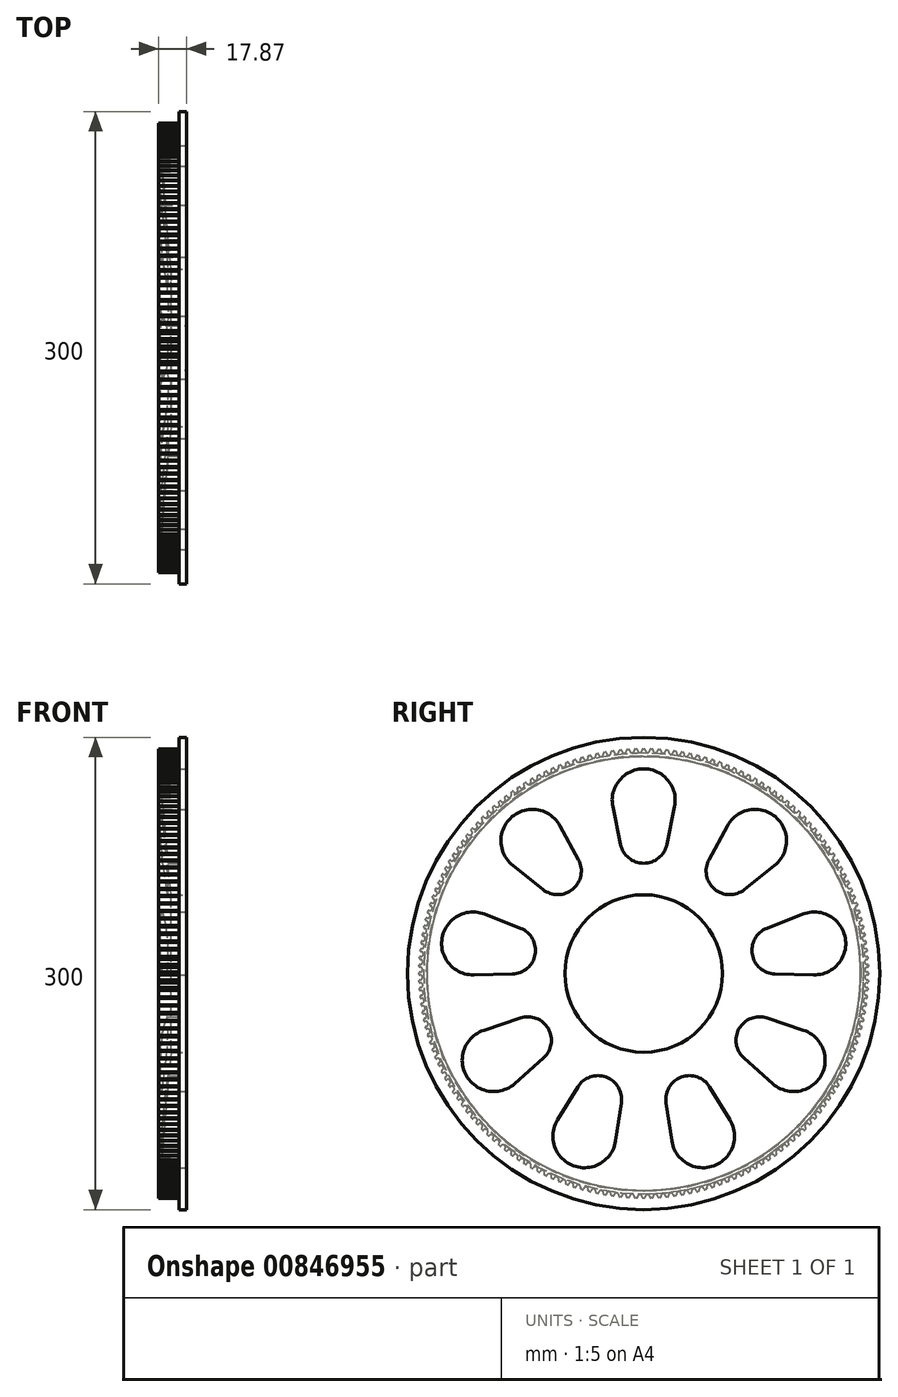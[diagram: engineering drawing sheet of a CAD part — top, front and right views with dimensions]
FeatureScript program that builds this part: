
annotation { "Feature Type Name" : "Feature", "Feature Type Description" : "" }
export const myFeature = defineFeature(function(context is Context, id is Id, definition is map)
    precondition{}
    {
        {
            var Q0;
            Q0=qCreatedBy(makeId("Front.planeOp"),FACE);
            var sketch = newSketch(context, id + "F0", { "sketchPlane" : qUnion([Q0])});
            skLineSegment(sketch, "E0", {"start": v(-17.87, 139.92) * mm, "end": v(-4.72, 139.92) * mm});
            skLineSegment(sketch, "E1", {"start": v(-4.72, 139.92) * mm, "end": v(-4.72, 150) * mm});
            skLineSegment(sketch, "E2", {"start": v(-4.72, 150) * mm, "end": v(0, 150) * mm});
            skLineSegment(sketch, "E3", {"start": v(0, 150) * mm, "end": v(0, 50) * mm});
            skLineSegment(sketch, "E4", {"start": v(0, 50) * mm, "end": v(-10, 50) * mm});
            skLineSegment(sketch, "E5", {"start": v(-10, 50) * mm, "end": v(-17.87, 139.92) * mm});
            skLineSegment(sketch, "E6", {"start": v(0, 0) * mm, "end": v(-63.64, 0) * mm, "construction": true});
            skSolve(sketch);
        }
        {
            var Q0;
            Q0 = qSketchRegion(id + "F0", true);
            var Q1;
            Q1 = qConstructionFilter(qBodyType(qCreatedBy(id + "F0" ,EDGE), BodyType.WIRE), ConstructionObject.NO);
            var Q2;
            Q2=sQuery(id+"F0.wireOp",EDGE,"E6");
            revolve(context, id + "F1", {"surfaceOperationType" : NewSurfaceOperationType.NEW, "entities" : qUnion([Q0]), "surfaceEntities" : qUnion([Q1]), "axis" : qUnion([Q2]), "revolveType" : RevolveType.FULL});
        }
        {
            var Q0;
            Q0=qCreatedBy(makeId("Right.planeOp"),FACE);
            var sketch = newSketch(context, id + "F2", { "sketchPlane" : qUnion([Q0])});
            skArc(sketch, "E7", {"start": v(19.6, 106) * mm, "mid": v(0, 130) * mm, "end": v(-19.6, 106) * mm});
            skArc(sketch, "E8", {"start": v(-14.7, 82) * mm, "mid": v(0, 70) * mm, "end": v(14.7, 82) * mm});
            skLineSegment(sketch, "E9", {"start": v(-19.6, 106) * mm, "end": v(-14.7, 82) * mm});
            skLineSegment(sketch, "E10", {"start": v(19.6, 106) * mm, "end": v(14.7, 82) * mm});
            skCircle(sketch, "E11", {"center": v(0, 0) * mm, "radius": 85 * mm, "construction": true});
            skCircle(sketch, "E12", {"center": v(0, 0) * mm, "radius": 110 * mm, "construction": true});
            skLineSegment(sketch, "E13.1.0", {"start": v(-83.15, 68.6) * mm, "end": v(-63.97, 53.37) * mm});
            skArc(sketch, "E13.1.1", {"start": v(-63.97, 53.37) * mm, "mid": v(-45, 53.62) * mm, "end": v(-41.45, 72.26) * mm});
            skArc(sketch, "E13.1.2", {"start": v(-53.12, 93.8) * mm, "mid": v(-83.56, 99.59) * mm, "end": v(-83.15, 68.6) * mm});
            skLineSegment(sketch, "E13.1.3", {"start": v(-53.12, 93.8) * mm, "end": v(-41.45, 72.26) * mm});
            skLineSegment(sketch, "E13.2.0", {"start": v(-107.8, -0.9) * mm, "end": v(-83.3, -0.23) * mm});
            skArc(sketch, "E13.2.1", {"start": v(-83.3, -0.23) * mm, "mid": v(-68.94, 12.16) * mm, "end": v(-78.2, 28.71) * mm});
            skArc(sketch, "E13.2.2", {"start": v(-100.99, 37.7) * mm, "mid": v(-128.03, 22.57) * mm, "end": v(-107.8, -0.9) * mm});
            skLineSegment(sketch, "E13.2.3", {"start": v(-100.99, 37.7) * mm, "end": v(-78.2, 28.71) * mm});
            skLineSegment(sketch, "E13.3.0", {"start": v(-82, -69.97) * mm, "end": v(-63.67, -53.73) * mm});
            skArc(sketch, "E13.3.1", {"start": v(-63.67, -53.73) * mm, "mid": v(-60.62, -35) * mm, "end": v(-78.36, -28.27) * mm});
            skArc(sketch, "E13.3.2", {"start": v(-101.6, -36.03) * mm, "mid": v(-112.58, -65) * mm, "end": v(-82, -69.97) * mm});
            skLineSegment(sketch, "E13.3.3", {"start": v(-101.6, -36.03) * mm, "end": v(-78.36, -28.27) * mm});
            skLineSegment(sketch, "E13.4.0", {"start": v(-17.84, -106.3) * mm, "end": v(-14.24, -82.08) * mm});
            skArc(sketch, "E13.4.1", {"start": v(-14.24, -82.08) * mm, "mid": v(-23.94, -65.78) * mm, "end": v(-41.86, -72.03) * mm});
            skArc(sketch, "E13.4.2", {"start": v(-54.67, -92.9) * mm, "mid": v(-44.46, -122.16) * mm, "end": v(-17.84, -106.3) * mm});
            skLineSegment(sketch, "E13.4.3", {"start": v(-54.67, -92.9) * mm, "end": v(-41.86, -72.03) * mm});
            skLineSegment(sketch, "E13.5.0", {"start": v(54.67, -92.9) * mm, "end": v(41.86, -72.03) * mm});
            skArc(sketch, "E13.5.1", {"start": v(41.86, -72.03) * mm, "mid": v(23.94, -65.78) * mm, "end": v(14.24, -82.08) * mm});
            skArc(sketch, "E13.5.2", {"start": v(17.84, -106.3) * mm, "mid": v(44.46, -122.16) * mm, "end": v(54.67, -92.9) * mm});
            skLineSegment(sketch, "E13.5.3", {"start": v(17.84, -106.3) * mm, "end": v(14.24, -82.08) * mm});
            skLineSegment(sketch, "E13.6.0", {"start": v(101.6, -36.03) * mm, "end": v(78.36, -28.27) * mm});
            skArc(sketch, "E13.6.1", {"start": v(78.36, -28.27) * mm, "mid": v(60.62, -35) * mm, "end": v(63.67, -53.73) * mm});
            skArc(sketch, "E13.6.2", {"start": v(82, -69.97) * mm, "mid": v(112.58, -65) * mm, "end": v(101.6, -36.03) * mm});
            skLineSegment(sketch, "E13.6.3", {"start": v(82, -69.97) * mm, "end": v(63.67, -53.73) * mm});
            skLineSegment(sketch, "E13.7.0", {"start": v(100.99, 37.7) * mm, "end": v(78.2, 28.71) * mm});
            skArc(sketch, "E13.7.1", {"start": v(78.2, 28.71) * mm, "mid": v(68.94, 12.16) * mm, "end": v(83.3, -0.23) * mm});
            skArc(sketch, "E13.7.2", {"start": v(107.8, -0.9) * mm, "mid": v(128.03, 22.57) * mm, "end": v(100.99, 37.7) * mm});
            skLineSegment(sketch, "E13.7.3", {"start": v(107.8, -0.9) * mm, "end": v(83.3, -0.23) * mm});
            skArc(sketch, "E14.3.8.0", {"start": v(41.45, 72.26) * mm, "mid": v(45, 53.62) * mm, "end": v(63.97, 53.37) * mm});
            skArc(sketch, "E14.7.8.0", {"start": v(83.15, 68.6) * mm, "mid": v(83.56, 99.59) * mm, "end": v(53.12, 93.8) * mm});
            skLineSegment(sketch, "E14.8.8.0", {"start": v(53.12, 93.8) * mm, "end": v(41.45, 72.26) * mm});
            skLineSegment(sketch, "E14.11.8.0", {"start": v(83.15, 68.6) * mm, "end": v(63.97, 53.37) * mm});
            skSolve(sketch);
        }
        {
            var Q0;
            Q0 = qSketchRegion(id + "F2", true);
            extrude(context, id + "F3", {"entities" : qUnion([Q0]), "operationType" : NewBodyOperationType.REMOVE, "endBound" : BoundingType.THROUGH_ALL, "oppositeDirection" : true, "depth" : 25 * mm, "offsetDistance" : 25 * mm});
        }
        {
            var Q0;
            Q0=makeQuery(id+"F1.opRevolve","SWEPT_FACE",FACE,{"disambiguationData":[OSD([sQuery(id+"F0.wireOp",EDGE,"E1")])]});
            var sketch = newSketch(context, id + "F4", { "sketchPlane" : qUnion([Q0])});
            skArc(sketch, "E15", {"start": v(0.94, 142.17) * mm, "mid": v(0.82, 142.52) * mm, "end": v(0.49, 142.67) * mm});
            skLineSegment(sketch, "E16", {"start": v(0, 142.67) * mm, "end": v(0, 137.75) * mm, "construction": true});
            skLineSegment(sketch, "E17", {"start": v(4.8, 137.58) * mm, "end": v(6.82, 195.24) * mm, "construction": true});
            skCircle(sketch, "E18", {"center": v(0, 0) * mm, "radius": 140.48 * mm, "construction": true});
            skCircle(sketch, "E19", {"center": v(0, 0) * mm, "radius": 142.67 * mm, "construction": true});
            skCircle(sketch, "E20", {"center": v(0, 0) * mm, "radius": 143.24 * mm, "construction": true});
            skArc(sketch, "E21", {"start": v(4.5, 142.6) * mm, "mid": v(4.15, 142.46) * mm, "end": v(4.02, 142.11) * mm});
            skArc(sketch, "E22", {"start": v(0.94, 142.17) * mm, "mid": v(2.45, 140.46) * mm, "end": v(4.02, 142.11) * mm});
            skLineSegment(sketch, "E23", {"start": v(0, 0) * mm, "end": v(4.11, 235.63) * mm, "construction": true});
            skLineSegment(sketch, "E24", {"start": v(0.49, 142.67) * mm, "end": v(0, 142.67) * mm});
            skLineSegment(sketch, "E25", {"start": v(4.98, 142.58) * mm, "end": v(4.5, 142.6) * mm});
            skLineSegment(sketch, "E26", {"start": v(4.98, 142.58) * mm, "end": v(4.8, 137.58) * mm});
            skLineSegment(sketch, "E27", {"start": v(0, 137.75) * mm, "end": v(0, 142.67) * mm});
            skLineSegment(sketch, "E28", {"start": v(0, 137.75) * mm, "end": v(4.8, 137.58) * mm});
            skArc(sketch, "E29.1.0", {"start": v(-4.02, 142.11) * mm, "mid": v(-2.45, 140.46) * mm, "end": v(-0.94, 142.17) * mm});
            skLineSegment(sketch, "E29.1.1", {"start": v(-4.98, 142.58) * mm, "end": v(-4.8, 137.67) * mm, "construction": true});
            skLineSegment(sketch, "E29.1.2", {"start": v(0, 142.67) * mm, "end": v(0, 137.67) * mm});
            skLineSegment(sketch, "E29.1.3", {"start": v(-4.8, 137.67) * mm, "end": v(0, 137.67) * mm});
            skLineSegment(sketch, "E29.1.4", {"start": v(-4.8, 137.67) * mm, "end": v(-4.98, 142.58) * mm});
            skLineSegment(sketch, "E29.1.5", {"start": v(0, 142.67) * mm, "end": v(-0.49, 142.67) * mm});
            skArc(sketch, "E29.1.6", {"start": v(-0.49, 142.67) * mm, "mid": v(-0.82, 142.52) * mm, "end": v(-0.94, 142.17) * mm});
            skArc(sketch, "E29.1.7", {"start": v(-4.02, 142.11) * mm, "mid": v(-4.15, 142.46) * mm, "end": v(-4.5, 142.6) * mm});
            skLineSegment(sketch, "E29.1.8", {"start": v(-4.5, 142.6) * mm, "end": v(-4.98, 142.58) * mm});
            skArc(sketch, "E29.2.0", {"start": v(-8.98, 141.89) * mm, "mid": v(-7.35, 140.3) * mm, "end": v(-5.9, 142.05) * mm});
            skLineSegment(sketch, "E29.2.1", {"start": v(-9.95, 142.32) * mm, "end": v(-9.6, 137.41) * mm, "construction": true});
            skLineSegment(sketch, "E29.2.2", {"start": v(-4.98, 142.58) * mm, "end": v(-4.8, 137.58) * mm});
            skLineSegment(sketch, "E29.2.3", {"start": v(-9.6, 137.41) * mm, "end": v(-4.8, 137.58) * mm});
            skLineSegment(sketch, "E29.2.4", {"start": v(-9.6, 137.41) * mm, "end": v(-9.95, 142.32) * mm});
            skLineSegment(sketch, "E29.2.5", {"start": v(-4.98, 142.58) * mm, "end": v(-5.47, 142.56) * mm});
            skArc(sketch, "E29.2.6", {"start": v(-5.47, 142.56) * mm, "mid": v(-5.8, 142.4) * mm, "end": v(-5.9, 142.05) * mm});
            skArc(sketch, "E29.2.7", {"start": v(-8.98, 141.89) * mm, "mid": v(-9.12, 142.23) * mm, "end": v(-9.46, 142.35) * mm});
            skLineSegment(sketch, "E29.2.8", {"start": v(-9.46, 142.35) * mm, "end": v(-9.95, 142.32) * mm});
            skArc(sketch, "E29.3.0", {"start": v(-13.93, 141.49) * mm, "mid": v(-12.24, 139.95) * mm, "end": v(-10.85, 141.76) * mm});
            skLineSegment(sketch, "E29.3.1", {"start": v(-14.91, 141.89) * mm, "end": v(-14.4, 137) * mm, "construction": true});
            skLineSegment(sketch, "E29.3.2", {"start": v(-9.95, 142.32) * mm, "end": v(-9.6, 137.33) * mm});
            skLineSegment(sketch, "E29.3.3", {"start": v(-14.4, 137) * mm, "end": v(-9.6, 137.33) * mm});
            skLineSegment(sketch, "E29.3.4", {"start": v(-14.4, 137) * mm, "end": v(-14.91, 141.89) * mm});
            skLineSegment(sketch, "E29.3.5", {"start": v(-9.95, 142.32) * mm, "end": v(-10.44, 142.29) * mm});
            skArc(sketch, "E29.3.6", {"start": v(-10.44, 142.29) * mm, "mid": v(-10.76, 142.11) * mm, "end": v(-10.85, 141.76) * mm});
            skArc(sketch, "E29.3.7", {"start": v(-13.93, 141.49) * mm, "mid": v(-14.08, 141.82) * mm, "end": v(-14.43, 141.94) * mm});
            skLineSegment(sketch, "E29.3.8", {"start": v(-14.43, 141.94) * mm, "end": v(-14.91, 141.89) * mm});
            skArc(sketch, "E29.4.0", {"start": v(-18.86, 140.91) * mm, "mid": v(-17.12, 139.44) * mm, "end": v(-15.8, 141.3) * mm});
            skLineSegment(sketch, "E29.4.1", {"start": v(-19.86, 141.28) * mm, "end": v(-19.17, 136.4) * mm, "construction": true});
            skLineSegment(sketch, "E29.4.2", {"start": v(-14.91, 141.89) * mm, "end": v(-14.39, 136.91) * mm});
            skLineSegment(sketch, "E29.4.3", {"start": v(-19.17, 136.4) * mm, "end": v(-14.39, 136.91) * mm});
            skLineSegment(sketch, "E29.4.4", {"start": v(-19.17, 136.4) * mm, "end": v(-19.86, 141.28) * mm});
            skLineSegment(sketch, "E29.4.5", {"start": v(-14.91, 141.89) * mm, "end": v(-15.4, 141.83) * mm});
            skArc(sketch, "E29.4.6", {"start": v(-15.4, 141.83) * mm, "mid": v(-15.72, 141.65) * mm, "end": v(-15.8, 141.3) * mm});
            skArc(sketch, "E29.4.7", {"start": v(-18.86, 140.91) * mm, "mid": v(-19.02, 141.24) * mm, "end": v(-19.37, 141.35) * mm});
            skLineSegment(sketch, "E29.4.8", {"start": v(-19.37, 141.35) * mm, "end": v(-19.86, 141.28) * mm});
            skArc(sketch, "E29.5.0", {"start": v(-23.76, 140.17) * mm, "mid": v(-21.98, 138.75) * mm, "end": v(-20.72, 140.65) * mm});
            skLineSegment(sketch, "E29.5.1", {"start": v(-24.77, 140.5) * mm, "end": v(-23.92, 135.66) * mm, "construction": true});
            skLineSegment(sketch, "E29.5.2", {"start": v(-19.86, 141.28) * mm, "end": v(-19.16, 136.33) * mm});
            skLineSegment(sketch, "E29.5.3", {"start": v(-23.92, 135.66) * mm, "end": v(-19.16, 136.33) * mm});
            skLineSegment(sketch, "E29.5.4", {"start": v(-23.92, 135.66) * mm, "end": v(-24.77, 140.5) * mm});
            skLineSegment(sketch, "E29.5.5", {"start": v(-19.86, 141.28) * mm, "end": v(-20.34, 141.21) * mm});
            skArc(sketch, "E29.5.6", {"start": v(-20.34, 141.21) * mm, "mid": v(-20.65, 141.02) * mm, "end": v(-20.72, 140.65) * mm});
            skArc(sketch, "E29.5.7", {"start": v(-23.76, 140.17) * mm, "mid": v(-23.94, 140.5) * mm, "end": v(-24.3, 140.58) * mm});
            skLineSegment(sketch, "E29.5.8", {"start": v(-24.3, 140.58) * mm, "end": v(-24.77, 140.5) * mm});
            skArc(sketch, "E29.6.0", {"start": v(-28.64, 139.26) * mm, "mid": v(-26.8, 137.9) * mm, "end": v(-25.61, 139.84) * mm});
            skLineSegment(sketch, "E29.6.1", {"start": v(-29.66, 139.55) * mm, "end": v(-28.64, 134.74) * mm, "construction": true});
            skLineSegment(sketch, "E29.6.2", {"start": v(-24.77, 140.5) * mm, "end": v(-23.9, 135.57) * mm});
            skLineSegment(sketch, "E29.6.3", {"start": v(-28.64, 134.74) * mm, "end": v(-23.9, 135.57) * mm});
            skLineSegment(sketch, "E29.6.4", {"start": v(-28.64, 134.74) * mm, "end": v(-29.66, 139.55) * mm});
            skLineSegment(sketch, "E29.6.5", {"start": v(-24.77, 140.5) * mm, "end": v(-25.25, 140.41) * mm});
            skArc(sketch, "E29.6.6", {"start": v(-25.25, 140.41) * mm, "mid": v(-25.56, 140.2) * mm, "end": v(-25.61, 139.84) * mm});
            skArc(sketch, "E29.6.7", {"start": v(-28.64, 139.26) * mm, "mid": v(-28.82, 139.57) * mm, "end": v(-29.18, 139.65) * mm});
            skLineSegment(sketch, "E29.6.8", {"start": v(-29.18, 139.65) * mm, "end": v(-29.66, 139.55) * mm});
            skArc(sketch, "E29.7.0", {"start": v(-33.48, 138.17) * mm, "mid": v(-31.6, 136.88) * mm, "end": v(-30.48, 138.87) * mm});
            skLineSegment(sketch, "E29.7.1", {"start": v(-34.51, 138.43) * mm, "end": v(-33.32, 133.66) * mm, "construction": true});
            skLineSegment(sketch, "E29.7.2", {"start": v(-29.66, 139.55) * mm, "end": v(-28.62, 134.66) * mm});
            skLineSegment(sketch, "E29.7.3", {"start": v(-33.32, 133.66) * mm, "end": v(-28.62, 134.66) * mm});
            skLineSegment(sketch, "E29.7.4", {"start": v(-33.32, 133.66) * mm, "end": v(-34.51, 138.43) * mm});
            skLineSegment(sketch, "E29.7.5", {"start": v(-29.66, 139.55) * mm, "end": v(-30.14, 139.45) * mm});
            skArc(sketch, "E29.7.6", {"start": v(-30.14, 139.45) * mm, "mid": v(-30.44, 139.23) * mm, "end": v(-30.48, 138.87) * mm});
            skArc(sketch, "E29.7.7", {"start": v(-33.48, 138.17) * mm, "mid": v(-33.68, 138.48) * mm, "end": v(-34.04, 138.55) * mm});
            skLineSegment(sketch, "E29.7.8", {"start": v(-34.04, 138.55) * mm, "end": v(-34.51, 138.43) * mm});
            skArc(sketch, "E29.8.0", {"start": v(-38.28, 136.92) * mm, "mid": v(-36.36, 135.7) * mm, "end": v(-35.3, 137.72) * mm});
            skLineSegment(sketch, "E29.8.1", {"start": v(-39.32, 137.14) * mm, "end": v(-37.97, 132.41) * mm, "construction": true});
            skLineSegment(sketch, "E29.8.2", {"start": v(-34.51, 138.43) * mm, "end": v(-33.3, 133.58) * mm});
            skLineSegment(sketch, "E29.8.3", {"start": v(-37.97, 132.41) * mm, "end": v(-33.3, 133.58) * mm});
            skLineSegment(sketch, "E29.8.4", {"start": v(-37.97, 132.41) * mm, "end": v(-39.32, 137.14) * mm});
            skLineSegment(sketch, "E29.8.5", {"start": v(-34.51, 138.43) * mm, "end": v(-34.99, 138.31) * mm});
            skArc(sketch, "E29.8.6", {"start": v(-34.99, 138.31) * mm, "mid": v(-35.28, 138.08) * mm, "end": v(-35.3, 137.72) * mm});
            skArc(sketch, "E29.8.7", {"start": v(-38.28, 136.92) * mm, "mid": v(-38.5, 137.22) * mm, "end": v(-38.85, 137.28) * mm});
            skLineSegment(sketch, "E29.8.8", {"start": v(-38.85, 137.28) * mm, "end": v(-39.32, 137.14) * mm});
            skArc(sketch, "E29.9.0", {"start": v(-43.04, 135.5) * mm, "mid": v(-41.07, 134.35) * mm, "end": v(-40.09, 136.4) * mm});
            skLineSegment(sketch, "E29.9.1", {"start": v(-44.09, 135.69) * mm, "end": v(-42.57, 131) * mm, "construction": true});
            skLineSegment(sketch, "E29.9.2", {"start": v(-39.32, 137.14) * mm, "end": v(-37.95, 132.33) * mm});
            skLineSegment(sketch, "E29.9.3", {"start": v(-42.57, 131) * mm, "end": v(-37.95, 132.33) * mm});
            skLineSegment(sketch, "E29.9.4", {"start": v(-42.57, 131) * mm, "end": v(-44.09, 135.69) * mm});
            skLineSegment(sketch, "E29.9.5", {"start": v(-39.32, 137.14) * mm, "end": v(-39.8, 137) * mm});
            skArc(sketch, "E29.9.6", {"start": v(-39.8, 137) * mm, "mid": v(-40.08, 136.77) * mm, "end": v(-40.09, 136.4) * mm});
            skArc(sketch, "E29.9.7", {"start": v(-43.04, 135.5) * mm, "mid": v(-43.26, 135.8) * mm, "end": v(-43.62, 135.84) * mm});
            skLineSegment(sketch, "E29.9.8", {"start": v(-43.62, 135.84) * mm, "end": v(-44.09, 135.69) * mm});
            skArc(sketch, "E29.10.0", {"start": v(-47.74, 133.91) * mm, "mid": v(-45.74, 132.83) * mm, "end": v(-44.82, 134.92) * mm});
            skLineSegment(sketch, "E29.10.1", {"start": v(-48.8, 134.06) * mm, "end": v(-47.11, 129.44) * mm, "construction": true});
            skLineSegment(sketch, "E29.10.2", {"start": v(-44.09, 135.69) * mm, "end": v(-42.54, 130.93) * mm});
            skLineSegment(sketch, "E29.10.3", {"start": v(-47.11, 129.44) * mm, "end": v(-42.54, 130.93) * mm});
            skLineSegment(sketch, "E29.10.4", {"start": v(-47.11, 129.44) * mm, "end": v(-48.8, 134.06) * mm});
            skLineSegment(sketch, "E29.10.5", {"start": v(-44.09, 135.69) * mm, "end": v(-44.55, 135.53) * mm});
            skArc(sketch, "E29.10.6", {"start": v(-44.55, 135.53) * mm, "mid": v(-44.82, 135.29) * mm, "end": v(-44.82, 134.92) * mm});
            skArc(sketch, "E29.10.7", {"start": v(-47.74, 133.91) * mm, "mid": v(-47.97, 134.2) * mm, "end": v(-48.34, 134.23) * mm});
            skLineSegment(sketch, "E29.10.8", {"start": v(-48.34, 134.23) * mm, "end": v(-48.8, 134.06) * mm});
            skArc(sketch, "E29.11.0", {"start": v(-52.39, 132.17) * mm, "mid": v(-50.35, 131.15) * mm, "end": v(-49.5, 133.27) * mm});
            skLineSegment(sketch, "E29.11.1", {"start": v(-53.44, 132.28) * mm, "end": v(-51.6, 127.72) * mm, "construction": true});
            skLineSegment(sketch, "E29.11.2", {"start": v(-48.8, 134.06) * mm, "end": v(-47.08, 129.36) * mm});
            skLineSegment(sketch, "E29.11.3", {"start": v(-51.6, 127.72) * mm, "end": v(-47.08, 129.36) * mm});
            skLineSegment(sketch, "E29.11.4", {"start": v(-51.6, 127.72) * mm, "end": v(-53.44, 132.28) * mm});
            skLineSegment(sketch, "E29.11.5", {"start": v(-48.8, 134.06) * mm, "end": v(-49.25, 133.9) * mm});
            skArc(sketch, "E29.11.6", {"start": v(-49.25, 133.9) * mm, "mid": v(-49.52, 133.64) * mm, "end": v(-49.5, 133.27) * mm});
            skArc(sketch, "E29.11.7", {"start": v(-52.39, 132.17) * mm, "mid": v(-52.62, 132.45) * mm, "end": v(-53, 132.46) * mm});
            skLineSegment(sketch, "E29.11.8", {"start": v(-53, 132.46) * mm, "end": v(-53.44, 132.28) * mm});
            skArc(sketch, "E29.12.0", {"start": v(-56.97, 130.26) * mm, "mid": v(-54.9, 129.32) * mm, "end": v(-54.13, 131.46) * mm});
            skLineSegment(sketch, "E29.12.1", {"start": v(-58.03, 130.33) * mm, "end": v(-56.03, 125.84) * mm, "construction": true});
            skLineSegment(sketch, "E29.12.2", {"start": v(-53.44, 132.28) * mm, "end": v(-51.57, 127.64) * mm});
            skLineSegment(sketch, "E29.12.3", {"start": v(-56.03, 125.84) * mm, "end": v(-51.57, 127.64) * mm});
            skLineSegment(sketch, "E29.12.4", {"start": v(-56.03, 125.84) * mm, "end": v(-58.03, 130.33) * mm});
            skLineSegment(sketch, "E29.12.5", {"start": v(-53.44, 132.28) * mm, "end": v(-53.9, 132.1) * mm});
            skArc(sketch, "E29.12.6", {"start": v(-53.9, 132.1) * mm, "mid": v(-54.15, 131.83) * mm, "end": v(-54.13, 131.46) * mm});
            skArc(sketch, "E29.12.7", {"start": v(-56.97, 130.26) * mm, "mid": v(-57.21, 130.53) * mm, "end": v(-57.58, 130.53) * mm});
            skLineSegment(sketch, "E29.12.8", {"start": v(-57.58, 130.53) * mm, "end": v(-58.03, 130.33) * mm});
            skArc(sketch, "E29.13.0", {"start": v(-61.48, 128.2) * mm, "mid": v(-59.37, 127.32) * mm, "end": v(-58.68, 129.5) * mm});
            skLineSegment(sketch, "E29.13.1", {"start": v(-62.54, 128.23) * mm, "end": v(-60.39, 123.8) * mm, "construction": true});
            skLineSegment(sketch, "E29.13.2", {"start": v(-58.03, 130.33) * mm, "end": v(-56, 125.76) * mm});
            skLineSegment(sketch, "E29.13.3", {"start": v(-60.39, 123.8) * mm, "end": v(-56, 125.76) * mm});
            skLineSegment(sketch, "E29.13.4", {"start": v(-60.39, 123.8) * mm, "end": v(-62.54, 128.23) * mm});
            skLineSegment(sketch, "E29.13.5", {"start": v(-58.03, 130.33) * mm, "end": v(-58.47, 130.13) * mm});
            skArc(sketch, "E29.13.6", {"start": v(-58.47, 130.13) * mm, "mid": v(-58.72, 129.86) * mm, "end": v(-58.68, 129.5) * mm});
            skArc(sketch, "E29.13.7", {"start": v(-61.48, 128.2) * mm, "mid": v(-61.73, 128.45) * mm, "end": v(-62.1, 128.44) * mm});
            skLineSegment(sketch, "E29.13.8", {"start": v(-62.1, 128.44) * mm, "end": v(-62.54, 128.23) * mm});
            skArc(sketch, "E29.14.0", {"start": v(-65.91, 125.97) * mm, "mid": v(-63.78, 125.17) * mm, "end": v(-63.17, 127.37) * mm});
            skLineSegment(sketch, "E29.14.1", {"start": v(-66.98, 125.97) * mm, "end": v(-64.67, 121.63) * mm, "construction": true});
            skLineSegment(sketch, "E29.14.2", {"start": v(-62.54, 128.23) * mm, "end": v(-60.35, 123.73) * mm});
            skLineSegment(sketch, "E29.14.3", {"start": v(-64.67, 121.63) * mm, "end": v(-60.35, 123.73) * mm});
            skLineSegment(sketch, "E29.14.4", {"start": v(-64.67, 121.63) * mm, "end": v(-66.98, 125.97) * mm});
            skLineSegment(sketch, "E29.14.5", {"start": v(-62.54, 128.23) * mm, "end": v(-62.98, 128.01) * mm});
            skArc(sketch, "E29.14.6", {"start": v(-62.98, 128.01) * mm, "mid": v(-63.22, 127.73) * mm, "end": v(-63.17, 127.37) * mm});
            skArc(sketch, "E29.14.7", {"start": v(-65.91, 125.97) * mm, "mid": v(-66.18, 126.22) * mm, "end": v(-66.55, 126.2) * mm});
            skLineSegment(sketch, "E29.14.8", {"start": v(-66.55, 126.2) * mm, "end": v(-66.98, 125.97) * mm});
            skArc(sketch, "E29.15.0", {"start": v(-70.27, 123.59) * mm, "mid": v(-68.1, 122.87) * mm, "end": v(-67.57, 125.09) * mm});
            skLineSegment(sketch, "E29.15.1", {"start": v(-71.33, 123.55) * mm, "end": v(-68.87, 119.3) * mm, "construction": true});
            skLineSegment(sketch, "E29.15.2", {"start": v(-66.98, 125.97) * mm, "end": v(-64.63, 121.55) * mm});
            skLineSegment(sketch, "E29.15.3", {"start": v(-68.87, 119.3) * mm, "end": v(-64.63, 121.55) * mm});
            skLineSegment(sketch, "E29.15.4", {"start": v(-68.87, 119.3) * mm, "end": v(-71.33, 123.55) * mm});
            skLineSegment(sketch, "E29.15.5", {"start": v(-66.98, 125.97) * mm, "end": v(-67.4, 125.74) * mm});
            skArc(sketch, "E29.15.6", {"start": v(-67.4, 125.74) * mm, "mid": v(-67.64, 125.45) * mm, "end": v(-67.57, 125.09) * mm});
            skArc(sketch, "E29.15.7", {"start": v(-70.27, 123.59) * mm, "mid": v(-70.54, 123.84) * mm, "end": v(-70.91, 123.8) * mm});
            skLineSegment(sketch, "E29.15.8", {"start": v(-70.91, 123.8) * mm, "end": v(-71.33, 123.55) * mm});
            skArc(sketch, "E29.16.0", {"start": v(-74.54, 121.06) * mm, "mid": v(-72.35, 120.42) * mm, "end": v(-71.9, 122.65) * mm});
            skLineSegment(sketch, "E29.16.1", {"start": v(-75.6, 120.99) * mm, "end": v(-73, 116.82) * mm, "construction": true});
            skLineSegment(sketch, "E29.16.2", {"start": v(-71.33, 123.55) * mm, "end": v(-68.83, 119.22) * mm});
            skLineSegment(sketch, "E29.16.3", {"start": v(-73, 116.82) * mm, "end": v(-68.83, 119.22) * mm});
            skLineSegment(sketch, "E29.16.4", {"start": v(-73, 116.82) * mm, "end": v(-75.6, 120.99) * mm});
            skLineSegment(sketch, "E29.16.5", {"start": v(-71.33, 123.55) * mm, "end": v(-71.76, 123.3) * mm});
            skArc(sketch, "E29.16.6", {"start": v(-71.76, 123.3) * mm, "mid": v(-71.97, 123.01) * mm, "end": v(-71.9, 122.65) * mm});
            skArc(sketch, "E29.16.7", {"start": v(-74.54, 121.06) * mm, "mid": v(-74.82, 121.3) * mm, "end": v(-75.19, 121.25) * mm});
            skLineSegment(sketch, "E29.16.8", {"start": v(-75.19, 121.25) * mm, "end": v(-75.6, 120.99) * mm});
            skArc(sketch, "E29.17.0", {"start": v(-78.72, 118.39) * mm, "mid": v(-76.51, 117.82) * mm, "end": v(-76.13, 120.07) * mm});
            skLineSegment(sketch, "E29.17.1", {"start": v(-79.78, 118.28) * mm, "end": v(-77.03, 114.2) * mm, "construction": true});
            skLineSegment(sketch, "E29.17.2", {"start": v(-75.6, 120.99) * mm, "end": v(-72.95, 116.75) * mm});
            skLineSegment(sketch, "E29.17.3", {"start": v(-77.03, 114.2) * mm, "end": v(-72.95, 116.75) * mm});
            skLineSegment(sketch, "E29.17.4", {"start": v(-77.03, 114.2) * mm, "end": v(-79.78, 118.28) * mm});
            skLineSegment(sketch, "E29.17.5", {"start": v(-75.6, 120.99) * mm, "end": v(-76.02, 120.73) * mm});
            skArc(sketch, "E29.17.6", {"start": v(-76.02, 120.73) * mm, "mid": v(-76.22, 120.42) * mm, "end": v(-76.13, 120.07) * mm});
            skArc(sketch, "E29.17.7", {"start": v(-78.72, 118.39) * mm, "mid": v(-79.01, 118.61) * mm, "end": v(-79.37, 118.55) * mm});
            skLineSegment(sketch, "E29.17.8", {"start": v(-79.37, 118.55) * mm, "end": v(-79.78, 118.28) * mm});
            skArc(sketch, "E29.18.0", {"start": v(-82.8, 115.57) * mm, "mid": v(-80.58, 115.08) * mm, "end": v(-80.28, 117.34) * mm});
            skLineSegment(sketch, "E29.18.1", {"start": v(-83.86, 115.42) * mm, "end": v(-80.97, 111.44) * mm, "construction": true});
            skLineSegment(sketch, "E29.18.2", {"start": v(-79.78, 118.28) * mm, "end": v(-76.98, 114.13) * mm});
            skLineSegment(sketch, "E29.18.3", {"start": v(-80.97, 111.44) * mm, "end": v(-76.98, 114.13) * mm});
            skLineSegment(sketch, "E29.18.4", {"start": v(-80.97, 111.44) * mm, "end": v(-83.86, 115.42) * mm});
            skLineSegment(sketch, "E29.18.5", {"start": v(-79.78, 118.28) * mm, "end": v(-80.18, 118) * mm});
            skArc(sketch, "E29.18.6", {"start": v(-80.18, 118) * mm, "mid": v(-80.38, 117.7) * mm, "end": v(-80.28, 117.34) * mm});
            skArc(sketch, "E29.18.7", {"start": v(-82.8, 115.57) * mm, "mid": v(-83.1, 115.78) * mm, "end": v(-83.46, 115.7) * mm});
            skLineSegment(sketch, "E29.18.8", {"start": v(-83.46, 115.7) * mm, "end": v(-83.86, 115.42) * mm});
            skArc(sketch, "E29.19.0", {"start": v(-86.79, 112.6) * mm, "mid": v(-84.55, 112.2) * mm, "end": v(-84.32, 114.46) * mm});
            skLineSegment(sketch, "E29.19.1", {"start": v(-87.84, 112.42) * mm, "end": v(-84.8, 108.55) * mm, "construction": true});
            skLineSegment(sketch, "E29.19.2", {"start": v(-83.86, 115.42) * mm, "end": v(-80.92, 111.37) * mm});
            skLineSegment(sketch, "E29.19.3", {"start": v(-84.8, 108.55) * mm, "end": v(-80.92, 111.37) * mm});
            skLineSegment(sketch, "E29.19.4", {"start": v(-84.8, 108.55) * mm, "end": v(-87.84, 112.42) * mm});
            skLineSegment(sketch, "E29.19.5", {"start": v(-83.86, 115.42) * mm, "end": v(-84.25, 115.13) * mm});
            skArc(sketch, "E29.19.6", {"start": v(-84.25, 115.13) * mm, "mid": v(-84.44, 114.81) * mm, "end": v(-84.32, 114.46) * mm});
            skArc(sketch, "E29.19.7", {"start": v(-86.79, 112.6) * mm, "mid": v(-87.1, 112.81) * mm, "end": v(-87.45, 112.72) * mm});
            skLineSegment(sketch, "E29.19.8", {"start": v(-87.45, 112.72) * mm, "end": v(-87.84, 112.42) * mm});
            skArc(sketch, "E29.20.0", {"start": v(-90.66, 109.5) * mm, "mid": v(-88.4, 109.18) * mm, "end": v(-88.27, 111.45) * mm});
            skLineSegment(sketch, "E29.20.1", {"start": v(-91.7, 109.29) * mm, "end": v(-88.54, 105.52) * mm, "construction": true});
            skLineSegment(sketch, "E29.20.2", {"start": v(-87.84, 112.42) * mm, "end": v(-84.76, 108.48) * mm});
            skLineSegment(sketch, "E29.20.3", {"start": v(-88.54, 105.52) * mm, "end": v(-84.76, 108.48) * mm});
            skLineSegment(sketch, "E29.20.4", {"start": v(-88.54, 105.52) * mm, "end": v(-91.7, 109.29) * mm});
            skLineSegment(sketch, "E29.20.5", {"start": v(-87.84, 112.42) * mm, "end": v(-88.22, 112.12) * mm});
            skArc(sketch, "E29.20.6", {"start": v(-88.22, 112.12) * mm, "mid": v(-88.4, 111.8) * mm, "end": v(-88.27, 111.45) * mm});
            skArc(sketch, "E29.20.7", {"start": v(-90.66, 109.5) * mm, "mid": v(-90.98, 109.7) * mm, "end": v(-91.33, 109.6) * mm});
            skLineSegment(sketch, "E29.20.8", {"start": v(-91.33, 109.6) * mm, "end": v(-91.7, 109.29) * mm});
            skArc(sketch, "E29.21.0", {"start": v(-94.43, 106.28) * mm, "mid": v(-92.17, 106.02) * mm, "end": v(-92.1, 108.3) * mm});
            skLineSegment(sketch, "E29.21.1", {"start": v(-95.46, 106.02) * mm, "end": v(-92.17, 102.37) * mm, "construction": true});
            skLineSegment(sketch, "E29.21.2", {"start": v(-91.7, 109.3) * mm, "end": v(-88.49, 105.46) * mm});
            skLineSegment(sketch, "E29.21.3", {"start": v(-92.17, 102.37) * mm, "end": v(-88.49, 105.46) * mm});
            skLineSegment(sketch, "E29.21.4", {"start": v(-92.17, 102.37) * mm, "end": v(-95.46, 106.02) * mm});
            skLineSegment(sketch, "E29.21.5", {"start": v(-91.7, 109.3) * mm, "end": v(-92.08, 108.98) * mm});
            skArc(sketch, "E29.21.6", {"start": v(-92.08, 108.98) * mm, "mid": v(-92.24, 108.64) * mm, "end": v(-92.1, 108.3) * mm});
            skArc(sketch, "E29.21.7", {"start": v(-94.43, 106.28) * mm, "mid": v(-94.75, 106.46) * mm, "end": v(-95.1, 106.35) * mm});
            skLineSegment(sketch, "E29.21.8", {"start": v(-95.1, 106.35) * mm, "end": v(-95.46, 106.02) * mm});
            skArc(sketch, "E29.22.0", {"start": v(-98.08, 102.92) * mm, "mid": v(-95.81, 102.74) * mm, "end": v(-95.83, 105.02) * mm});
            skLineSegment(sketch, "E29.22.1", {"start": v(-99.1, 102.63) * mm, "end": v(-95.69, 99.09) * mm, "construction": true});
            skLineSegment(sketch, "E29.22.2", {"start": v(-95.46, 106.02) * mm, "end": v(-92.12, 102.3) * mm});
            skLineSegment(sketch, "E29.22.3", {"start": v(-95.69, 99.09) * mm, "end": v(-92.12, 102.3) * mm});
            skLineSegment(sketch, "E29.22.4", {"start": v(-95.69, 99.09) * mm, "end": v(-99.1, 102.63) * mm});
            skLineSegment(sketch, "E29.22.5", {"start": v(-95.46, 106.02) * mm, "end": v(-95.83, 105.7) * mm});
            skArc(sketch, "E29.22.6", {"start": v(-95.83, 105.7) * mm, "mid": v(-95.97, 105.36) * mm, "end": v(-95.83, 105.02) * mm});
            skArc(sketch, "E29.22.7", {"start": v(-98.08, 102.92) * mm, "mid": v(-98.4, 103.1) * mm, "end": v(-98.75, 102.97) * mm});
            skLineSegment(sketch, "E29.22.8", {"start": v(-98.75, 102.97) * mm, "end": v(-99.1, 102.63) * mm});
            skArc(sketch, "E29.23.0", {"start": v(-101.61, 99.43) * mm, "mid": v(-99.34, 99.34) * mm, "end": v(-99.43, 101.61) * mm});
            skLineSegment(sketch, "E29.23.1", {"start": v(-102.63, 99.1) * mm, "end": v(-99.09, 95.69) * mm, "construction": true});
            skLineSegment(sketch, "E29.23.2", {"start": v(-99.1, 102.63) * mm, "end": v(-95.63, 99.03) * mm});
            skLineSegment(sketch, "E29.23.3", {"start": v(-99.09, 95.69) * mm, "end": v(-95.63, 99.03) * mm});
            skLineSegment(sketch, "E29.23.4", {"start": v(-99.09, 95.69) * mm, "end": v(-102.63, 99.1) * mm});
            skLineSegment(sketch, "E29.23.5", {"start": v(-99.1, 102.63) * mm, "end": v(-99.46, 102.29) * mm});
            skArc(sketch, "E29.23.6", {"start": v(-99.46, 102.29) * mm, "mid": v(-99.6, 101.95) * mm, "end": v(-99.43, 101.61) * mm});
            skArc(sketch, "E29.23.7", {"start": v(-101.61, 99.43) * mm, "mid": v(-101.95, 99.6) * mm, "end": v(-102.29, 99.46) * mm});
            skLineSegment(sketch, "E29.23.8", {"start": v(-102.29, 99.46) * mm, "end": v(-102.63, 99.1) * mm});
            skArc(sketch, "E29.24.0", {"start": v(-105.02, 95.83) * mm, "mid": v(-102.74, 95.81) * mm, "end": v(-102.92, 98.08) * mm});
            skLineSegment(sketch, "E29.24.1", {"start": v(-106.02, 95.46) * mm, "end": v(-102.37, 92.17) * mm, "construction": true});
            skLineSegment(sketch, "E29.24.2", {"start": v(-102.63, 99.1) * mm, "end": v(-99.03, 95.63) * mm});
            skLineSegment(sketch, "E29.24.3", {"start": v(-102.37, 92.17) * mm, "end": v(-99.03, 95.63) * mm});
            skLineSegment(sketch, "E29.24.4", {"start": v(-102.37, 92.17) * mm, "end": v(-106.02, 95.46) * mm});
            skLineSegment(sketch, "E29.24.5", {"start": v(-102.63, 99.1) * mm, "end": v(-102.97, 98.75) * mm});
            skArc(sketch, "E29.24.6", {"start": v(-102.97, 98.75) * mm, "mid": v(-103.1, 98.4) * mm, "end": v(-102.92, 98.08) * mm});
            skArc(sketch, "E29.24.7", {"start": v(-105.02, 95.83) * mm, "mid": v(-105.36, 95.97) * mm, "end": v(-105.7, 95.83) * mm});
            skLineSegment(sketch, "E29.24.8", {"start": v(-105.7, 95.83) * mm, "end": v(-106.02, 95.46) * mm});
            skArc(sketch, "E29.25.0", {"start": v(-108.3, 92.1) * mm, "mid": v(-106.02, 92.17) * mm, "end": v(-106.28, 94.43) * mm});
            skLineSegment(sketch, "E29.25.1", {"start": v(-109.29, 91.7) * mm, "end": v(-105.52, 88.54) * mm, "construction": true});
            skLineSegment(sketch, "E29.25.2", {"start": v(-106.02, 95.46) * mm, "end": v(-102.3, 92.12) * mm});
            skLineSegment(sketch, "E29.25.3", {"start": v(-105.52, 88.54) * mm, "end": v(-102.3, 92.12) * mm});
            skLineSegment(sketch, "E29.25.4", {"start": v(-105.52, 88.54) * mm, "end": v(-109.29, 91.7) * mm});
            skLineSegment(sketch, "E29.25.5", {"start": v(-106.02, 95.46) * mm, "end": v(-106.35, 95.1) * mm});
            skArc(sketch, "E29.25.6", {"start": v(-106.35, 95.1) * mm, "mid": v(-106.46, 94.75) * mm, "end": v(-106.28, 94.43) * mm});
            skArc(sketch, "E29.25.7", {"start": v(-108.3, 92.1) * mm, "mid": v(-108.64, 92.24) * mm, "end": v(-108.98, 92.08) * mm});
            skLineSegment(sketch, "E29.25.8", {"start": v(-108.98, 92.08) * mm, "end": v(-109.29, 91.7) * mm});
            skArc(sketch, "E29.26.0", {"start": v(-111.45, 88.27) * mm, "mid": v(-109.18, 88.4) * mm, "end": v(-109.5, 90.66) * mm});
            skLineSegment(sketch, "E29.26.1", {"start": v(-112.42, 87.84) * mm, "end": v(-108.55, 84.8) * mm, "construction": true});
            skLineSegment(sketch, "E29.26.2", {"start": v(-109.3, 91.7) * mm, "end": v(-105.46, 88.49) * mm});
            skLineSegment(sketch, "E29.26.3", {"start": v(-108.55, 84.8) * mm, "end": v(-105.46, 88.49) * mm});
            skLineSegment(sketch, "E29.26.4", {"start": v(-108.55, 84.8) * mm, "end": v(-112.42, 87.84) * mm});
            skLineSegment(sketch, "E29.26.5", {"start": v(-109.3, 91.7) * mm, "end": v(-109.6, 91.33) * mm});
            skArc(sketch, "E29.26.6", {"start": v(-109.6, 91.33) * mm, "mid": v(-109.7, 90.98) * mm, "end": v(-109.5, 90.66) * mm});
            skArc(sketch, "E29.26.7", {"start": v(-111.45, 88.27) * mm, "mid": v(-111.8, 88.4) * mm, "end": v(-112.12, 88.22) * mm});
            skLineSegment(sketch, "E29.26.8", {"start": v(-112.12, 88.22) * mm, "end": v(-112.42, 87.84) * mm});
            skArc(sketch, "E29.27.0", {"start": v(-114.46, 84.32) * mm, "mid": v(-112.2, 84.55) * mm, "end": v(-112.6, 86.79) * mm});
            skLineSegment(sketch, "E29.27.1", {"start": v(-115.42, 83.86) * mm, "end": v(-111.44, 80.97) * mm, "construction": true});
            skLineSegment(sketch, "E29.27.2", {"start": v(-112.42, 87.84) * mm, "end": v(-108.48, 84.76) * mm});
            skLineSegment(sketch, "E29.27.3", {"start": v(-111.44, 80.97) * mm, "end": v(-108.48, 84.76) * mm});
            skLineSegment(sketch, "E29.27.4", {"start": v(-111.44, 80.97) * mm, "end": v(-115.42, 83.86) * mm});
            skLineSegment(sketch, "E29.27.5", {"start": v(-112.42, 87.84) * mm, "end": v(-112.72, 87.45) * mm});
            skArc(sketch, "E29.27.6", {"start": v(-112.72, 87.45) * mm, "mid": v(-112.81, 87.1) * mm, "end": v(-112.6, 86.79) * mm});
            skArc(sketch, "E29.27.7", {"start": v(-114.46, 84.32) * mm, "mid": v(-114.81, 84.44) * mm, "end": v(-115.13, 84.25) * mm});
            skLineSegment(sketch, "E29.27.8", {"start": v(-115.13, 84.25) * mm, "end": v(-115.42, 83.86) * mm});
            skArc(sketch, "E29.28.0", {"start": v(-117.34, 80.28) * mm, "mid": v(-115.08, 80.58) * mm, "end": v(-115.57, 82.8) * mm});
            skLineSegment(sketch, "E29.28.1", {"start": v(-118.28, 79.78) * mm, "end": v(-114.2, 77.03) * mm, "construction": true});
            skLineSegment(sketch, "E29.28.2", {"start": v(-115.42, 83.86) * mm, "end": v(-111.37, 80.92) * mm});
            skLineSegment(sketch, "E29.28.3", {"start": v(-114.2, 77.03) * mm, "end": v(-111.37, 80.92) * mm});
            skLineSegment(sketch, "E29.28.4", {"start": v(-114.2, 77.03) * mm, "end": v(-118.28, 79.78) * mm});
            skLineSegment(sketch, "E29.28.5", {"start": v(-115.42, 83.86) * mm, "end": v(-115.7, 83.46) * mm});
            skArc(sketch, "E29.28.6", {"start": v(-115.7, 83.46) * mm, "mid": v(-115.78, 83.1) * mm, "end": v(-115.57, 82.8) * mm});
            skArc(sketch, "E29.28.7", {"start": v(-117.34, 80.28) * mm, "mid": v(-117.7, 80.38) * mm, "end": v(-118, 80.18) * mm});
            skLineSegment(sketch, "E29.28.8", {"start": v(-118, 80.18) * mm, "end": v(-118.28, 79.78) * mm});
            skArc(sketch, "E29.29.0", {"start": v(-120.07, 76.13) * mm, "mid": v(-117.82, 76.51) * mm, "end": v(-118.39, 78.72) * mm});
            skLineSegment(sketch, "E29.29.1", {"start": v(-120.99, 75.6) * mm, "end": v(-116.82, 73) * mm, "construction": true});
            skLineSegment(sketch, "E29.29.2", {"start": v(-118.28, 79.78) * mm, "end": v(-114.13, 76.98) * mm});
            skLineSegment(sketch, "E29.29.3", {"start": v(-116.82, 73) * mm, "end": v(-114.13, 76.98) * mm});
            skLineSegment(sketch, "E29.29.4", {"start": v(-116.82, 73) * mm, "end": v(-120.99, 75.6) * mm});
            skLineSegment(sketch, "E29.29.5", {"start": v(-118.28, 79.78) * mm, "end": v(-118.55, 79.37) * mm});
            skArc(sketch, "E29.29.6", {"start": v(-118.55, 79.37) * mm, "mid": v(-118.61, 79.01) * mm, "end": v(-118.39, 78.72) * mm});
            skArc(sketch, "E29.29.7", {"start": v(-120.07, 76.13) * mm, "mid": v(-120.42, 76.22) * mm, "end": v(-120.73, 76.02) * mm});
            skLineSegment(sketch, "E29.29.8", {"start": v(-120.73, 76.02) * mm, "end": v(-120.99, 75.6) * mm});
            skArc(sketch, "E29.30.0", {"start": v(-122.65, 71.9) * mm, "mid": v(-120.42, 72.35) * mm, "end": v(-121.06, 74.54) * mm});
            skLineSegment(sketch, "E29.30.1", {"start": v(-123.55, 71.33) * mm, "end": v(-119.3, 68.87) * mm, "construction": true});
            skLineSegment(sketch, "E29.30.2", {"start": v(-120.99, 75.6) * mm, "end": v(-116.75, 72.95) * mm});
            skLineSegment(sketch, "E29.30.3", {"start": v(-119.3, 68.87) * mm, "end": v(-116.75, 72.95) * mm});
            skLineSegment(sketch, "E29.30.4", {"start": v(-119.3, 68.87) * mm, "end": v(-123.55, 71.33) * mm});
            skLineSegment(sketch, "E29.30.5", {"start": v(-120.99, 75.6) * mm, "end": v(-121.25, 75.19) * mm});
            skArc(sketch, "E29.30.6", {"start": v(-121.25, 75.19) * mm, "mid": v(-121.3, 74.82) * mm, "end": v(-121.06, 74.54) * mm});
            skArc(sketch, "E29.30.7", {"start": v(-122.65, 71.9) * mm, "mid": v(-123.01, 71.97) * mm, "end": v(-123.3, 71.76) * mm});
            skLineSegment(sketch, "E29.30.8", {"start": v(-123.3, 71.76) * mm, "end": v(-123.55, 71.33) * mm});
            skArc(sketch, "E29.31.0", {"start": v(-125.09, 67.57) * mm, "mid": v(-122.87, 68.1) * mm, "end": v(-123.59, 70.27) * mm});
            skLineSegment(sketch, "E29.31.1", {"start": v(-125.97, 66.98) * mm, "end": v(-121.63, 64.67) * mm, "construction": true});
            skLineSegment(sketch, "E29.31.2", {"start": v(-123.55, 71.33) * mm, "end": v(-119.22, 68.83) * mm});
            skLineSegment(sketch, "E29.31.3", {"start": v(-121.63, 64.67) * mm, "end": v(-119.22, 68.83) * mm});
            skLineSegment(sketch, "E29.31.4", {"start": v(-121.63, 64.67) * mm, "end": v(-125.97, 66.98) * mm});
            skLineSegment(sketch, "E29.31.5", {"start": v(-123.55, 71.33) * mm, "end": v(-123.8, 70.91) * mm});
            skArc(sketch, "E29.31.6", {"start": v(-123.8, 70.91) * mm, "mid": v(-123.84, 70.54) * mm, "end": v(-123.59, 70.27) * mm});
            skArc(sketch, "E29.31.7", {"start": v(-125.09, 67.57) * mm, "mid": v(-125.45, 67.64) * mm, "end": v(-125.74, 67.4) * mm});
            skLineSegment(sketch, "E29.31.8", {"start": v(-125.74, 67.4) * mm, "end": v(-125.97, 66.98) * mm});
            skArc(sketch, "E29.32.0", {"start": v(-127.37, 63.17) * mm, "mid": v(-125.17, 63.78) * mm, "end": v(-125.97, 65.91) * mm});
            skLineSegment(sketch, "E29.32.1", {"start": v(-128.23, 62.54) * mm, "end": v(-123.8, 60.39) * mm, "construction": true});
            skLineSegment(sketch, "E29.32.2", {"start": v(-125.97, 66.98) * mm, "end": v(-121.55, 64.63) * mm});
            skLineSegment(sketch, "E29.32.3", {"start": v(-123.8, 60.39) * mm, "end": v(-121.55, 64.63) * mm});
            skLineSegment(sketch, "E29.32.4", {"start": v(-123.8, 60.39) * mm, "end": v(-128.23, 62.54) * mm});
            skLineSegment(sketch, "E29.32.5", {"start": v(-125.97, 66.98) * mm, "end": v(-126.2, 66.55) * mm});
            skArc(sketch, "E29.32.6", {"start": v(-126.2, 66.55) * mm, "mid": v(-126.22, 66.18) * mm, "end": v(-125.97, 65.91) * mm});
            skArc(sketch, "E29.32.7", {"start": v(-127.37, 63.17) * mm, "mid": v(-127.73, 63.22) * mm, "end": v(-128.01, 62.98) * mm});
            skLineSegment(sketch, "E29.32.8", {"start": v(-128.01, 62.98) * mm, "end": v(-128.23, 62.54) * mm});
            skArc(sketch, "E29.33.0", {"start": v(-129.5, 58.68) * mm, "mid": v(-127.32, 59.37) * mm, "end": v(-128.2, 61.48) * mm});
            skLineSegment(sketch, "E29.33.1", {"start": v(-130.33, 58.03) * mm, "end": v(-125.84, 56.03) * mm, "construction": true});
            skLineSegment(sketch, "E29.33.2", {"start": v(-128.23, 62.54) * mm, "end": v(-123.73, 60.35) * mm});
            skLineSegment(sketch, "E29.33.3", {"start": v(-125.84, 56.03) * mm, "end": v(-123.73, 60.35) * mm});
            skLineSegment(sketch, "E29.33.4", {"start": v(-125.84, 56.03) * mm, "end": v(-130.33, 58.03) * mm});
            skLineSegment(sketch, "E29.33.5", {"start": v(-128.23, 62.54) * mm, "end": v(-128.44, 62.1) * mm});
            skArc(sketch, "E29.33.6", {"start": v(-128.44, 62.1) * mm, "mid": v(-128.45, 61.73) * mm, "end": v(-128.2, 61.48) * mm});
            skArc(sketch, "E29.33.7", {"start": v(-129.5, 58.68) * mm, "mid": v(-129.86, 58.72) * mm, "end": v(-130.13, 58.47) * mm});
            skLineSegment(sketch, "E29.33.8", {"start": v(-130.13, 58.47) * mm, "end": v(-130.33, 58.03) * mm});
            skArc(sketch, "E29.34.0", {"start": v(-131.46, 54.13) * mm, "mid": v(-129.32, 54.9) * mm, "end": v(-130.26, 56.97) * mm});
            skLineSegment(sketch, "E29.34.1", {"start": v(-132.28, 53.44) * mm, "end": v(-127.72, 51.6) * mm, "construction": true});
            skLineSegment(sketch, "E29.34.2", {"start": v(-130.33, 58.03) * mm, "end": v(-125.76, 56) * mm});
            skLineSegment(sketch, "E29.34.3", {"start": v(-127.72, 51.6) * mm, "end": v(-125.76, 56) * mm});
            skLineSegment(sketch, "E29.34.4", {"start": v(-127.72, 51.6) * mm, "end": v(-132.28, 53.44) * mm});
            skLineSegment(sketch, "E29.34.5", {"start": v(-130.33, 58.03) * mm, "end": v(-130.53, 57.58) * mm});
            skArc(sketch, "E29.34.6", {"start": v(-130.53, 57.58) * mm, "mid": v(-130.53, 57.21) * mm, "end": v(-130.26, 56.97) * mm});
            skArc(sketch, "E29.34.7", {"start": v(-131.46, 54.13) * mm, "mid": v(-131.83, 54.15) * mm, "end": v(-132.1, 53.9) * mm});
            skLineSegment(sketch, "E29.34.8", {"start": v(-132.1, 53.9) * mm, "end": v(-132.28, 53.44) * mm});
            skArc(sketch, "E29.35.0", {"start": v(-133.27, 49.5) * mm, "mid": v(-131.15, 50.35) * mm, "end": v(-132.17, 52.39) * mm});
            skLineSegment(sketch, "E29.35.1", {"start": v(-134.06, 48.8) * mm, "end": v(-129.44, 47.11) * mm, "construction": true});
            skLineSegment(sketch, "E29.35.2", {"start": v(-132.28, 53.44) * mm, "end": v(-127.64, 51.57) * mm});
            skLineSegment(sketch, "E29.35.3", {"start": v(-129.44, 47.11) * mm, "end": v(-127.64, 51.57) * mm});
            skLineSegment(sketch, "E29.35.4", {"start": v(-129.44, 47.11) * mm, "end": v(-134.06, 48.8) * mm});
            skLineSegment(sketch, "E29.35.5", {"start": v(-132.28, 53.44) * mm, "end": v(-132.46, 53) * mm});
            skArc(sketch, "E29.35.6", {"start": v(-132.46, 53) * mm, "mid": v(-132.45, 52.62) * mm, "end": v(-132.17, 52.39) * mm});
            skArc(sketch, "E29.35.7", {"start": v(-133.27, 49.5) * mm, "mid": v(-133.64, 49.52) * mm, "end": v(-133.9, 49.25) * mm});
            skLineSegment(sketch, "E29.35.8", {"start": v(-133.9, 49.25) * mm, "end": v(-134.06, 48.8) * mm});
            skArc(sketch, "E29.36.0", {"start": v(-134.92, 44.82) * mm, "mid": v(-132.83, 45.74) * mm, "end": v(-133.91, 47.74) * mm});
            skLineSegment(sketch, "E29.36.1", {"start": v(-135.69, 44.09) * mm, "end": v(-131, 42.57) * mm, "construction": true});
            skLineSegment(sketch, "E29.36.2", {"start": v(-134.06, 48.8) * mm, "end": v(-129.36, 47.08) * mm});
            skLineSegment(sketch, "E29.36.3", {"start": v(-131, 42.57) * mm, "end": v(-129.36, 47.08) * mm});
            skLineSegment(sketch, "E29.36.4", {"start": v(-131, 42.57) * mm, "end": v(-135.69, 44.09) * mm});
            skLineSegment(sketch, "E29.36.5", {"start": v(-134.06, 48.8) * mm, "end": v(-134.23, 48.34) * mm});
            skArc(sketch, "E29.36.6", {"start": v(-134.23, 48.34) * mm, "mid": v(-134.2, 47.97) * mm, "end": v(-133.91, 47.74) * mm});
            skArc(sketch, "E29.36.7", {"start": v(-134.92, 44.82) * mm, "mid": v(-135.29, 44.82) * mm, "end": v(-135.53, 44.55) * mm});
            skLineSegment(sketch, "E29.36.8", {"start": v(-135.53, 44.55) * mm, "end": v(-135.69, 44.09) * mm});
            skArc(sketch, "E29.37.0", {"start": v(-136.4, 40.09) * mm, "mid": v(-134.35, 41.07) * mm, "end": v(-135.5, 43.04) * mm});
            skLineSegment(sketch, "E29.37.1", {"start": v(-137.14, 39.32) * mm, "end": v(-132.41, 37.97) * mm, "construction": true});
            skLineSegment(sketch, "E29.37.2", {"start": v(-135.69, 44.09) * mm, "end": v(-130.93, 42.54) * mm});
            skLineSegment(sketch, "E29.37.3", {"start": v(-132.41, 37.97) * mm, "end": v(-130.93, 42.54) * mm});
            skLineSegment(sketch, "E29.37.4", {"start": v(-132.41, 37.97) * mm, "end": v(-137.14, 39.32) * mm});
            skLineSegment(sketch, "E29.37.5", {"start": v(-135.69, 44.09) * mm, "end": v(-135.84, 43.62) * mm});
            skArc(sketch, "E29.37.6", {"start": v(-135.84, 43.62) * mm, "mid": v(-135.8, 43.26) * mm, "end": v(-135.5, 43.04) * mm});
            skArc(sketch, "E29.37.7", {"start": v(-136.4, 40.09) * mm, "mid": v(-136.77, 40.08) * mm, "end": v(-137, 39.8) * mm});
            skLineSegment(sketch, "E29.37.8", {"start": v(-137, 39.8) * mm, "end": v(-137.14, 39.32) * mm});
            skArc(sketch, "E29.38.0", {"start": v(-137.72, 35.3) * mm, "mid": v(-135.7, 36.36) * mm, "end": v(-136.92, 38.28) * mm});
            skLineSegment(sketch, "E29.38.1", {"start": v(-138.43, 34.51) * mm, "end": v(-133.66, 33.32) * mm, "construction": true});
            skLineSegment(sketch, "E29.38.2", {"start": v(-137.14, 39.32) * mm, "end": v(-132.33, 37.95) * mm});
            skLineSegment(sketch, "E29.38.3", {"start": v(-133.66, 33.32) * mm, "end": v(-132.33, 37.95) * mm});
            skLineSegment(sketch, "E29.38.4", {"start": v(-133.66, 33.32) * mm, "end": v(-138.43, 34.51) * mm});
            skLineSegment(sketch, "E29.38.5", {"start": v(-137.14, 39.32) * mm, "end": v(-137.28, 38.85) * mm});
            skArc(sketch, "E29.38.6", {"start": v(-137.28, 38.85) * mm, "mid": v(-137.22, 38.5) * mm, "end": v(-136.92, 38.28) * mm});
            skArc(sketch, "E29.38.7", {"start": v(-137.72, 35.3) * mm, "mid": v(-138.08, 35.28) * mm, "end": v(-138.31, 34.99) * mm});
            skLineSegment(sketch, "E29.38.8", {"start": v(-138.31, 34.99) * mm, "end": v(-138.43, 34.51) * mm});
            skArc(sketch, "E29.39.0", {"start": v(-138.87, 30.48) * mm, "mid": v(-136.88, 31.6) * mm, "end": v(-138.17, 33.48) * mm});
            skLineSegment(sketch, "E29.39.1", {"start": v(-139.55, 29.66) * mm, "end": v(-134.74, 28.64) * mm, "construction": true});
            skLineSegment(sketch, "E29.39.2", {"start": v(-138.43, 34.51) * mm, "end": v(-133.58, 33.3) * mm});
            skLineSegment(sketch, "E29.39.3", {"start": v(-134.74, 28.64) * mm, "end": v(-133.58, 33.3) * mm});
            skLineSegment(sketch, "E29.39.4", {"start": v(-134.74, 28.64) * mm, "end": v(-139.55, 29.66) * mm});
            skLineSegment(sketch, "E29.39.5", {"start": v(-138.43, 34.51) * mm, "end": v(-138.55, 34.04) * mm});
            skArc(sketch, "E29.39.6", {"start": v(-138.55, 34.04) * mm, "mid": v(-138.48, 33.68) * mm, "end": v(-138.17, 33.48) * mm});
            skArc(sketch, "E29.39.7", {"start": v(-138.87, 30.48) * mm, "mid": v(-139.23, 30.44) * mm, "end": v(-139.45, 30.14) * mm});
            skLineSegment(sketch, "E29.39.8", {"start": v(-139.45, 30.14) * mm, "end": v(-139.55, 29.66) * mm});
            skArc(sketch, "E29.40.0", {"start": v(-139.84, 25.61) * mm, "mid": v(-137.9, 26.8) * mm, "end": v(-139.26, 28.64) * mm});
            skLineSegment(sketch, "E29.40.1", {"start": v(-140.5, 24.77) * mm, "end": v(-135.66, 23.92) * mm, "construction": true});
            skLineSegment(sketch, "E29.40.2", {"start": v(-139.55, 29.66) * mm, "end": v(-134.66, 28.62) * mm});
            skLineSegment(sketch, "E29.40.3", {"start": v(-135.66, 23.92) * mm, "end": v(-134.66, 28.62) * mm});
            skLineSegment(sketch, "E29.40.4", {"start": v(-135.66, 23.92) * mm, "end": v(-140.5, 24.77) * mm});
            skLineSegment(sketch, "E29.40.5", {"start": v(-139.55, 29.66) * mm, "end": v(-139.65, 29.18) * mm});
            skArc(sketch, "E29.40.6", {"start": v(-139.65, 29.18) * mm, "mid": v(-139.57, 28.82) * mm, "end": v(-139.26, 28.64) * mm});
            skArc(sketch, "E29.40.7", {"start": v(-139.84, 25.61) * mm, "mid": v(-140.2, 25.56) * mm, "end": v(-140.41, 25.25) * mm});
            skLineSegment(sketch, "E29.40.8", {"start": v(-140.41, 25.25) * mm, "end": v(-140.5, 24.77) * mm});
            skArc(sketch, "E29.41.0", {"start": v(-140.65, 20.72) * mm, "mid": v(-138.75, 21.98) * mm, "end": v(-140.17, 23.76) * mm});
            skLineSegment(sketch, "E29.41.1", {"start": v(-141.28, 19.86) * mm, "end": v(-136.4, 19.17) * mm, "construction": true});
            skLineSegment(sketch, "E29.41.2", {"start": v(-140.5, 24.77) * mm, "end": v(-135.57, 23.9) * mm});
            skLineSegment(sketch, "E29.41.3", {"start": v(-136.4, 19.17) * mm, "end": v(-135.57, 23.9) * mm});
            skLineSegment(sketch, "E29.41.4", {"start": v(-136.4, 19.17) * mm, "end": v(-141.28, 19.86) * mm});
            skLineSegment(sketch, "E29.41.5", {"start": v(-140.5, 24.77) * mm, "end": v(-140.58, 24.3) * mm});
            skArc(sketch, "E29.41.6", {"start": v(-140.58, 24.3) * mm, "mid": v(-140.5, 23.94) * mm, "end": v(-140.17, 23.76) * mm});
            skArc(sketch, "E29.41.7", {"start": v(-140.65, 20.72) * mm, "mid": v(-141.02, 20.65) * mm, "end": v(-141.21, 20.34) * mm});
            skLineSegment(sketch, "E29.41.8", {"start": v(-141.21, 20.34) * mm, "end": v(-141.28, 19.86) * mm});
            skArc(sketch, "E29.42.0", {"start": v(-141.3, 15.8) * mm, "mid": v(-139.44, 17.12) * mm, "end": v(-140.91, 18.86) * mm});
            skLineSegment(sketch, "E29.42.1", {"start": v(-141.89, 14.91) * mm, "end": v(-137, 14.4) * mm, "construction": true});
            skLineSegment(sketch, "E29.42.2", {"start": v(-141.28, 19.86) * mm, "end": v(-136.33, 19.16) * mm});
            skLineSegment(sketch, "E29.42.3", {"start": v(-137, 14.4) * mm, "end": v(-136.33, 19.16) * mm});
            skLineSegment(sketch, "E29.42.4", {"start": v(-137, 14.4) * mm, "end": v(-141.89, 14.91) * mm});
            skLineSegment(sketch, "E29.42.5", {"start": v(-141.28, 19.86) * mm, "end": v(-141.35, 19.37) * mm});
            skArc(sketch, "E29.42.6", {"start": v(-141.35, 19.37) * mm, "mid": v(-141.24, 19.02) * mm, "end": v(-140.91, 18.86) * mm});
            skArc(sketch, "E29.42.7", {"start": v(-141.3, 15.8) * mm, "mid": v(-141.65, 15.72) * mm, "end": v(-141.83, 15.4) * mm});
            skLineSegment(sketch, "E29.42.8", {"start": v(-141.83, 15.4) * mm, "end": v(-141.89, 14.91) * mm});
            skArc(sketch, "E29.43.0", {"start": v(-141.76, 10.85) * mm, "mid": v(-139.95, 12.24) * mm, "end": v(-141.49, 13.93) * mm});
            skLineSegment(sketch, "E29.43.1", {"start": v(-142.32, 9.95) * mm, "end": v(-137.41, 9.6) * mm, "construction": true});
            skLineSegment(sketch, "E29.43.2", {"start": v(-141.89, 14.91) * mm, "end": v(-136.91, 14.39) * mm});
            skLineSegment(sketch, "E29.43.3", {"start": v(-137.41, 9.6) * mm, "end": v(-136.91, 14.39) * mm});
            skLineSegment(sketch, "E29.43.4", {"start": v(-137.41, 9.6) * mm, "end": v(-142.32, 9.95) * mm});
            skLineSegment(sketch, "E29.43.5", {"start": v(-141.89, 14.91) * mm, "end": v(-141.94, 14.43) * mm});
            skArc(sketch, "E29.43.6", {"start": v(-141.94, 14.43) * mm, "mid": v(-141.82, 14.08) * mm, "end": v(-141.49, 13.93) * mm});
            skArc(sketch, "E29.43.7", {"start": v(-141.76, 10.85) * mm, "mid": v(-142.11, 10.76) * mm, "end": v(-142.29, 10.44) * mm});
            skLineSegment(sketch, "E29.43.8", {"start": v(-142.29, 10.44) * mm, "end": v(-142.32, 9.95) * mm});
            skArc(sketch, "E29.44.0", {"start": v(-142.05, 5.9) * mm, "mid": v(-140.3, 7.35) * mm, "end": v(-141.89, 8.98) * mm});
            skLineSegment(sketch, "E29.44.1", {"start": v(-142.58, 4.98) * mm, "end": v(-137.67, 4.8) * mm, "construction": true});
            skLineSegment(sketch, "E29.44.2", {"start": v(-142.32, 9.95) * mm, "end": v(-137.33, 9.6) * mm});
            skLineSegment(sketch, "E29.44.3", {"start": v(-137.67, 4.8) * mm, "end": v(-137.33, 9.6) * mm});
            skLineSegment(sketch, "E29.44.4", {"start": v(-137.67, 4.8) * mm, "end": v(-142.58, 4.98) * mm});
            skLineSegment(sketch, "E29.44.5", {"start": v(-142.32, 9.95) * mm, "end": v(-142.35, 9.46) * mm});
            skArc(sketch, "E29.44.6", {"start": v(-142.35, 9.46) * mm, "mid": v(-142.23, 9.12) * mm, "end": v(-141.89, 8.98) * mm});
            skArc(sketch, "E29.44.7", {"start": v(-142.05, 5.9) * mm, "mid": v(-142.4, 5.8) * mm, "end": v(-142.56, 5.47) * mm});
            skLineSegment(sketch, "E29.44.8", {"start": v(-142.56, 5.47) * mm, "end": v(-142.58, 4.98) * mm});
            skArc(sketch, "E29.45.0", {"start": v(-142.17, 0.94) * mm, "mid": v(-140.46, 2.45) * mm, "end": v(-142.11, 4.02) * mm});
            skLineSegment(sketch, "E29.45.1", {"start": v(-142.67, 0) * mm, "end": v(-137.75, 0) * mm, "construction": true});
            skLineSegment(sketch, "E29.45.2", {"start": v(-142.58, 4.98) * mm, "end": v(-137.58, 4.8) * mm});
            skLineSegment(sketch, "E29.45.3", {"start": v(-137.75, 0) * mm, "end": v(-137.58, 4.8) * mm});
            skLineSegment(sketch, "E29.45.4", {"start": v(-137.75, 0) * mm, "end": v(-142.67, 0) * mm});
            skLineSegment(sketch, "E29.45.5", {"start": v(-142.58, 4.98) * mm, "end": v(-142.6, 4.5) * mm});
            skArc(sketch, "E29.45.6", {"start": v(-142.6, 4.5) * mm, "mid": v(-142.46, 4.15) * mm, "end": v(-142.11, 4.02) * mm});
            skArc(sketch, "E29.45.7", {"start": v(-142.17, 0.94) * mm, "mid": v(-142.52, 0.82) * mm, "end": v(-142.67, 0.49) * mm});
            skLineSegment(sketch, "E29.45.8", {"start": v(-142.67, 0.49) * mm, "end": v(-142.67, 0) * mm});
            skArc(sketch, "E29.46.0", {"start": v(-142.11, -4.02) * mm, "mid": v(-140.46, -2.45) * mm, "end": v(-142.17, -0.94) * mm});
            skLineSegment(sketch, "E29.46.1", {"start": v(-142.58, -4.98) * mm, "end": v(-137.67, -4.8) * mm, "construction": true});
            skLineSegment(sketch, "E29.46.2", {"start": v(-142.67, 0) * mm, "end": v(-137.67, 0) * mm});
            skLineSegment(sketch, "E29.46.3", {"start": v(-137.67, -4.8) * mm, "end": v(-137.67, 0) * mm});
            skLineSegment(sketch, "E29.46.4", {"start": v(-137.67, -4.8) * mm, "end": v(-142.58, -4.98) * mm});
            skLineSegment(sketch, "E29.46.5", {"start": v(-142.67, 0) * mm, "end": v(-142.67, -0.49) * mm});
            skArc(sketch, "E29.46.6", {"start": v(-142.67, -0.49) * mm, "mid": v(-142.52, -0.82) * mm, "end": v(-142.17, -0.94) * mm});
            skArc(sketch, "E29.46.7", {"start": v(-142.11, -4.02) * mm, "mid": v(-142.46, -4.15) * mm, "end": v(-142.6, -4.5) * mm});
            skLineSegment(sketch, "E29.46.8", {"start": v(-142.6, -4.5) * mm, "end": v(-142.58, -4.98) * mm});
            skArc(sketch, "E29.47.0", {"start": v(-141.89, -8.98) * mm, "mid": v(-140.3, -7.35) * mm, "end": v(-142.05, -5.9) * mm});
            skLineSegment(sketch, "E29.47.1", {"start": v(-142.32, -9.95) * mm, "end": v(-137.41, -9.6) * mm, "construction": true});
            skLineSegment(sketch, "E29.47.2", {"start": v(-142.58, -4.98) * mm, "end": v(-137.58, -4.8) * mm});
            skLineSegment(sketch, "E29.47.3", {"start": v(-137.41, -9.6) * mm, "end": v(-137.58, -4.8) * mm});
            skLineSegment(sketch, "E29.47.4", {"start": v(-137.41, -9.6) * mm, "end": v(-142.32, -9.95) * mm});
            skLineSegment(sketch, "E29.47.5", {"start": v(-142.58, -4.98) * mm, "end": v(-142.56, -5.47) * mm});
            skArc(sketch, "E29.47.6", {"start": v(-142.56, -5.47) * mm, "mid": v(-142.4, -5.8) * mm, "end": v(-142.05, -5.9) * mm});
            skArc(sketch, "E29.47.7", {"start": v(-141.89, -8.98) * mm, "mid": v(-142.23, -9.12) * mm, "end": v(-142.35, -9.46) * mm});
            skLineSegment(sketch, "E29.47.8", {"start": v(-142.35, -9.46) * mm, "end": v(-142.32, -9.95) * mm});
            skArc(sketch, "E29.48.0", {"start": v(-141.49, -13.93) * mm, "mid": v(-139.95, -12.24) * mm, "end": v(-141.76, -10.85) * mm});
            skLineSegment(sketch, "E29.48.1", {"start": v(-141.89, -14.91) * mm, "end": v(-137, -14.4) * mm, "construction": true});
            skLineSegment(sketch, "E29.48.2", {"start": v(-142.32, -9.95) * mm, "end": v(-137.33, -9.6) * mm});
            skLineSegment(sketch, "E29.48.3", {"start": v(-137, -14.4) * mm, "end": v(-137.33, -9.6) * mm});
            skLineSegment(sketch, "E29.48.4", {"start": v(-137, -14.4) * mm, "end": v(-141.89, -14.91) * mm});
            skLineSegment(sketch, "E29.48.5", {"start": v(-142.32, -9.95) * mm, "end": v(-142.29, -10.44) * mm});
            skArc(sketch, "E29.48.6", {"start": v(-142.29, -10.44) * mm, "mid": v(-142.11, -10.76) * mm, "end": v(-141.76, -10.85) * mm});
            skArc(sketch, "E29.48.7", {"start": v(-141.49, -13.93) * mm, "mid": v(-141.82, -14.08) * mm, "end": v(-141.94, -14.43) * mm});
            skLineSegment(sketch, "E29.48.8", {"start": v(-141.94, -14.43) * mm, "end": v(-141.89, -14.91) * mm});
            skArc(sketch, "E29.49.0", {"start": v(-140.91, -18.86) * mm, "mid": v(-139.44, -17.12) * mm, "end": v(-141.3, -15.8) * mm});
            skLineSegment(sketch, "E29.49.1", {"start": v(-141.28, -19.86) * mm, "end": v(-136.4, -19.17) * mm, "construction": true});
            skLineSegment(sketch, "E29.49.2", {"start": v(-141.89, -14.91) * mm, "end": v(-136.91, -14.39) * mm});
            skLineSegment(sketch, "E29.49.3", {"start": v(-136.4, -19.17) * mm, "end": v(-136.91, -14.39) * mm});
            skLineSegment(sketch, "E29.49.4", {"start": v(-136.4, -19.17) * mm, "end": v(-141.28, -19.86) * mm});
            skLineSegment(sketch, "E29.49.5", {"start": v(-141.89, -14.91) * mm, "end": v(-141.83, -15.4) * mm});
            skArc(sketch, "E29.49.6", {"start": v(-141.83, -15.4) * mm, "mid": v(-141.65, -15.72) * mm, "end": v(-141.3, -15.8) * mm});
            skArc(sketch, "E29.49.7", {"start": v(-140.91, -18.86) * mm, "mid": v(-141.24, -19.02) * mm, "end": v(-141.35, -19.37) * mm});
            skLineSegment(sketch, "E29.49.8", {"start": v(-141.35, -19.37) * mm, "end": v(-141.28, -19.86) * mm});
            skArc(sketch, "E29.50.0", {"start": v(-140.17, -23.76) * mm, "mid": v(-138.75, -21.98) * mm, "end": v(-140.65, -20.72) * mm});
            skLineSegment(sketch, "E29.50.1", {"start": v(-140.5, -24.77) * mm, "end": v(-135.66, -23.92) * mm, "construction": true});
            skLineSegment(sketch, "E29.50.2", {"start": v(-141.28, -19.86) * mm, "end": v(-136.33, -19.16) * mm});
            skLineSegment(sketch, "E29.50.3", {"start": v(-135.66, -23.92) * mm, "end": v(-136.33, -19.16) * mm});
            skLineSegment(sketch, "E29.50.4", {"start": v(-135.66, -23.92) * mm, "end": v(-140.5, -24.77) * mm});
            skLineSegment(sketch, "E29.50.5", {"start": v(-141.28, -19.86) * mm, "end": v(-141.21, -20.34) * mm});
            skArc(sketch, "E29.50.6", {"start": v(-141.21, -20.34) * mm, "mid": v(-141.02, -20.65) * mm, "end": v(-140.65, -20.72) * mm});
            skArc(sketch, "E29.50.7", {"start": v(-140.17, -23.76) * mm, "mid": v(-140.5, -23.94) * mm, "end": v(-140.58, -24.3) * mm});
            skLineSegment(sketch, "E29.50.8", {"start": v(-140.58, -24.3) * mm, "end": v(-140.5, -24.77) * mm});
            skArc(sketch, "E29.51.0", {"start": v(-139.26, -28.64) * mm, "mid": v(-137.9, -26.8) * mm, "end": v(-139.84, -25.61) * mm});
            skLineSegment(sketch, "E29.51.1", {"start": v(-139.55, -29.66) * mm, "end": v(-134.74, -28.64) * mm, "construction": true});
            skLineSegment(sketch, "E29.51.2", {"start": v(-140.5, -24.77) * mm, "end": v(-135.57, -23.9) * mm});
            skLineSegment(sketch, "E29.51.3", {"start": v(-134.74, -28.64) * mm, "end": v(-135.57, -23.9) * mm});
            skLineSegment(sketch, "E29.51.4", {"start": v(-134.74, -28.64) * mm, "end": v(-139.55, -29.66) * mm});
            skLineSegment(sketch, "E29.51.5", {"start": v(-140.5, -24.77) * mm, "end": v(-140.41, -25.25) * mm});
            skArc(sketch, "E29.51.6", {"start": v(-140.41, -25.25) * mm, "mid": v(-140.2, -25.56) * mm, "end": v(-139.84, -25.61) * mm});
            skArc(sketch, "E29.51.7", {"start": v(-139.26, -28.64) * mm, "mid": v(-139.57, -28.82) * mm, "end": v(-139.65, -29.18) * mm});
            skLineSegment(sketch, "E29.51.8", {"start": v(-139.65, -29.18) * mm, "end": v(-139.55, -29.66) * mm});
            skArc(sketch, "E29.52.0", {"start": v(-138.17, -33.48) * mm, "mid": v(-136.88, -31.6) * mm, "end": v(-138.87, -30.48) * mm});
            skLineSegment(sketch, "E29.52.1", {"start": v(-138.43, -34.51) * mm, "end": v(-133.66, -33.32) * mm, "construction": true});
            skLineSegment(sketch, "E29.52.2", {"start": v(-139.55, -29.66) * mm, "end": v(-134.66, -28.62) * mm});
            skLineSegment(sketch, "E29.52.3", {"start": v(-133.66, -33.32) * mm, "end": v(-134.66, -28.62) * mm});
            skLineSegment(sketch, "E29.52.4", {"start": v(-133.66, -33.32) * mm, "end": v(-138.43, -34.51) * mm});
            skLineSegment(sketch, "E29.52.5", {"start": v(-139.55, -29.66) * mm, "end": v(-139.45, -30.14) * mm});
            skArc(sketch, "E29.52.6", {"start": v(-139.45, -30.14) * mm, "mid": v(-139.23, -30.44) * mm, "end": v(-138.87, -30.48) * mm});
            skArc(sketch, "E29.52.7", {"start": v(-138.17, -33.48) * mm, "mid": v(-138.48, -33.68) * mm, "end": v(-138.55, -34.04) * mm});
            skLineSegment(sketch, "E29.52.8", {"start": v(-138.55, -34.04) * mm, "end": v(-138.43, -34.51) * mm});
            skArc(sketch, "E29.53.0", {"start": v(-136.92, -38.28) * mm, "mid": v(-135.7, -36.36) * mm, "end": v(-137.72, -35.3) * mm});
            skLineSegment(sketch, "E29.53.1", {"start": v(-137.14, -39.32) * mm, "end": v(-132.41, -37.97) * mm, "construction": true});
            skLineSegment(sketch, "E29.53.2", {"start": v(-138.43, -34.51) * mm, "end": v(-133.58, -33.3) * mm});
            skLineSegment(sketch, "E29.53.3", {"start": v(-132.41, -37.97) * mm, "end": v(-133.58, -33.3) * mm});
            skLineSegment(sketch, "E29.53.4", {"start": v(-132.41, -37.97) * mm, "end": v(-137.14, -39.32) * mm});
            skLineSegment(sketch, "E29.53.5", {"start": v(-138.43, -34.51) * mm, "end": v(-138.31, -34.99) * mm});
            skArc(sketch, "E29.53.6", {"start": v(-138.31, -34.99) * mm, "mid": v(-138.08, -35.28) * mm, "end": v(-137.72, -35.3) * mm});
            skArc(sketch, "E29.53.7", {"start": v(-136.92, -38.28) * mm, "mid": v(-137.22, -38.5) * mm, "end": v(-137.28, -38.85) * mm});
            skLineSegment(sketch, "E29.53.8", {"start": v(-137.28, -38.85) * mm, "end": v(-137.14, -39.32) * mm});
            skArc(sketch, "E29.54.0", {"start": v(-135.5, -43.04) * mm, "mid": v(-134.35, -41.07) * mm, "end": v(-136.4, -40.09) * mm});
            skLineSegment(sketch, "E29.54.1", {"start": v(-135.69, -44.09) * mm, "end": v(-131, -42.57) * mm, "construction": true});
            skLineSegment(sketch, "E29.54.2", {"start": v(-137.14, -39.32) * mm, "end": v(-132.33, -37.95) * mm});
            skLineSegment(sketch, "E29.54.3", {"start": v(-131, -42.57) * mm, "end": v(-132.33, -37.95) * mm});
            skLineSegment(sketch, "E29.54.4", {"start": v(-131, -42.57) * mm, "end": v(-135.69, -44.09) * mm});
            skLineSegment(sketch, "E29.54.5", {"start": v(-137.14, -39.32) * mm, "end": v(-137, -39.8) * mm});
            skArc(sketch, "E29.54.6", {"start": v(-137, -39.8) * mm, "mid": v(-136.77, -40.08) * mm, "end": v(-136.4, -40.09) * mm});
            skArc(sketch, "E29.54.7", {"start": v(-135.5, -43.04) * mm, "mid": v(-135.8, -43.26) * mm, "end": v(-135.84, -43.62) * mm});
            skLineSegment(sketch, "E29.54.8", {"start": v(-135.84, -43.62) * mm, "end": v(-135.69, -44.09) * mm});
            skArc(sketch, "E29.55.0", {"start": v(-133.91, -47.74) * mm, "mid": v(-132.83, -45.74) * mm, "end": v(-134.92, -44.82) * mm});
            skLineSegment(sketch, "E29.55.1", {"start": v(-134.06, -48.8) * mm, "end": v(-129.44, -47.11) * mm, "construction": true});
            skLineSegment(sketch, "E29.55.2", {"start": v(-135.69, -44.09) * mm, "end": v(-130.93, -42.54) * mm});
            skLineSegment(sketch, "E29.55.3", {"start": v(-129.44, -47.11) * mm, "end": v(-130.93, -42.54) * mm});
            skLineSegment(sketch, "E29.55.4", {"start": v(-129.44, -47.11) * mm, "end": v(-134.06, -48.8) * mm});
            skLineSegment(sketch, "E29.55.5", {"start": v(-135.69, -44.09) * mm, "end": v(-135.53, -44.55) * mm});
            skArc(sketch, "E29.55.6", {"start": v(-135.53, -44.55) * mm, "mid": v(-135.29, -44.82) * mm, "end": v(-134.92, -44.82) * mm});
            skArc(sketch, "E29.55.7", {"start": v(-133.91, -47.74) * mm, "mid": v(-134.2, -47.97) * mm, "end": v(-134.23, -48.34) * mm});
            skLineSegment(sketch, "E29.55.8", {"start": v(-134.23, -48.34) * mm, "end": v(-134.06, -48.8) * mm});
            skArc(sketch, "E29.56.0", {"start": v(-132.17, -52.39) * mm, "mid": v(-131.15, -50.35) * mm, "end": v(-133.27, -49.5) * mm});
            skLineSegment(sketch, "E29.56.1", {"start": v(-132.28, -53.44) * mm, "end": v(-127.72, -51.6) * mm, "construction": true});
            skLineSegment(sketch, "E29.56.2", {"start": v(-134.06, -48.8) * mm, "end": v(-129.36, -47.08) * mm});
            skLineSegment(sketch, "E29.56.3", {"start": v(-127.72, -51.6) * mm, "end": v(-129.36, -47.08) * mm});
            skLineSegment(sketch, "E29.56.4", {"start": v(-127.72, -51.6) * mm, "end": v(-132.28, -53.44) * mm});
            skLineSegment(sketch, "E29.56.5", {"start": v(-134.06, -48.8) * mm, "end": v(-133.9, -49.25) * mm});
            skArc(sketch, "E29.56.6", {"start": v(-133.9, -49.25) * mm, "mid": v(-133.64, -49.52) * mm, "end": v(-133.27, -49.5) * mm});
            skArc(sketch, "E29.56.7", {"start": v(-132.17, -52.39) * mm, "mid": v(-132.45, -52.62) * mm, "end": v(-132.46, -53) * mm});
            skLineSegment(sketch, "E29.56.8", {"start": v(-132.46, -53) * mm, "end": v(-132.28, -53.44) * mm});
            skArc(sketch, "E29.57.0", {"start": v(-130.26, -56.97) * mm, "mid": v(-129.32, -54.9) * mm, "end": v(-131.46, -54.13) * mm});
            skLineSegment(sketch, "E29.57.1", {"start": v(-130.33, -58.03) * mm, "end": v(-125.84, -56.03) * mm, "construction": true});
            skLineSegment(sketch, "E29.57.2", {"start": v(-132.28, -53.44) * mm, "end": v(-127.64, -51.57) * mm});
            skLineSegment(sketch, "E29.57.3", {"start": v(-125.84, -56.03) * mm, "end": v(-127.64, -51.57) * mm});
            skLineSegment(sketch, "E29.57.4", {"start": v(-125.84, -56.03) * mm, "end": v(-130.33, -58.03) * mm});
            skLineSegment(sketch, "E29.57.5", {"start": v(-132.28, -53.44) * mm, "end": v(-132.1, -53.9) * mm});
            skArc(sketch, "E29.57.6", {"start": v(-132.1, -53.9) * mm, "mid": v(-131.83, -54.15) * mm, "end": v(-131.46, -54.13) * mm});
            skArc(sketch, "E29.57.7", {"start": v(-130.26, -56.97) * mm, "mid": v(-130.53, -57.21) * mm, "end": v(-130.53, -57.58) * mm});
            skLineSegment(sketch, "E29.57.8", {"start": v(-130.53, -57.58) * mm, "end": v(-130.33, -58.03) * mm});
            skArc(sketch, "E29.58.0", {"start": v(-128.2, -61.48) * mm, "mid": v(-127.32, -59.37) * mm, "end": v(-129.5, -58.68) * mm});
            skLineSegment(sketch, "E29.58.1", {"start": v(-128.23, -62.54) * mm, "end": v(-123.8, -60.39) * mm, "construction": true});
            skLineSegment(sketch, "E29.58.2", {"start": v(-130.33, -58.03) * mm, "end": v(-125.76, -56) * mm});
            skLineSegment(sketch, "E29.58.3", {"start": v(-123.8, -60.39) * mm, "end": v(-125.76, -56) * mm});
            skLineSegment(sketch, "E29.58.4", {"start": v(-123.8, -60.39) * mm, "end": v(-128.23, -62.54) * mm});
            skLineSegment(sketch, "E29.58.5", {"start": v(-130.33, -58.03) * mm, "end": v(-130.13, -58.47) * mm});
            skArc(sketch, "E29.58.6", {"start": v(-130.13, -58.47) * mm, "mid": v(-129.86, -58.72) * mm, "end": v(-129.5, -58.68) * mm});
            skArc(sketch, "E29.58.7", {"start": v(-128.2, -61.48) * mm, "mid": v(-128.45, -61.73) * mm, "end": v(-128.44, -62.1) * mm});
            skLineSegment(sketch, "E29.58.8", {"start": v(-128.44, -62.1) * mm, "end": v(-128.23, -62.54) * mm});
            skArc(sketch, "E29.59.0", {"start": v(-125.97, -65.91) * mm, "mid": v(-125.17, -63.78) * mm, "end": v(-127.37, -63.17) * mm});
            skLineSegment(sketch, "E29.59.1", {"start": v(-125.97, -66.98) * mm, "end": v(-121.63, -64.67) * mm, "construction": true});
            skLineSegment(sketch, "E29.59.2", {"start": v(-128.23, -62.54) * mm, "end": v(-123.73, -60.35) * mm});
            skLineSegment(sketch, "E29.59.3", {"start": v(-121.63, -64.67) * mm, "end": v(-123.73, -60.35) * mm});
            skLineSegment(sketch, "E29.59.4", {"start": v(-121.63, -64.67) * mm, "end": v(-125.97, -66.98) * mm});
            skLineSegment(sketch, "E29.59.5", {"start": v(-128.23, -62.54) * mm, "end": v(-128.01, -62.98) * mm});
            skArc(sketch, "E29.59.6", {"start": v(-128.01, -62.98) * mm, "mid": v(-127.73, -63.22) * mm, "end": v(-127.37, -63.17) * mm});
            skArc(sketch, "E29.59.7", {"start": v(-125.97, -65.91) * mm, "mid": v(-126.22, -66.18) * mm, "end": v(-126.2, -66.55) * mm});
            skLineSegment(sketch, "E29.59.8", {"start": v(-126.2, -66.55) * mm, "end": v(-125.97, -66.98) * mm});
            skArc(sketch, "E29.60.0", {"start": v(-123.59, -70.27) * mm, "mid": v(-122.87, -68.1) * mm, "end": v(-125.09, -67.57) * mm});
            skLineSegment(sketch, "E29.60.1", {"start": v(-123.55, -71.33) * mm, "end": v(-119.3, -68.87) * mm, "construction": true});
            skLineSegment(sketch, "E29.60.2", {"start": v(-125.97, -66.98) * mm, "end": v(-121.55, -64.63) * mm});
            skLineSegment(sketch, "E29.60.3", {"start": v(-119.3, -68.87) * mm, "end": v(-121.55, -64.63) * mm});
            skLineSegment(sketch, "E29.60.4", {"start": v(-119.3, -68.87) * mm, "end": v(-123.55, -71.33) * mm});
            skLineSegment(sketch, "E29.60.5", {"start": v(-125.97, -66.98) * mm, "end": v(-125.74, -67.4) * mm});
            skArc(sketch, "E29.60.6", {"start": v(-125.74, -67.4) * mm, "mid": v(-125.45, -67.64) * mm, "end": v(-125.09, -67.57) * mm});
            skArc(sketch, "E29.60.7", {"start": v(-123.59, -70.27) * mm, "mid": v(-123.84, -70.54) * mm, "end": v(-123.8, -70.91) * mm});
            skLineSegment(sketch, "E29.60.8", {"start": v(-123.8, -70.91) * mm, "end": v(-123.55, -71.33) * mm});
            skArc(sketch, "E29.61.0", {"start": v(-121.06, -74.54) * mm, "mid": v(-120.42, -72.35) * mm, "end": v(-122.65, -71.9) * mm});
            skLineSegment(sketch, "E29.61.1", {"start": v(-120.99, -75.6) * mm, "end": v(-116.82, -73) * mm, "construction": true});
            skLineSegment(sketch, "E29.61.2", {"start": v(-123.55, -71.33) * mm, "end": v(-119.22, -68.83) * mm});
            skLineSegment(sketch, "E29.61.3", {"start": v(-116.82, -73) * mm, "end": v(-119.22, -68.83) * mm});
            skLineSegment(sketch, "E29.61.4", {"start": v(-116.82, -73) * mm, "end": v(-120.99, -75.6) * mm});
            skLineSegment(sketch, "E29.61.5", {"start": v(-123.55, -71.33) * mm, "end": v(-123.3, -71.76) * mm});
            skArc(sketch, "E29.61.6", {"start": v(-123.3, -71.76) * mm, "mid": v(-123.01, -71.97) * mm, "end": v(-122.65, -71.9) * mm});
            skArc(sketch, "E29.61.7", {"start": v(-121.06, -74.54) * mm, "mid": v(-121.3, -74.82) * mm, "end": v(-121.25, -75.19) * mm});
            skLineSegment(sketch, "E29.61.8", {"start": v(-121.25, -75.19) * mm, "end": v(-120.99, -75.6) * mm});
            skArc(sketch, "E29.62.0", {"start": v(-118.39, -78.72) * mm, "mid": v(-117.82, -76.51) * mm, "end": v(-120.07, -76.13) * mm});
            skLineSegment(sketch, "E29.62.1", {"start": v(-118.28, -79.78) * mm, "end": v(-114.2, -77.03) * mm, "construction": true});
            skLineSegment(sketch, "E29.62.2", {"start": v(-120.99, -75.6) * mm, "end": v(-116.75, -72.95) * mm});
            skLineSegment(sketch, "E29.62.3", {"start": v(-114.2, -77.03) * mm, "end": v(-116.75, -72.95) * mm});
            skLineSegment(sketch, "E29.62.4", {"start": v(-114.2, -77.03) * mm, "end": v(-118.28, -79.78) * mm});
            skLineSegment(sketch, "E29.62.5", {"start": v(-120.99, -75.6) * mm, "end": v(-120.73, -76.02) * mm});
            skArc(sketch, "E29.62.6", {"start": v(-120.73, -76.02) * mm, "mid": v(-120.42, -76.22) * mm, "end": v(-120.07, -76.13) * mm});
            skArc(sketch, "E29.62.7", {"start": v(-118.39, -78.72) * mm, "mid": v(-118.61, -79.01) * mm, "end": v(-118.55, -79.37) * mm});
            skLineSegment(sketch, "E29.62.8", {"start": v(-118.55, -79.37) * mm, "end": v(-118.28, -79.78) * mm});
            skArc(sketch, "E29.63.0", {"start": v(-115.57, -82.8) * mm, "mid": v(-115.08, -80.58) * mm, "end": v(-117.34, -80.28) * mm});
            skLineSegment(sketch, "E29.63.1", {"start": v(-115.42, -83.86) * mm, "end": v(-111.44, -80.97) * mm, "construction": true});
            skLineSegment(sketch, "E29.63.2", {"start": v(-118.28, -79.78) * mm, "end": v(-114.13, -76.98) * mm});
            skLineSegment(sketch, "E29.63.3", {"start": v(-111.44, -80.97) * mm, "end": v(-114.13, -76.98) * mm});
            skLineSegment(sketch, "E29.63.4", {"start": v(-111.44, -80.97) * mm, "end": v(-115.42, -83.86) * mm});
            skLineSegment(sketch, "E29.63.5", {"start": v(-118.28, -79.78) * mm, "end": v(-118, -80.18) * mm});
            skArc(sketch, "E29.63.6", {"start": v(-118, -80.18) * mm, "mid": v(-117.7, -80.38) * mm, "end": v(-117.34, -80.28) * mm});
            skArc(sketch, "E29.63.7", {"start": v(-115.57, -82.8) * mm, "mid": v(-115.78, -83.1) * mm, "end": v(-115.7, -83.46) * mm});
            skLineSegment(sketch, "E29.63.8", {"start": v(-115.7, -83.46) * mm, "end": v(-115.42, -83.86) * mm});
            skArc(sketch, "E29.64.0", {"start": v(-112.6, -86.79) * mm, "mid": v(-112.2, -84.55) * mm, "end": v(-114.46, -84.32) * mm});
            skLineSegment(sketch, "E29.64.1", {"start": v(-112.42, -87.84) * mm, "end": v(-108.55, -84.8) * mm, "construction": true});
            skLineSegment(sketch, "E29.64.2", {"start": v(-115.42, -83.86) * mm, "end": v(-111.37, -80.92) * mm});
            skLineSegment(sketch, "E29.64.3", {"start": v(-108.55, -84.8) * mm, "end": v(-111.37, -80.92) * mm});
            skLineSegment(sketch, "E29.64.4", {"start": v(-108.55, -84.8) * mm, "end": v(-112.42, -87.84) * mm});
            skLineSegment(sketch, "E29.64.5", {"start": v(-115.42, -83.86) * mm, "end": v(-115.13, -84.25) * mm});
            skArc(sketch, "E29.64.6", {"start": v(-115.13, -84.25) * mm, "mid": v(-114.81, -84.44) * mm, "end": v(-114.46, -84.32) * mm});
            skArc(sketch, "E29.64.7", {"start": v(-112.6, -86.79) * mm, "mid": v(-112.81, -87.1) * mm, "end": v(-112.72, -87.45) * mm});
            skLineSegment(sketch, "E29.64.8", {"start": v(-112.72, -87.45) * mm, "end": v(-112.42, -87.84) * mm});
            skArc(sketch, "E29.65.0", {"start": v(-109.5, -90.66) * mm, "mid": v(-109.18, -88.4) * mm, "end": v(-111.45, -88.27) * mm});
            skLineSegment(sketch, "E29.65.1", {"start": v(-109.29, -91.7) * mm, "end": v(-105.52, -88.54) * mm, "construction": true});
            skLineSegment(sketch, "E29.65.2", {"start": v(-112.42, -87.84) * mm, "end": v(-108.48, -84.76) * mm});
            skLineSegment(sketch, "E29.65.3", {"start": v(-105.52, -88.54) * mm, "end": v(-108.48, -84.76) * mm});
            skLineSegment(sketch, "E29.65.4", {"start": v(-105.52, -88.54) * mm, "end": v(-109.29, -91.7) * mm});
            skLineSegment(sketch, "E29.65.5", {"start": v(-112.42, -87.84) * mm, "end": v(-112.12, -88.22) * mm});
            skArc(sketch, "E29.65.6", {"start": v(-112.12, -88.22) * mm, "mid": v(-111.8, -88.4) * mm, "end": v(-111.45, -88.27) * mm});
            skArc(sketch, "E29.65.7", {"start": v(-109.5, -90.66) * mm, "mid": v(-109.7, -90.98) * mm, "end": v(-109.6, -91.33) * mm});
            skLineSegment(sketch, "E29.65.8", {"start": v(-109.6, -91.33) * mm, "end": v(-109.29, -91.7) * mm});
            skArc(sketch, "E29.66.0", {"start": v(-106.28, -94.43) * mm, "mid": v(-106.02, -92.17) * mm, "end": v(-108.3, -92.1) * mm});
            skLineSegment(sketch, "E29.66.1", {"start": v(-106.02, -95.46) * mm, "end": v(-102.37, -92.17) * mm, "construction": true});
            skLineSegment(sketch, "E29.66.2", {"start": v(-109.3, -91.7) * mm, "end": v(-105.46, -88.49) * mm});
            skLineSegment(sketch, "E29.66.3", {"start": v(-102.37, -92.17) * mm, "end": v(-105.46, -88.49) * mm});
            skLineSegment(sketch, "E29.66.4", {"start": v(-102.37, -92.17) * mm, "end": v(-106.02, -95.46) * mm});
            skLineSegment(sketch, "E29.66.5", {"start": v(-109.3, -91.7) * mm, "end": v(-108.98, -92.08) * mm});
            skArc(sketch, "E29.66.6", {"start": v(-108.98, -92.08) * mm, "mid": v(-108.64, -92.24) * mm, "end": v(-108.3, -92.1) * mm});
            skArc(sketch, "E29.66.7", {"start": v(-106.28, -94.43) * mm, "mid": v(-106.46, -94.75) * mm, "end": v(-106.35, -95.1) * mm});
            skLineSegment(sketch, "E29.66.8", {"start": v(-106.35, -95.1) * mm, "end": v(-106.02, -95.46) * mm});
            skArc(sketch, "E29.67.0", {"start": v(-102.92, -98.08) * mm, "mid": v(-102.74, -95.81) * mm, "end": v(-105.02, -95.83) * mm});
            skLineSegment(sketch, "E29.67.1", {"start": v(-102.63, -99.1) * mm, "end": v(-99.09, -95.69) * mm, "construction": true});
            skLineSegment(sketch, "E29.67.2", {"start": v(-106.02, -95.46) * mm, "end": v(-102.3, -92.12) * mm});
            skLineSegment(sketch, "E29.67.3", {"start": v(-99.09, -95.69) * mm, "end": v(-102.3, -92.12) * mm});
            skLineSegment(sketch, "E29.67.4", {"start": v(-99.09, -95.69) * mm, "end": v(-102.63, -99.1) * mm});
            skLineSegment(sketch, "E29.67.5", {"start": v(-106.02, -95.46) * mm, "end": v(-105.7, -95.83) * mm});
            skArc(sketch, "E29.67.6", {"start": v(-105.7, -95.83) * mm, "mid": v(-105.36, -95.97) * mm, "end": v(-105.02, -95.83) * mm});
            skArc(sketch, "E29.67.7", {"start": v(-102.92, -98.08) * mm, "mid": v(-103.1, -98.4) * mm, "end": v(-102.97, -98.75) * mm});
            skLineSegment(sketch, "E29.67.8", {"start": v(-102.97, -98.75) * mm, "end": v(-102.63, -99.1) * mm});
            skArc(sketch, "E29.68.0", {"start": v(-99.43, -101.61) * mm, "mid": v(-99.34, -99.34) * mm, "end": v(-101.61, -99.43) * mm});
            skLineSegment(sketch, "E29.68.1", {"start": v(-99.1, -102.63) * mm, "end": v(-95.69, -99.09) * mm, "construction": true});
            skLineSegment(sketch, "E29.68.2", {"start": v(-102.63, -99.1) * mm, "end": v(-99.03, -95.63) * mm});
            skLineSegment(sketch, "E29.68.3", {"start": v(-95.69, -99.09) * mm, "end": v(-99.03, -95.63) * mm});
            skLineSegment(sketch, "E29.68.4", {"start": v(-95.69, -99.09) * mm, "end": v(-99.1, -102.63) * mm});
            skLineSegment(sketch, "E29.68.5", {"start": v(-102.63, -99.1) * mm, "end": v(-102.29, -99.46) * mm});
            skArc(sketch, "E29.68.6", {"start": v(-102.29, -99.46) * mm, "mid": v(-101.95, -99.6) * mm, "end": v(-101.61, -99.43) * mm});
            skArc(sketch, "E29.68.7", {"start": v(-99.43, -101.61) * mm, "mid": v(-99.6, -101.95) * mm, "end": v(-99.46, -102.29) * mm});
            skLineSegment(sketch, "E29.68.8", {"start": v(-99.46, -102.29) * mm, "end": v(-99.1, -102.63) * mm});
            skArc(sketch, "E29.69.0", {"start": v(-95.83, -105.02) * mm, "mid": v(-95.81, -102.74) * mm, "end": v(-98.08, -102.92) * mm});
            skLineSegment(sketch, "E29.69.1", {"start": v(-95.46, -106.02) * mm, "end": v(-92.17, -102.37) * mm, "construction": true});
            skLineSegment(sketch, "E29.69.2", {"start": v(-99.1, -102.63) * mm, "end": v(-95.63, -99.03) * mm});
            skLineSegment(sketch, "E29.69.3", {"start": v(-92.17, -102.37) * mm, "end": v(-95.63, -99.03) * mm});
            skLineSegment(sketch, "E29.69.4", {"start": v(-92.17, -102.37) * mm, "end": v(-95.46, -106.02) * mm});
            skLineSegment(sketch, "E29.69.5", {"start": v(-99.1, -102.63) * mm, "end": v(-98.75, -102.97) * mm});
            skArc(sketch, "E29.69.6", {"start": v(-98.75, -102.97) * mm, "mid": v(-98.4, -103.1) * mm, "end": v(-98.08, -102.92) * mm});
            skArc(sketch, "E29.69.7", {"start": v(-95.83, -105.02) * mm, "mid": v(-95.97, -105.36) * mm, "end": v(-95.83, -105.7) * mm});
            skLineSegment(sketch, "E29.69.8", {"start": v(-95.83, -105.7) * mm, "end": v(-95.46, -106.02) * mm});
            skArc(sketch, "E29.70.0", {"start": v(-92.1, -108.3) * mm, "mid": v(-92.17, -106.02) * mm, "end": v(-94.43, -106.28) * mm});
            skLineSegment(sketch, "E29.70.1", {"start": v(-91.7, -109.29) * mm, "end": v(-88.54, -105.52) * mm, "construction": true});
            skLineSegment(sketch, "E29.70.2", {"start": v(-95.46, -106.02) * mm, "end": v(-92.12, -102.3) * mm});
            skLineSegment(sketch, "E29.70.3", {"start": v(-88.54, -105.52) * mm, "end": v(-92.12, -102.3) * mm});
            skLineSegment(sketch, "E29.70.4", {"start": v(-88.54, -105.52) * mm, "end": v(-91.7, -109.29) * mm});
            skLineSegment(sketch, "E29.70.5", {"start": v(-95.46, -106.02) * mm, "end": v(-95.1, -106.35) * mm});
            skArc(sketch, "E29.70.6", {"start": v(-95.1, -106.35) * mm, "mid": v(-94.75, -106.46) * mm, "end": v(-94.43, -106.28) * mm});
            skArc(sketch, "E29.70.7", {"start": v(-92.1, -108.3) * mm, "mid": v(-92.24, -108.64) * mm, "end": v(-92.08, -108.98) * mm});
            skLineSegment(sketch, "E29.70.8", {"start": v(-92.08, -108.98) * mm, "end": v(-91.7, -109.29) * mm});
            skArc(sketch, "E29.71.0", {"start": v(-88.27, -111.45) * mm, "mid": v(-88.4, -109.18) * mm, "end": v(-90.66, -109.5) * mm});
            skLineSegment(sketch, "E29.71.1", {"start": v(-87.84, -112.42) * mm, "end": v(-84.8, -108.55) * mm, "construction": true});
            skLineSegment(sketch, "E29.71.2", {"start": v(-91.7, -109.3) * mm, "end": v(-88.49, -105.46) * mm});
            skLineSegment(sketch, "E29.71.3", {"start": v(-84.8, -108.55) * mm, "end": v(-88.49, -105.46) * mm});
            skLineSegment(sketch, "E29.71.4", {"start": v(-84.8, -108.55) * mm, "end": v(-87.84, -112.42) * mm});
            skLineSegment(sketch, "E29.71.5", {"start": v(-91.7, -109.3) * mm, "end": v(-91.33, -109.6) * mm});
            skArc(sketch, "E29.71.6", {"start": v(-91.33, -109.6) * mm, "mid": v(-90.98, -109.7) * mm, "end": v(-90.66, -109.5) * mm});
            skArc(sketch, "E29.71.7", {"start": v(-88.27, -111.45) * mm, "mid": v(-88.4, -111.8) * mm, "end": v(-88.22, -112.12) * mm});
            skLineSegment(sketch, "E29.71.8", {"start": v(-88.22, -112.12) * mm, "end": v(-87.84, -112.42) * mm});
            skArc(sketch, "E29.72.0", {"start": v(-84.32, -114.46) * mm, "mid": v(-84.55, -112.2) * mm, "end": v(-86.79, -112.6) * mm});
            skLineSegment(sketch, "E29.72.1", {"start": v(-83.86, -115.42) * mm, "end": v(-80.97, -111.44) * mm, "construction": true});
            skLineSegment(sketch, "E29.72.2", {"start": v(-87.84, -112.42) * mm, "end": v(-84.76, -108.48) * mm});
            skLineSegment(sketch, "E29.72.3", {"start": v(-80.97, -111.44) * mm, "end": v(-84.76, -108.48) * mm});
            skLineSegment(sketch, "E29.72.4", {"start": v(-80.97, -111.44) * mm, "end": v(-83.86, -115.42) * mm});
            skLineSegment(sketch, "E29.72.5", {"start": v(-87.84, -112.42) * mm, "end": v(-87.45, -112.72) * mm});
            skArc(sketch, "E29.72.6", {"start": v(-87.45, -112.72) * mm, "mid": v(-87.1, -112.81) * mm, "end": v(-86.79, -112.6) * mm});
            skArc(sketch, "E29.72.7", {"start": v(-84.32, -114.46) * mm, "mid": v(-84.44, -114.81) * mm, "end": v(-84.25, -115.13) * mm});
            skLineSegment(sketch, "E29.72.8", {"start": v(-84.25, -115.13) * mm, "end": v(-83.86, -115.42) * mm});
            skArc(sketch, "E29.73.0", {"start": v(-80.28, -117.34) * mm, "mid": v(-80.58, -115.08) * mm, "end": v(-82.8, -115.57) * mm});
            skLineSegment(sketch, "E29.73.1", {"start": v(-79.78, -118.28) * mm, "end": v(-77.03, -114.2) * mm, "construction": true});
            skLineSegment(sketch, "E29.73.2", {"start": v(-83.86, -115.42) * mm, "end": v(-80.92, -111.37) * mm});
            skLineSegment(sketch, "E29.73.3", {"start": v(-77.03, -114.2) * mm, "end": v(-80.92, -111.37) * mm});
            skLineSegment(sketch, "E29.73.4", {"start": v(-77.03, -114.2) * mm, "end": v(-79.78, -118.28) * mm});
            skLineSegment(sketch, "E29.73.5", {"start": v(-83.86, -115.42) * mm, "end": v(-83.46, -115.7) * mm});
            skArc(sketch, "E29.73.6", {"start": v(-83.46, -115.7) * mm, "mid": v(-83.1, -115.78) * mm, "end": v(-82.8, -115.57) * mm});
            skArc(sketch, "E29.73.7", {"start": v(-80.28, -117.34) * mm, "mid": v(-80.38, -117.7) * mm, "end": v(-80.18, -118) * mm});
            skLineSegment(sketch, "E29.73.8", {"start": v(-80.18, -118) * mm, "end": v(-79.78, -118.28) * mm});
            skArc(sketch, "E29.74.0", {"start": v(-76.13, -120.07) * mm, "mid": v(-76.51, -117.82) * mm, "end": v(-78.72, -118.39) * mm});
            skLineSegment(sketch, "E29.74.1", {"start": v(-75.6, -120.99) * mm, "end": v(-73, -116.82) * mm, "construction": true});
            skLineSegment(sketch, "E29.74.2", {"start": v(-79.78, -118.28) * mm, "end": v(-76.98, -114.13) * mm});
            skLineSegment(sketch, "E29.74.3", {"start": v(-73, -116.82) * mm, "end": v(-76.98, -114.13) * mm});
            skLineSegment(sketch, "E29.74.4", {"start": v(-73, -116.82) * mm, "end": v(-75.6, -120.99) * mm});
            skLineSegment(sketch, "E29.74.5", {"start": v(-79.78, -118.28) * mm, "end": v(-79.37, -118.55) * mm});
            skArc(sketch, "E29.74.6", {"start": v(-79.37, -118.55) * mm, "mid": v(-79.01, -118.61) * mm, "end": v(-78.72, -118.39) * mm});
            skArc(sketch, "E29.74.7", {"start": v(-76.13, -120.07) * mm, "mid": v(-76.22, -120.42) * mm, "end": v(-76.02, -120.73) * mm});
            skLineSegment(sketch, "E29.74.8", {"start": v(-76.02, -120.73) * mm, "end": v(-75.6, -120.99) * mm});
            skArc(sketch, "E29.75.0", {"start": v(-71.9, -122.65) * mm, "mid": v(-72.35, -120.42) * mm, "end": v(-74.54, -121.06) * mm});
            skLineSegment(sketch, "E29.75.1", {"start": v(-71.33, -123.55) * mm, "end": v(-68.87, -119.3) * mm, "construction": true});
            skLineSegment(sketch, "E29.75.2", {"start": v(-75.6, -120.99) * mm, "end": v(-72.95, -116.75) * mm});
            skLineSegment(sketch, "E29.75.3", {"start": v(-68.87, -119.3) * mm, "end": v(-72.95, -116.75) * mm});
            skLineSegment(sketch, "E29.75.4", {"start": v(-68.87, -119.3) * mm, "end": v(-71.33, -123.55) * mm});
            skLineSegment(sketch, "E29.75.5", {"start": v(-75.6, -120.99) * mm, "end": v(-75.19, -121.25) * mm});
            skArc(sketch, "E29.75.6", {"start": v(-75.19, -121.25) * mm, "mid": v(-74.82, -121.3) * mm, "end": v(-74.54, -121.06) * mm});
            skArc(sketch, "E29.75.7", {"start": v(-71.9, -122.65) * mm, "mid": v(-71.97, -123.01) * mm, "end": v(-71.76, -123.3) * mm});
            skLineSegment(sketch, "E29.75.8", {"start": v(-71.76, -123.3) * mm, "end": v(-71.33, -123.55) * mm});
            skArc(sketch, "E29.76.0", {"start": v(-67.57, -125.09) * mm, "mid": v(-68.1, -122.87) * mm, "end": v(-70.27, -123.59) * mm});
            skLineSegment(sketch, "E29.76.1", {"start": v(-66.98, -125.97) * mm, "end": v(-64.67, -121.63) * mm, "construction": true});
            skLineSegment(sketch, "E29.76.2", {"start": v(-71.33, -123.55) * mm, "end": v(-68.83, -119.22) * mm});
            skLineSegment(sketch, "E29.76.3", {"start": v(-64.67, -121.63) * mm, "end": v(-68.83, -119.22) * mm});
            skLineSegment(sketch, "E29.76.4", {"start": v(-64.67, -121.63) * mm, "end": v(-66.98, -125.97) * mm});
            skLineSegment(sketch, "E29.76.5", {"start": v(-71.33, -123.55) * mm, "end": v(-70.91, -123.8) * mm});
            skArc(sketch, "E29.76.6", {"start": v(-70.91, -123.8) * mm, "mid": v(-70.54, -123.84) * mm, "end": v(-70.27, -123.59) * mm});
            skArc(sketch, "E29.76.7", {"start": v(-67.57, -125.09) * mm, "mid": v(-67.64, -125.45) * mm, "end": v(-67.4, -125.74) * mm});
            skLineSegment(sketch, "E29.76.8", {"start": v(-67.4, -125.74) * mm, "end": v(-66.98, -125.97) * mm});
            skArc(sketch, "E29.77.0", {"start": v(-63.17, -127.37) * mm, "mid": v(-63.78, -125.17) * mm, "end": v(-65.91, -125.97) * mm});
            skLineSegment(sketch, "E29.77.1", {"start": v(-62.54, -128.23) * mm, "end": v(-60.39, -123.8) * mm, "construction": true});
            skLineSegment(sketch, "E29.77.2", {"start": v(-66.98, -125.97) * mm, "end": v(-64.63, -121.55) * mm});
            skLineSegment(sketch, "E29.77.3", {"start": v(-60.39, -123.8) * mm, "end": v(-64.63, -121.55) * mm});
            skLineSegment(sketch, "E29.77.4", {"start": v(-60.39, -123.8) * mm, "end": v(-62.54, -128.23) * mm});
            skLineSegment(sketch, "E29.77.5", {"start": v(-66.98, -125.97) * mm, "end": v(-66.55, -126.2) * mm});
            skArc(sketch, "E29.77.6", {"start": v(-66.55, -126.2) * mm, "mid": v(-66.18, -126.22) * mm, "end": v(-65.91, -125.97) * mm});
            skArc(sketch, "E29.77.7", {"start": v(-63.17, -127.37) * mm, "mid": v(-63.22, -127.73) * mm, "end": v(-62.98, -128.01) * mm});
            skLineSegment(sketch, "E29.77.8", {"start": v(-62.98, -128.01) * mm, "end": v(-62.54, -128.23) * mm});
            skArc(sketch, "E29.78.0", {"start": v(-58.68, -129.5) * mm, "mid": v(-59.37, -127.32) * mm, "end": v(-61.48, -128.2) * mm});
            skLineSegment(sketch, "E29.78.1", {"start": v(-58.03, -130.33) * mm, "end": v(-56.03, -125.84) * mm, "construction": true});
            skLineSegment(sketch, "E29.78.2", {"start": v(-62.54, -128.23) * mm, "end": v(-60.35, -123.73) * mm});
            skLineSegment(sketch, "E29.78.3", {"start": v(-56.03, -125.84) * mm, "end": v(-60.35, -123.73) * mm});
            skLineSegment(sketch, "E29.78.4", {"start": v(-56.03, -125.84) * mm, "end": v(-58.03, -130.33) * mm});
            skLineSegment(sketch, "E29.78.5", {"start": v(-62.54, -128.23) * mm, "end": v(-62.1, -128.44) * mm});
            skArc(sketch, "E29.78.6", {"start": v(-62.1, -128.44) * mm, "mid": v(-61.73, -128.45) * mm, "end": v(-61.48, -128.2) * mm});
            skArc(sketch, "E29.78.7", {"start": v(-58.68, -129.5) * mm, "mid": v(-58.72, -129.86) * mm, "end": v(-58.47, -130.13) * mm});
            skLineSegment(sketch, "E29.78.8", {"start": v(-58.47, -130.13) * mm, "end": v(-58.03, -130.33) * mm});
            skArc(sketch, "E29.79.0", {"start": v(-54.13, -131.46) * mm, "mid": v(-54.9, -129.32) * mm, "end": v(-56.97, -130.26) * mm});
            skLineSegment(sketch, "E29.79.1", {"start": v(-53.44, -132.28) * mm, "end": v(-51.6, -127.72) * mm, "construction": true});
            skLineSegment(sketch, "E29.79.2", {"start": v(-58.03, -130.33) * mm, "end": v(-56, -125.76) * mm});
            skLineSegment(sketch, "E29.79.3", {"start": v(-51.6, -127.72) * mm, "end": v(-56, -125.76) * mm});
            skLineSegment(sketch, "E29.79.4", {"start": v(-51.6, -127.72) * mm, "end": v(-53.44, -132.28) * mm});
            skLineSegment(sketch, "E29.79.5", {"start": v(-58.03, -130.33) * mm, "end": v(-57.58, -130.53) * mm});
            skArc(sketch, "E29.79.6", {"start": v(-57.58, -130.53) * mm, "mid": v(-57.21, -130.53) * mm, "end": v(-56.97, -130.26) * mm});
            skArc(sketch, "E29.79.7", {"start": v(-54.13, -131.46) * mm, "mid": v(-54.15, -131.83) * mm, "end": v(-53.9, -132.1) * mm});
            skLineSegment(sketch, "E29.79.8", {"start": v(-53.9, -132.1) * mm, "end": v(-53.44, -132.28) * mm});
            skArc(sketch, "E29.80.0", {"start": v(-49.5, -133.27) * mm, "mid": v(-50.35, -131.15) * mm, "end": v(-52.39, -132.17) * mm});
            skLineSegment(sketch, "E29.80.1", {"start": v(-48.8, -134.06) * mm, "end": v(-47.11, -129.44) * mm, "construction": true});
            skLineSegment(sketch, "E29.80.2", {"start": v(-53.44, -132.28) * mm, "end": v(-51.57, -127.64) * mm});
            skLineSegment(sketch, "E29.80.3", {"start": v(-47.11, -129.44) * mm, "end": v(-51.57, -127.64) * mm});
            skLineSegment(sketch, "E29.80.4", {"start": v(-47.11, -129.44) * mm, "end": v(-48.8, -134.06) * mm});
            skLineSegment(sketch, "E29.80.5", {"start": v(-53.44, -132.28) * mm, "end": v(-53, -132.46) * mm});
            skArc(sketch, "E29.80.6", {"start": v(-53, -132.46) * mm, "mid": v(-52.62, -132.45) * mm, "end": v(-52.39, -132.17) * mm});
            skArc(sketch, "E29.80.7", {"start": v(-49.5, -133.27) * mm, "mid": v(-49.52, -133.64) * mm, "end": v(-49.25, -133.9) * mm});
            skLineSegment(sketch, "E29.80.8", {"start": v(-49.25, -133.9) * mm, "end": v(-48.8, -134.06) * mm});
            skArc(sketch, "E29.81.0", {"start": v(-44.82, -134.92) * mm, "mid": v(-45.74, -132.83) * mm, "end": v(-47.74, -133.91) * mm});
            skLineSegment(sketch, "E29.81.1", {"start": v(-44.09, -135.69) * mm, "end": v(-42.57, -131) * mm, "construction": true});
            skLineSegment(sketch, "E29.81.2", {"start": v(-48.8, -134.06) * mm, "end": v(-47.08, -129.36) * mm});
            skLineSegment(sketch, "E29.81.3", {"start": v(-42.57, -131) * mm, "end": v(-47.08, -129.36) * mm});
            skLineSegment(sketch, "E29.81.4", {"start": v(-42.57, -131) * mm, "end": v(-44.09, -135.69) * mm});
            skLineSegment(sketch, "E29.81.5", {"start": v(-48.8, -134.06) * mm, "end": v(-48.34, -134.23) * mm});
            skArc(sketch, "E29.81.6", {"start": v(-48.34, -134.23) * mm, "mid": v(-47.97, -134.2) * mm, "end": v(-47.74, -133.91) * mm});
            skArc(sketch, "E29.81.7", {"start": v(-44.82, -134.92) * mm, "mid": v(-44.82, -135.29) * mm, "end": v(-44.55, -135.53) * mm});
            skLineSegment(sketch, "E29.81.8", {"start": v(-44.55, -135.53) * mm, "end": v(-44.09, -135.69) * mm});
            skArc(sketch, "E29.82.0", {"start": v(-40.09, -136.4) * mm, "mid": v(-41.07, -134.35) * mm, "end": v(-43.04, -135.5) * mm});
            skLineSegment(sketch, "E29.82.1", {"start": v(-39.32, -137.14) * mm, "end": v(-37.97, -132.41) * mm, "construction": true});
            skLineSegment(sketch, "E29.82.2", {"start": v(-44.09, -135.69) * mm, "end": v(-42.54, -130.93) * mm});
            skLineSegment(sketch, "E29.82.3", {"start": v(-37.97, -132.41) * mm, "end": v(-42.54, -130.93) * mm});
            skLineSegment(sketch, "E29.82.4", {"start": v(-37.97, -132.41) * mm, "end": v(-39.32, -137.14) * mm});
            skLineSegment(sketch, "E29.82.5", {"start": v(-44.09, -135.69) * mm, "end": v(-43.62, -135.84) * mm});
            skArc(sketch, "E29.82.6", {"start": v(-43.62, -135.84) * mm, "mid": v(-43.26, -135.8) * mm, "end": v(-43.04, -135.5) * mm});
            skArc(sketch, "E29.82.7", {"start": v(-40.09, -136.4) * mm, "mid": v(-40.08, -136.77) * mm, "end": v(-39.8, -137) * mm});
            skLineSegment(sketch, "E29.82.8", {"start": v(-39.8, -137) * mm, "end": v(-39.32, -137.14) * mm});
            skArc(sketch, "E29.83.0", {"start": v(-35.3, -137.72) * mm, "mid": v(-36.36, -135.7) * mm, "end": v(-38.28, -136.92) * mm});
            skLineSegment(sketch, "E29.83.1", {"start": v(-34.51, -138.43) * mm, "end": v(-33.32, -133.66) * mm, "construction": true});
            skLineSegment(sketch, "E29.83.2", {"start": v(-39.32, -137.14) * mm, "end": v(-37.95, -132.33) * mm});
            skLineSegment(sketch, "E29.83.3", {"start": v(-33.32, -133.66) * mm, "end": v(-37.95, -132.33) * mm});
            skLineSegment(sketch, "E29.83.4", {"start": v(-33.32, -133.66) * mm, "end": v(-34.51, -138.43) * mm});
            skLineSegment(sketch, "E29.83.5", {"start": v(-39.32, -137.14) * mm, "end": v(-38.85, -137.28) * mm});
            skArc(sketch, "E29.83.6", {"start": v(-38.85, -137.28) * mm, "mid": v(-38.5, -137.22) * mm, "end": v(-38.28, -136.92) * mm});
            skArc(sketch, "E29.83.7", {"start": v(-35.3, -137.72) * mm, "mid": v(-35.28, -138.08) * mm, "end": v(-34.99, -138.31) * mm});
            skLineSegment(sketch, "E29.83.8", {"start": v(-34.99, -138.31) * mm, "end": v(-34.51, -138.43) * mm});
            skArc(sketch, "E29.84.0", {"start": v(-30.48, -138.87) * mm, "mid": v(-31.6, -136.88) * mm, "end": v(-33.48, -138.17) * mm});
            skLineSegment(sketch, "E29.84.1", {"start": v(-29.66, -139.55) * mm, "end": v(-28.64, -134.74) * mm, "construction": true});
            skLineSegment(sketch, "E29.84.2", {"start": v(-34.51, -138.43) * mm, "end": v(-33.3, -133.58) * mm});
            skLineSegment(sketch, "E29.84.3", {"start": v(-28.64, -134.74) * mm, "end": v(-33.3, -133.58) * mm});
            skLineSegment(sketch, "E29.84.4", {"start": v(-28.64, -134.74) * mm, "end": v(-29.66, -139.55) * mm});
            skLineSegment(sketch, "E29.84.5", {"start": v(-34.51, -138.43) * mm, "end": v(-34.04, -138.55) * mm});
            skArc(sketch, "E29.84.6", {"start": v(-34.04, -138.55) * mm, "mid": v(-33.68, -138.48) * mm, "end": v(-33.48, -138.17) * mm});
            skArc(sketch, "E29.84.7", {"start": v(-30.48, -138.87) * mm, "mid": v(-30.44, -139.23) * mm, "end": v(-30.14, -139.45) * mm});
            skLineSegment(sketch, "E29.84.8", {"start": v(-30.14, -139.45) * mm, "end": v(-29.66, -139.55) * mm});
            skArc(sketch, "E29.85.0", {"start": v(-25.61, -139.84) * mm, "mid": v(-26.8, -137.9) * mm, "end": v(-28.64, -139.26) * mm});
            skLineSegment(sketch, "E29.85.1", {"start": v(-24.77, -140.5) * mm, "end": v(-23.92, -135.66) * mm, "construction": true});
            skLineSegment(sketch, "E29.85.2", {"start": v(-29.66, -139.55) * mm, "end": v(-28.62, -134.66) * mm});
            skLineSegment(sketch, "E29.85.3", {"start": v(-23.92, -135.66) * mm, "end": v(-28.62, -134.66) * mm});
            skLineSegment(sketch, "E29.85.4", {"start": v(-23.92, -135.66) * mm, "end": v(-24.77, -140.5) * mm});
            skLineSegment(sketch, "E29.85.5", {"start": v(-29.66, -139.55) * mm, "end": v(-29.18, -139.65) * mm});
            skArc(sketch, "E29.85.6", {"start": v(-29.18, -139.65) * mm, "mid": v(-28.82, -139.57) * mm, "end": v(-28.64, -139.26) * mm});
            skArc(sketch, "E29.85.7", {"start": v(-25.61, -139.84) * mm, "mid": v(-25.56, -140.2) * mm, "end": v(-25.25, -140.41) * mm});
            skLineSegment(sketch, "E29.85.8", {"start": v(-25.25, -140.41) * mm, "end": v(-24.77, -140.5) * mm});
            skArc(sketch, "E29.86.0", {"start": v(-20.72, -140.65) * mm, "mid": v(-21.98, -138.75) * mm, "end": v(-23.76, -140.17) * mm});
            skLineSegment(sketch, "E29.86.1", {"start": v(-19.86, -141.28) * mm, "end": v(-19.17, -136.4) * mm, "construction": true});
            skLineSegment(sketch, "E29.86.2", {"start": v(-24.77, -140.5) * mm, "end": v(-23.9, -135.57) * mm});
            skLineSegment(sketch, "E29.86.3", {"start": v(-19.17, -136.4) * mm, "end": v(-23.9, -135.57) * mm});
            skLineSegment(sketch, "E29.86.4", {"start": v(-19.17, -136.4) * mm, "end": v(-19.86, -141.28) * mm});
            skLineSegment(sketch, "E29.86.5", {"start": v(-24.77, -140.5) * mm, "end": v(-24.3, -140.58) * mm});
            skArc(sketch, "E29.86.6", {"start": v(-24.3, -140.58) * mm, "mid": v(-23.94, -140.5) * mm, "end": v(-23.76, -140.17) * mm});
            skArc(sketch, "E29.86.7", {"start": v(-20.72, -140.65) * mm, "mid": v(-20.65, -141.02) * mm, "end": v(-20.34, -141.21) * mm});
            skLineSegment(sketch, "E29.86.8", {"start": v(-20.34, -141.21) * mm, "end": v(-19.86, -141.28) * mm});
            skArc(sketch, "E29.87.0", {"start": v(-15.8, -141.3) * mm, "mid": v(-17.12, -139.44) * mm, "end": v(-18.86, -140.91) * mm});
            skLineSegment(sketch, "E29.87.1", {"start": v(-14.91, -141.89) * mm, "end": v(-14.4, -137) * mm, "construction": true});
            skLineSegment(sketch, "E29.87.2", {"start": v(-19.86, -141.28) * mm, "end": v(-19.16, -136.33) * mm});
            skLineSegment(sketch, "E29.87.3", {"start": v(-14.4, -137) * mm, "end": v(-19.16, -136.33) * mm});
            skLineSegment(sketch, "E29.87.4", {"start": v(-14.4, -137) * mm, "end": v(-14.91, -141.89) * mm});
            skLineSegment(sketch, "E29.87.5", {"start": v(-19.86, -141.28) * mm, "end": v(-19.37, -141.35) * mm});
            skArc(sketch, "E29.87.6", {"start": v(-19.37, -141.35) * mm, "mid": v(-19.02, -141.24) * mm, "end": v(-18.86, -140.91) * mm});
            skArc(sketch, "E29.87.7", {"start": v(-15.8, -141.3) * mm, "mid": v(-15.72, -141.65) * mm, "end": v(-15.4, -141.83) * mm});
            skLineSegment(sketch, "E29.87.8", {"start": v(-15.4, -141.83) * mm, "end": v(-14.91, -141.89) * mm});
            skArc(sketch, "E29.88.0", {"start": v(-10.85, -141.76) * mm, "mid": v(-12.24, -139.95) * mm, "end": v(-13.93, -141.49) * mm});
            skLineSegment(sketch, "E29.88.1", {"start": v(-9.95, -142.32) * mm, "end": v(-9.6, -137.41) * mm, "construction": true});
            skLineSegment(sketch, "E29.88.2", {"start": v(-14.91, -141.89) * mm, "end": v(-14.39, -136.91) * mm});
            skLineSegment(sketch, "E29.88.3", {"start": v(-9.6, -137.41) * mm, "end": v(-14.39, -136.91) * mm});
            skLineSegment(sketch, "E29.88.4", {"start": v(-9.6, -137.41) * mm, "end": v(-9.95, -142.32) * mm});
            skLineSegment(sketch, "E29.88.5", {"start": v(-14.91, -141.89) * mm, "end": v(-14.43, -141.94) * mm});
            skArc(sketch, "E29.88.6", {"start": v(-14.43, -141.94) * mm, "mid": v(-14.08, -141.82) * mm, "end": v(-13.93, -141.49) * mm});
            skArc(sketch, "E29.88.7", {"start": v(-10.85, -141.76) * mm, "mid": v(-10.76, -142.11) * mm, "end": v(-10.44, -142.29) * mm});
            skLineSegment(sketch, "E29.88.8", {"start": v(-10.44, -142.29) * mm, "end": v(-9.95, -142.32) * mm});
            skArc(sketch, "E29.89.0", {"start": v(-5.9, -142.05) * mm, "mid": v(-7.35, -140.3) * mm, "end": v(-8.98, -141.89) * mm});
            skLineSegment(sketch, "E29.89.1", {"start": v(-4.98, -142.58) * mm, "end": v(-4.8, -137.67) * mm, "construction": true});
            skLineSegment(sketch, "E29.89.2", {"start": v(-9.95, -142.32) * mm, "end": v(-9.6, -137.33) * mm});
            skLineSegment(sketch, "E29.89.3", {"start": v(-4.8, -137.67) * mm, "end": v(-9.6, -137.33) * mm});
            skLineSegment(sketch, "E29.89.4", {"start": v(-4.8, -137.67) * mm, "end": v(-4.98, -142.58) * mm});
            skLineSegment(sketch, "E29.89.5", {"start": v(-9.95, -142.32) * mm, "end": v(-9.46, -142.35) * mm});
            skArc(sketch, "E29.89.6", {"start": v(-9.46, -142.35) * mm, "mid": v(-9.12, -142.23) * mm, "end": v(-8.98, -141.89) * mm});
            skArc(sketch, "E29.89.7", {"start": v(-5.9, -142.05) * mm, "mid": v(-5.8, -142.4) * mm, "end": v(-5.47, -142.56) * mm});
            skLineSegment(sketch, "E29.89.8", {"start": v(-5.47, -142.56) * mm, "end": v(-4.98, -142.58) * mm});
            skArc(sketch, "E29.90.0", {"start": v(-0.94, -142.17) * mm, "mid": v(-2.45, -140.46) * mm, "end": v(-4.02, -142.11) * mm});
            skLineSegment(sketch, "E29.90.1", {"start": v(0, -142.67) * mm, "end": v(0, -137.75) * mm, "construction": true});
            skLineSegment(sketch, "E29.90.2", {"start": v(-4.98, -142.58) * mm, "end": v(-4.8, -137.58) * mm});
            skLineSegment(sketch, "E29.90.3", {"start": v(0, -137.75) * mm, "end": v(-4.8, -137.58) * mm});
            skLineSegment(sketch, "E29.90.4", {"start": v(0, -137.75) * mm, "end": v(0, -142.67) * mm});
            skLineSegment(sketch, "E29.90.5", {"start": v(-4.98, -142.58) * mm, "end": v(-4.5, -142.6) * mm});
            skArc(sketch, "E29.90.6", {"start": v(-4.5, -142.6) * mm, "mid": v(-4.15, -142.46) * mm, "end": v(-4.02, -142.11) * mm});
            skArc(sketch, "E29.90.7", {"start": v(-0.94, -142.17) * mm, "mid": v(-0.82, -142.52) * mm, "end": v(-0.49, -142.67) * mm});
            skLineSegment(sketch, "E29.90.8", {"start": v(-0.49, -142.67) * mm, "end": v(0, -142.67) * mm});
            skArc(sketch, "E29.91.0", {"start": v(4.02, -142.11) * mm, "mid": v(2.45, -140.46) * mm, "end": v(0.94, -142.17) * mm});
            skLineSegment(sketch, "E29.91.1", {"start": v(4.98, -142.58) * mm, "end": v(4.8, -137.67) * mm, "construction": true});
            skLineSegment(sketch, "E29.91.2", {"start": v(0, -142.67) * mm, "end": v(0, -137.67) * mm});
            skLineSegment(sketch, "E29.91.3", {"start": v(4.8, -137.67) * mm, "end": v(0, -137.67) * mm});
            skLineSegment(sketch, "E29.91.4", {"start": v(4.8, -137.67) * mm, "end": v(4.98, -142.58) * mm});
            skLineSegment(sketch, "E29.91.5", {"start": v(0, -142.67) * mm, "end": v(0.49, -142.67) * mm});
            skArc(sketch, "E29.91.6", {"start": v(0.49, -142.67) * mm, "mid": v(0.82, -142.52) * mm, "end": v(0.94, -142.17) * mm});
            skArc(sketch, "E29.91.7", {"start": v(4.02, -142.11) * mm, "mid": v(4.15, -142.46) * mm, "end": v(4.5, -142.6) * mm});
            skLineSegment(sketch, "E29.91.8", {"start": v(4.5, -142.6) * mm, "end": v(4.98, -142.58) * mm});
            skArc(sketch, "E29.92.0", {"start": v(8.98, -141.89) * mm, "mid": v(7.35, -140.3) * mm, "end": v(5.9, -142.05) * mm});
            skLineSegment(sketch, "E29.92.1", {"start": v(9.95, -142.32) * mm, "end": v(9.6, -137.41) * mm, "construction": true});
            skLineSegment(sketch, "E29.92.2", {"start": v(4.98, -142.58) * mm, "end": v(4.8, -137.58) * mm});
            skLineSegment(sketch, "E29.92.3", {"start": v(9.6, -137.41) * mm, "end": v(4.8, -137.58) * mm});
            skLineSegment(sketch, "E29.92.4", {"start": v(9.6, -137.41) * mm, "end": v(9.95, -142.32) * mm});
            skLineSegment(sketch, "E29.92.5", {"start": v(4.98, -142.58) * mm, "end": v(5.47, -142.56) * mm});
            skArc(sketch, "E29.92.6", {"start": v(5.47, -142.56) * mm, "mid": v(5.8, -142.4) * mm, "end": v(5.9, -142.05) * mm});
            skArc(sketch, "E29.92.7", {"start": v(8.98, -141.89) * mm, "mid": v(9.12, -142.23) * mm, "end": v(9.46, -142.35) * mm});
            skLineSegment(sketch, "E29.92.8", {"start": v(9.46, -142.35) * mm, "end": v(9.95, -142.32) * mm});
            skArc(sketch, "E29.93.0", {"start": v(13.93, -141.49) * mm, "mid": v(12.24, -139.95) * mm, "end": v(10.85, -141.76) * mm});
            skLineSegment(sketch, "E29.93.1", {"start": v(14.91, -141.89) * mm, "end": v(14.4, -137) * mm, "construction": true});
            skLineSegment(sketch, "E29.93.2", {"start": v(9.95, -142.32) * mm, "end": v(9.6, -137.33) * mm});
            skLineSegment(sketch, "E29.93.3", {"start": v(14.4, -137) * mm, "end": v(9.6, -137.33) * mm});
            skLineSegment(sketch, "E29.93.4", {"start": v(14.4, -137) * mm, "end": v(14.91, -141.89) * mm});
            skLineSegment(sketch, "E29.93.5", {"start": v(9.95, -142.32) * mm, "end": v(10.44, -142.29) * mm});
            skArc(sketch, "E29.93.6", {"start": v(10.44, -142.29) * mm, "mid": v(10.76, -142.11) * mm, "end": v(10.85, -141.76) * mm});
            skArc(sketch, "E29.93.7", {"start": v(13.93, -141.49) * mm, "mid": v(14.08, -141.82) * mm, "end": v(14.43, -141.94) * mm});
            skLineSegment(sketch, "E29.93.8", {"start": v(14.43, -141.94) * mm, "end": v(14.91, -141.89) * mm});
            skArc(sketch, "E29.94.0", {"start": v(18.86, -140.91) * mm, "mid": v(17.12, -139.44) * mm, "end": v(15.8, -141.3) * mm});
            skLineSegment(sketch, "E29.94.1", {"start": v(19.86, -141.28) * mm, "end": v(19.17, -136.4) * mm, "construction": true});
            skLineSegment(sketch, "E29.94.2", {"start": v(14.91, -141.89) * mm, "end": v(14.39, -136.91) * mm});
            skLineSegment(sketch, "E29.94.3", {"start": v(19.17, -136.4) * mm, "end": v(14.39, -136.91) * mm});
            skLineSegment(sketch, "E29.94.4", {"start": v(19.17, -136.4) * mm, "end": v(19.86, -141.28) * mm});
            skLineSegment(sketch, "E29.94.5", {"start": v(14.91, -141.89) * mm, "end": v(15.4, -141.83) * mm});
            skArc(sketch, "E29.94.6", {"start": v(15.4, -141.83) * mm, "mid": v(15.72, -141.65) * mm, "end": v(15.8, -141.3) * mm});
            skArc(sketch, "E29.94.7", {"start": v(18.86, -140.91) * mm, "mid": v(19.02, -141.24) * mm, "end": v(19.37, -141.35) * mm});
            skLineSegment(sketch, "E29.94.8", {"start": v(19.37, -141.35) * mm, "end": v(19.86, -141.28) * mm});
            skArc(sketch, "E29.95.0", {"start": v(23.76, -140.17) * mm, "mid": v(21.98, -138.75) * mm, "end": v(20.72, -140.65) * mm});
            skLineSegment(sketch, "E29.95.1", {"start": v(24.77, -140.5) * mm, "end": v(23.92, -135.66) * mm, "construction": true});
            skLineSegment(sketch, "E29.95.2", {"start": v(19.86, -141.28) * mm, "end": v(19.16, -136.33) * mm});
            skLineSegment(sketch, "E29.95.3", {"start": v(23.92, -135.66) * mm, "end": v(19.16, -136.33) * mm});
            skLineSegment(sketch, "E29.95.4", {"start": v(23.92, -135.66) * mm, "end": v(24.77, -140.5) * mm});
            skLineSegment(sketch, "E29.95.5", {"start": v(19.86, -141.28) * mm, "end": v(20.34, -141.21) * mm});
            skArc(sketch, "E29.95.6", {"start": v(20.34, -141.21) * mm, "mid": v(20.65, -141.02) * mm, "end": v(20.72, -140.65) * mm});
            skArc(sketch, "E29.95.7", {"start": v(23.76, -140.17) * mm, "mid": v(23.94, -140.5) * mm, "end": v(24.3, -140.58) * mm});
            skLineSegment(sketch, "E29.95.8", {"start": v(24.3, -140.58) * mm, "end": v(24.77, -140.5) * mm});
            skArc(sketch, "E29.96.0", {"start": v(28.64, -139.26) * mm, "mid": v(26.8, -137.9) * mm, "end": v(25.61, -139.84) * mm});
            skLineSegment(sketch, "E29.96.1", {"start": v(29.66, -139.55) * mm, "end": v(28.64, -134.74) * mm, "construction": true});
            skLineSegment(sketch, "E29.96.2", {"start": v(24.77, -140.5) * mm, "end": v(23.9, -135.57) * mm});
            skLineSegment(sketch, "E29.96.3", {"start": v(28.64, -134.74) * mm, "end": v(23.9, -135.57) * mm});
            skLineSegment(sketch, "E29.96.4", {"start": v(28.64, -134.74) * mm, "end": v(29.66, -139.55) * mm});
            skLineSegment(sketch, "E29.96.5", {"start": v(24.77, -140.5) * mm, "end": v(25.25, -140.41) * mm});
            skArc(sketch, "E29.96.6", {"start": v(25.25, -140.41) * mm, "mid": v(25.56, -140.2) * mm, "end": v(25.61, -139.84) * mm});
            skArc(sketch, "E29.96.7", {"start": v(28.64, -139.26) * mm, "mid": v(28.82, -139.57) * mm, "end": v(29.18, -139.65) * mm});
            skLineSegment(sketch, "E29.96.8", {"start": v(29.18, -139.65) * mm, "end": v(29.66, -139.55) * mm});
            skArc(sketch, "E29.97.0", {"start": v(33.48, -138.17) * mm, "mid": v(31.6, -136.88) * mm, "end": v(30.48, -138.87) * mm});
            skLineSegment(sketch, "E29.97.1", {"start": v(34.51, -138.43) * mm, "end": v(33.32, -133.66) * mm, "construction": true});
            skLineSegment(sketch, "E29.97.2", {"start": v(29.66, -139.55) * mm, "end": v(28.62, -134.66) * mm});
            skLineSegment(sketch, "E29.97.3", {"start": v(33.32, -133.66) * mm, "end": v(28.62, -134.66) * mm});
            skLineSegment(sketch, "E29.97.4", {"start": v(33.32, -133.66) * mm, "end": v(34.51, -138.43) * mm});
            skLineSegment(sketch, "E29.97.5", {"start": v(29.66, -139.55) * mm, "end": v(30.14, -139.45) * mm});
            skArc(sketch, "E29.97.6", {"start": v(30.14, -139.45) * mm, "mid": v(30.44, -139.23) * mm, "end": v(30.48, -138.87) * mm});
            skArc(sketch, "E29.97.7", {"start": v(33.48, -138.17) * mm, "mid": v(33.68, -138.48) * mm, "end": v(34.04, -138.55) * mm});
            skLineSegment(sketch, "E29.97.8", {"start": v(34.04, -138.55) * mm, "end": v(34.51, -138.43) * mm});
            skArc(sketch, "E29.98.0", {"start": v(38.28, -136.92) * mm, "mid": v(36.36, -135.7) * mm, "end": v(35.3, -137.72) * mm});
            skLineSegment(sketch, "E29.98.1", {"start": v(39.32, -137.14) * mm, "end": v(37.97, -132.41) * mm, "construction": true});
            skLineSegment(sketch, "E29.98.2", {"start": v(34.51, -138.43) * mm, "end": v(33.3, -133.58) * mm});
            skLineSegment(sketch, "E29.98.3", {"start": v(37.97, -132.41) * mm, "end": v(33.3, -133.58) * mm});
            skLineSegment(sketch, "E29.98.4", {"start": v(37.97, -132.41) * mm, "end": v(39.32, -137.14) * mm});
            skLineSegment(sketch, "E29.98.5", {"start": v(34.51, -138.43) * mm, "end": v(34.99, -138.31) * mm});
            skArc(sketch, "E29.98.6", {"start": v(34.99, -138.31) * mm, "mid": v(35.28, -138.08) * mm, "end": v(35.3, -137.72) * mm});
            skArc(sketch, "E29.98.7", {"start": v(38.28, -136.92) * mm, "mid": v(38.5, -137.22) * mm, "end": v(38.85, -137.28) * mm});
            skLineSegment(sketch, "E29.98.8", {"start": v(38.85, -137.28) * mm, "end": v(39.32, -137.14) * mm});
            skArc(sketch, "E29.99.0", {"start": v(43.04, -135.5) * mm, "mid": v(41.07, -134.35) * mm, "end": v(40.09, -136.4) * mm});
            skLineSegment(sketch, "E29.99.1", {"start": v(44.09, -135.69) * mm, "end": v(42.57, -131) * mm, "construction": true});
            skLineSegment(sketch, "E29.99.2", {"start": v(39.32, -137.14) * mm, "end": v(37.95, -132.33) * mm});
            skLineSegment(sketch, "E29.99.3", {"start": v(42.57, -131) * mm, "end": v(37.95, -132.33) * mm});
            skLineSegment(sketch, "E29.99.4", {"start": v(42.57, -131) * mm, "end": v(44.09, -135.69) * mm});
            skLineSegment(sketch, "E29.99.5", {"start": v(39.32, -137.14) * mm, "end": v(39.8, -137) * mm});
            skArc(sketch, "E29.99.6", {"start": v(39.8, -137) * mm, "mid": v(40.08, -136.77) * mm, "end": v(40.09, -136.4) * mm});
            skArc(sketch, "E29.99.7", {"start": v(43.04, -135.5) * mm, "mid": v(43.26, -135.8) * mm, "end": v(43.62, -135.84) * mm});
            skLineSegment(sketch, "E29.99.8", {"start": v(43.62, -135.84) * mm, "end": v(44.09, -135.69) * mm});
            skArc(sketch, "E29.100.0", {"start": v(47.74, -133.91) * mm, "mid": v(45.74, -132.83) * mm, "end": v(44.82, -134.92) * mm});
            skLineSegment(sketch, "E29.100.1", {"start": v(48.8, -134.06) * mm, "end": v(47.11, -129.44) * mm, "construction": true});
            skLineSegment(sketch, "E29.100.2", {"start": v(44.09, -135.69) * mm, "end": v(42.54, -130.93) * mm});
            skLineSegment(sketch, "E29.100.3", {"start": v(47.11, -129.44) * mm, "end": v(42.54, -130.93) * mm});
            skLineSegment(sketch, "E29.100.4", {"start": v(47.11, -129.44) * mm, "end": v(48.8, -134.06) * mm});
            skLineSegment(sketch, "E29.100.5", {"start": v(44.09, -135.69) * mm, "end": v(44.55, -135.53) * mm});
            skArc(sketch, "E29.100.6", {"start": v(44.55, -135.53) * mm, "mid": v(44.82, -135.29) * mm, "end": v(44.82, -134.92) * mm});
            skArc(sketch, "E29.100.7", {"start": v(47.74, -133.91) * mm, "mid": v(47.97, -134.2) * mm, "end": v(48.34, -134.23) * mm});
            skLineSegment(sketch, "E29.100.8", {"start": v(48.34, -134.23) * mm, "end": v(48.8, -134.06) * mm});
            skArc(sketch, "E29.101.0", {"start": v(52.39, -132.17) * mm, "mid": v(50.35, -131.15) * mm, "end": v(49.5, -133.27) * mm});
            skLineSegment(sketch, "E29.101.1", {"start": v(53.44, -132.28) * mm, "end": v(51.6, -127.72) * mm, "construction": true});
            skLineSegment(sketch, "E29.101.2", {"start": v(48.8, -134.06) * mm, "end": v(47.08, -129.36) * mm});
            skLineSegment(sketch, "E29.101.3", {"start": v(51.6, -127.72) * mm, "end": v(47.08, -129.36) * mm});
            skLineSegment(sketch, "E29.101.4", {"start": v(51.6, -127.72) * mm, "end": v(53.44, -132.28) * mm});
            skLineSegment(sketch, "E29.101.5", {"start": v(48.8, -134.06) * mm, "end": v(49.25, -133.9) * mm});
            skArc(sketch, "E29.101.6", {"start": v(49.25, -133.9) * mm, "mid": v(49.52, -133.64) * mm, "end": v(49.5, -133.27) * mm});
            skArc(sketch, "E29.101.7", {"start": v(52.39, -132.17) * mm, "mid": v(52.62, -132.45) * mm, "end": v(53, -132.46) * mm});
            skLineSegment(sketch, "E29.101.8", {"start": v(53, -132.46) * mm, "end": v(53.44, -132.28) * mm});
            skArc(sketch, "E29.102.0", {"start": v(56.97, -130.26) * mm, "mid": v(54.9, -129.32) * mm, "end": v(54.13, -131.46) * mm});
            skLineSegment(sketch, "E29.102.1", {"start": v(58.03, -130.33) * mm, "end": v(56.03, -125.84) * mm, "construction": true});
            skLineSegment(sketch, "E29.102.2", {"start": v(53.44, -132.28) * mm, "end": v(51.57, -127.64) * mm});
            skLineSegment(sketch, "E29.102.3", {"start": v(56.03, -125.84) * mm, "end": v(51.57, -127.64) * mm});
            skLineSegment(sketch, "E29.102.4", {"start": v(56.03, -125.84) * mm, "end": v(58.03, -130.33) * mm});
            skLineSegment(sketch, "E29.102.5", {"start": v(53.44, -132.28) * mm, "end": v(53.9, -132.1) * mm});
            skArc(sketch, "E29.102.6", {"start": v(53.9, -132.1) * mm, "mid": v(54.15, -131.83) * mm, "end": v(54.13, -131.46) * mm});
            skArc(sketch, "E29.102.7", {"start": v(56.97, -130.26) * mm, "mid": v(57.21, -130.53) * mm, "end": v(57.58, -130.53) * mm});
            skLineSegment(sketch, "E29.102.8", {"start": v(57.58, -130.53) * mm, "end": v(58.03, -130.33) * mm});
            skArc(sketch, "E29.103.0", {"start": v(61.48, -128.2) * mm, "mid": v(59.37, -127.32) * mm, "end": v(58.68, -129.5) * mm});
            skLineSegment(sketch, "E29.103.1", {"start": v(62.54, -128.23) * mm, "end": v(60.39, -123.8) * mm, "construction": true});
            skLineSegment(sketch, "E29.103.2", {"start": v(58.03, -130.33) * mm, "end": v(56, -125.76) * mm});
            skLineSegment(sketch, "E29.103.3", {"start": v(60.39, -123.8) * mm, "end": v(56, -125.76) * mm});
            skLineSegment(sketch, "E29.103.4", {"start": v(60.39, -123.8) * mm, "end": v(62.54, -128.23) * mm});
            skLineSegment(sketch, "E29.103.5", {"start": v(58.03, -130.33) * mm, "end": v(58.47, -130.13) * mm});
            skArc(sketch, "E29.103.6", {"start": v(58.47, -130.13) * mm, "mid": v(58.72, -129.86) * mm, "end": v(58.68, -129.5) * mm});
            skArc(sketch, "E29.103.7", {"start": v(61.48, -128.2) * mm, "mid": v(61.73, -128.45) * mm, "end": v(62.1, -128.44) * mm});
            skLineSegment(sketch, "E29.103.8", {"start": v(62.1, -128.44) * mm, "end": v(62.54, -128.23) * mm});
            skArc(sketch, "E29.104.0", {"start": v(65.91, -125.97) * mm, "mid": v(63.78, -125.17) * mm, "end": v(63.17, -127.37) * mm});
            skLineSegment(sketch, "E29.104.1", {"start": v(66.98, -125.97) * mm, "end": v(64.67, -121.63) * mm, "construction": true});
            skLineSegment(sketch, "E29.104.2", {"start": v(62.54, -128.23) * mm, "end": v(60.35, -123.73) * mm});
            skLineSegment(sketch, "E29.104.3", {"start": v(64.67, -121.63) * mm, "end": v(60.35, -123.73) * mm});
            skLineSegment(sketch, "E29.104.4", {"start": v(64.67, -121.63) * mm, "end": v(66.98, -125.97) * mm});
            skLineSegment(sketch, "E29.104.5", {"start": v(62.54, -128.23) * mm, "end": v(62.98, -128.01) * mm});
            skArc(sketch, "E29.104.6", {"start": v(62.98, -128.01) * mm, "mid": v(63.22, -127.73) * mm, "end": v(63.17, -127.37) * mm});
            skArc(sketch, "E29.104.7", {"start": v(65.91, -125.97) * mm, "mid": v(66.18, -126.22) * mm, "end": v(66.55, -126.2) * mm});
            skLineSegment(sketch, "E29.104.8", {"start": v(66.55, -126.2) * mm, "end": v(66.98, -125.97) * mm});
            skArc(sketch, "E29.105.0", {"start": v(70.27, -123.59) * mm, "mid": v(68.1, -122.87) * mm, "end": v(67.57, -125.09) * mm});
            skLineSegment(sketch, "E29.105.1", {"start": v(71.33, -123.55) * mm, "end": v(68.87, -119.3) * mm, "construction": true});
            skLineSegment(sketch, "E29.105.2", {"start": v(66.98, -125.97) * mm, "end": v(64.63, -121.55) * mm});
            skLineSegment(sketch, "E29.105.3", {"start": v(68.87, -119.3) * mm, "end": v(64.63, -121.55) * mm});
            skLineSegment(sketch, "E29.105.4", {"start": v(68.87, -119.3) * mm, "end": v(71.33, -123.55) * mm});
            skLineSegment(sketch, "E29.105.5", {"start": v(66.98, -125.97) * mm, "end": v(67.4, -125.74) * mm});
            skArc(sketch, "E29.105.6", {"start": v(67.4, -125.74) * mm, "mid": v(67.64, -125.45) * mm, "end": v(67.57, -125.09) * mm});
            skArc(sketch, "E29.105.7", {"start": v(70.27, -123.59) * mm, "mid": v(70.54, -123.84) * mm, "end": v(70.91, -123.8) * mm});
            skLineSegment(sketch, "E29.105.8", {"start": v(70.91, -123.8) * mm, "end": v(71.33, -123.55) * mm});
            skArc(sketch, "E29.106.0", {"start": v(74.54, -121.06) * mm, "mid": v(72.35, -120.42) * mm, "end": v(71.9, -122.65) * mm});
            skLineSegment(sketch, "E29.106.1", {"start": v(75.6, -120.99) * mm, "end": v(73, -116.82) * mm, "construction": true});
            skLineSegment(sketch, "E29.106.2", {"start": v(71.33, -123.55) * mm, "end": v(68.83, -119.22) * mm});
            skLineSegment(sketch, "E29.106.3", {"start": v(73, -116.82) * mm, "end": v(68.83, -119.22) * mm});
            skLineSegment(sketch, "E29.106.4", {"start": v(73, -116.82) * mm, "end": v(75.6, -120.99) * mm});
            skLineSegment(sketch, "E29.106.5", {"start": v(71.33, -123.55) * mm, "end": v(71.76, -123.3) * mm});
            skArc(sketch, "E29.106.6", {"start": v(71.76, -123.3) * mm, "mid": v(71.97, -123.01) * mm, "end": v(71.9, -122.65) * mm});
            skArc(sketch, "E29.106.7", {"start": v(74.54, -121.06) * mm, "mid": v(74.82, -121.3) * mm, "end": v(75.19, -121.25) * mm});
            skLineSegment(sketch, "E29.106.8", {"start": v(75.19, -121.25) * mm, "end": v(75.6, -120.99) * mm});
            skArc(sketch, "E29.107.0", {"start": v(78.72, -118.39) * mm, "mid": v(76.51, -117.82) * mm, "end": v(76.13, -120.07) * mm});
            skLineSegment(sketch, "E29.107.1", {"start": v(79.78, -118.28) * mm, "end": v(77.03, -114.2) * mm, "construction": true});
            skLineSegment(sketch, "E29.107.2", {"start": v(75.6, -120.99) * mm, "end": v(72.95, -116.75) * mm});
            skLineSegment(sketch, "E29.107.3", {"start": v(77.03, -114.2) * mm, "end": v(72.95, -116.75) * mm});
            skLineSegment(sketch, "E29.107.4", {"start": v(77.03, -114.2) * mm, "end": v(79.78, -118.28) * mm});
            skLineSegment(sketch, "E29.107.5", {"start": v(75.6, -120.99) * mm, "end": v(76.02, -120.73) * mm});
            skArc(sketch, "E29.107.6", {"start": v(76.02, -120.73) * mm, "mid": v(76.22, -120.42) * mm, "end": v(76.13, -120.07) * mm});
            skArc(sketch, "E29.107.7", {"start": v(78.72, -118.39) * mm, "mid": v(79.01, -118.61) * mm, "end": v(79.37, -118.55) * mm});
            skLineSegment(sketch, "E29.107.8", {"start": v(79.37, -118.55) * mm, "end": v(79.78, -118.28) * mm});
            skArc(sketch, "E29.108.0", {"start": v(82.8, -115.57) * mm, "mid": v(80.58, -115.08) * mm, "end": v(80.28, -117.34) * mm});
            skLineSegment(sketch, "E29.108.1", {"start": v(83.86, -115.42) * mm, "end": v(80.97, -111.44) * mm, "construction": true});
            skLineSegment(sketch, "E29.108.2", {"start": v(79.78, -118.28) * mm, "end": v(76.98, -114.13) * mm});
            skLineSegment(sketch, "E29.108.3", {"start": v(80.97, -111.44) * mm, "end": v(76.98, -114.13) * mm});
            skLineSegment(sketch, "E29.108.4", {"start": v(80.97, -111.44) * mm, "end": v(83.86, -115.42) * mm});
            skLineSegment(sketch, "E29.108.5", {"start": v(79.78, -118.28) * mm, "end": v(80.18, -118) * mm});
            skArc(sketch, "E29.108.6", {"start": v(80.18, -118) * mm, "mid": v(80.38, -117.7) * mm, "end": v(80.28, -117.34) * mm});
            skArc(sketch, "E29.108.7", {"start": v(82.8, -115.57) * mm, "mid": v(83.1, -115.78) * mm, "end": v(83.46, -115.7) * mm});
            skLineSegment(sketch, "E29.108.8", {"start": v(83.46, -115.7) * mm, "end": v(83.86, -115.42) * mm});
            skArc(sketch, "E29.109.0", {"start": v(86.79, -112.6) * mm, "mid": v(84.55, -112.2) * mm, "end": v(84.32, -114.46) * mm});
            skLineSegment(sketch, "E29.109.1", {"start": v(87.84, -112.42) * mm, "end": v(84.8, -108.55) * mm, "construction": true});
            skLineSegment(sketch, "E29.109.2", {"start": v(83.86, -115.42) * mm, "end": v(80.92, -111.37) * mm});
            skLineSegment(sketch, "E29.109.3", {"start": v(84.8, -108.55) * mm, "end": v(80.92, -111.37) * mm});
            skLineSegment(sketch, "E29.109.4", {"start": v(84.8, -108.55) * mm, "end": v(87.84, -112.42) * mm});
            skLineSegment(sketch, "E29.109.5", {"start": v(83.86, -115.42) * mm, "end": v(84.25, -115.13) * mm});
            skArc(sketch, "E29.109.6", {"start": v(84.25, -115.13) * mm, "mid": v(84.44, -114.81) * mm, "end": v(84.32, -114.46) * mm});
            skArc(sketch, "E29.109.7", {"start": v(86.79, -112.6) * mm, "mid": v(87.1, -112.81) * mm, "end": v(87.45, -112.72) * mm});
            skLineSegment(sketch, "E29.109.8", {"start": v(87.45, -112.72) * mm, "end": v(87.84, -112.42) * mm});
            skArc(sketch, "E29.110.0", {"start": v(90.66, -109.5) * mm, "mid": v(88.4, -109.18) * mm, "end": v(88.27, -111.45) * mm});
            skLineSegment(sketch, "E29.110.1", {"start": v(91.7, -109.29) * mm, "end": v(88.54, -105.52) * mm, "construction": true});
            skLineSegment(sketch, "E29.110.2", {"start": v(87.84, -112.42) * mm, "end": v(84.76, -108.48) * mm});
            skLineSegment(sketch, "E29.110.3", {"start": v(88.54, -105.52) * mm, "end": v(84.76, -108.48) * mm});
            skLineSegment(sketch, "E29.110.4", {"start": v(88.54, -105.52) * mm, "end": v(91.7, -109.29) * mm});
            skLineSegment(sketch, "E29.110.5", {"start": v(87.84, -112.42) * mm, "end": v(88.22, -112.12) * mm});
            skArc(sketch, "E29.110.6", {"start": v(88.22, -112.12) * mm, "mid": v(88.4, -111.8) * mm, "end": v(88.27, -111.45) * mm});
            skArc(sketch, "E29.110.7", {"start": v(90.66, -109.5) * mm, "mid": v(90.98, -109.7) * mm, "end": v(91.33, -109.6) * mm});
            skLineSegment(sketch, "E29.110.8", {"start": v(91.33, -109.6) * mm, "end": v(91.7, -109.29) * mm});
            skArc(sketch, "E29.111.0", {"start": v(94.43, -106.28) * mm, "mid": v(92.17, -106.02) * mm, "end": v(92.1, -108.3) * mm});
            skLineSegment(sketch, "E29.111.1", {"start": v(95.46, -106.02) * mm, "end": v(92.17, -102.37) * mm, "construction": true});
            skLineSegment(sketch, "E29.111.2", {"start": v(91.7, -109.3) * mm, "end": v(88.49, -105.46) * mm});
            skLineSegment(sketch, "E29.111.3", {"start": v(92.17, -102.37) * mm, "end": v(88.49, -105.46) * mm});
            skLineSegment(sketch, "E29.111.4", {"start": v(92.17, -102.37) * mm, "end": v(95.46, -106.02) * mm});
            skLineSegment(sketch, "E29.111.5", {"start": v(91.7, -109.3) * mm, "end": v(92.08, -108.98) * mm});
            skArc(sketch, "E29.111.6", {"start": v(92.08, -108.98) * mm, "mid": v(92.24, -108.64) * mm, "end": v(92.1, -108.3) * mm});
            skArc(sketch, "E29.111.7", {"start": v(94.43, -106.28) * mm, "mid": v(94.75, -106.46) * mm, "end": v(95.1, -106.35) * mm});
            skLineSegment(sketch, "E29.111.8", {"start": v(95.1, -106.35) * mm, "end": v(95.46, -106.02) * mm});
            skArc(sketch, "E29.112.0", {"start": v(98.08, -102.92) * mm, "mid": v(95.81, -102.74) * mm, "end": v(95.83, -105.02) * mm});
            skLineSegment(sketch, "E29.112.1", {"start": v(99.1, -102.63) * mm, "end": v(95.69, -99.09) * mm, "construction": true});
            skLineSegment(sketch, "E29.112.2", {"start": v(95.46, -106.02) * mm, "end": v(92.12, -102.3) * mm});
            skLineSegment(sketch, "E29.112.3", {"start": v(95.69, -99.09) * mm, "end": v(92.12, -102.3) * mm});
            skLineSegment(sketch, "E29.112.4", {"start": v(95.69, -99.09) * mm, "end": v(99.1, -102.63) * mm});
            skLineSegment(sketch, "E29.112.5", {"start": v(95.46, -106.02) * mm, "end": v(95.83, -105.7) * mm});
            skArc(sketch, "E29.112.6", {"start": v(95.83, -105.7) * mm, "mid": v(95.97, -105.36) * mm, "end": v(95.83, -105.02) * mm});
            skArc(sketch, "E29.112.7", {"start": v(98.08, -102.92) * mm, "mid": v(98.4, -103.1) * mm, "end": v(98.75, -102.97) * mm});
            skLineSegment(sketch, "E29.112.8", {"start": v(98.75, -102.97) * mm, "end": v(99.1, -102.63) * mm});
            skArc(sketch, "E29.113.0", {"start": v(101.61, -99.43) * mm, "mid": v(99.34, -99.34) * mm, "end": v(99.43, -101.61) * mm});
            skLineSegment(sketch, "E29.113.1", {"start": v(102.63, -99.1) * mm, "end": v(99.09, -95.69) * mm, "construction": true});
            skLineSegment(sketch, "E29.113.2", {"start": v(99.1, -102.63) * mm, "end": v(95.63, -99.03) * mm});
            skLineSegment(sketch, "E29.113.3", {"start": v(99.09, -95.69) * mm, "end": v(95.63, -99.03) * mm});
            skLineSegment(sketch, "E29.113.4", {"start": v(99.09, -95.69) * mm, "end": v(102.63, -99.1) * mm});
            skLineSegment(sketch, "E29.113.5", {"start": v(99.1, -102.63) * mm, "end": v(99.46, -102.29) * mm});
            skArc(sketch, "E29.113.6", {"start": v(99.46, -102.29) * mm, "mid": v(99.6, -101.95) * mm, "end": v(99.43, -101.61) * mm});
            skArc(sketch, "E29.113.7", {"start": v(101.61, -99.43) * mm, "mid": v(101.95, -99.6) * mm, "end": v(102.29, -99.46) * mm});
            skLineSegment(sketch, "E29.113.8", {"start": v(102.29, -99.46) * mm, "end": v(102.63, -99.1) * mm});
            skArc(sketch, "E29.114.0", {"start": v(105.02, -95.83) * mm, "mid": v(102.74, -95.81) * mm, "end": v(102.92, -98.08) * mm});
            skLineSegment(sketch, "E29.114.1", {"start": v(106.02, -95.46) * mm, "end": v(102.37, -92.17) * mm, "construction": true});
            skLineSegment(sketch, "E29.114.2", {"start": v(102.63, -99.1) * mm, "end": v(99.03, -95.63) * mm});
            skLineSegment(sketch, "E29.114.3", {"start": v(102.37, -92.17) * mm, "end": v(99.03, -95.63) * mm});
            skLineSegment(sketch, "E29.114.4", {"start": v(102.37, -92.17) * mm, "end": v(106.02, -95.46) * mm});
            skLineSegment(sketch, "E29.114.5", {"start": v(102.63, -99.1) * mm, "end": v(102.97, -98.75) * mm});
            skArc(sketch, "E29.114.6", {"start": v(102.97, -98.75) * mm, "mid": v(103.1, -98.4) * mm, "end": v(102.92, -98.08) * mm});
            skArc(sketch, "E29.114.7", {"start": v(105.02, -95.83) * mm, "mid": v(105.36, -95.97) * mm, "end": v(105.7, -95.83) * mm});
            skLineSegment(sketch, "E29.114.8", {"start": v(105.7, -95.83) * mm, "end": v(106.02, -95.46) * mm});
            skArc(sketch, "E29.115.0", {"start": v(108.3, -92.1) * mm, "mid": v(106.02, -92.17) * mm, "end": v(106.28, -94.43) * mm});
            skLineSegment(sketch, "E29.115.1", {"start": v(109.29, -91.7) * mm, "end": v(105.52, -88.54) * mm, "construction": true});
            skLineSegment(sketch, "E29.115.2", {"start": v(106.02, -95.46) * mm, "end": v(102.3, -92.12) * mm});
            skLineSegment(sketch, "E29.115.3", {"start": v(105.52, -88.54) * mm, "end": v(102.3, -92.12) * mm});
            skLineSegment(sketch, "E29.115.4", {"start": v(105.52, -88.54) * mm, "end": v(109.29, -91.7) * mm});
            skLineSegment(sketch, "E29.115.5", {"start": v(106.02, -95.46) * mm, "end": v(106.35, -95.1) * mm});
            skArc(sketch, "E29.115.6", {"start": v(106.35, -95.1) * mm, "mid": v(106.46, -94.75) * mm, "end": v(106.28, -94.43) * mm});
            skArc(sketch, "E29.115.7", {"start": v(108.3, -92.1) * mm, "mid": v(108.64, -92.24) * mm, "end": v(108.98, -92.08) * mm});
            skLineSegment(sketch, "E29.115.8", {"start": v(108.98, -92.08) * mm, "end": v(109.29, -91.7) * mm});
            skArc(sketch, "E29.116.0", {"start": v(111.45, -88.27) * mm, "mid": v(109.18, -88.4) * mm, "end": v(109.5, -90.66) * mm});
            skLineSegment(sketch, "E29.116.1", {"start": v(112.42, -87.84) * mm, "end": v(108.55, -84.8) * mm, "construction": true});
            skLineSegment(sketch, "E29.116.2", {"start": v(109.3, -91.7) * mm, "end": v(105.46, -88.49) * mm});
            skLineSegment(sketch, "E29.116.3", {"start": v(108.55, -84.8) * mm, "end": v(105.46, -88.49) * mm});
            skLineSegment(sketch, "E29.116.4", {"start": v(108.55, -84.8) * mm, "end": v(112.42, -87.84) * mm});
            skLineSegment(sketch, "E29.116.5", {"start": v(109.3, -91.7) * mm, "end": v(109.6, -91.33) * mm});
            skArc(sketch, "E29.116.6", {"start": v(109.6, -91.33) * mm, "mid": v(109.7, -90.98) * mm, "end": v(109.5, -90.66) * mm});
            skArc(sketch, "E29.116.7", {"start": v(111.45, -88.27) * mm, "mid": v(111.8, -88.4) * mm, "end": v(112.12, -88.22) * mm});
            skLineSegment(sketch, "E29.116.8", {"start": v(112.12, -88.22) * mm, "end": v(112.42, -87.84) * mm});
            skArc(sketch, "E29.117.0", {"start": v(114.46, -84.32) * mm, "mid": v(112.2, -84.55) * mm, "end": v(112.6, -86.79) * mm});
            skLineSegment(sketch, "E29.117.1", {"start": v(115.42, -83.86) * mm, "end": v(111.44, -80.97) * mm, "construction": true});
            skLineSegment(sketch, "E29.117.2", {"start": v(112.42, -87.84) * mm, "end": v(108.48, -84.76) * mm});
            skLineSegment(sketch, "E29.117.3", {"start": v(111.44, -80.97) * mm, "end": v(108.48, -84.76) * mm});
            skLineSegment(sketch, "E29.117.4", {"start": v(111.44, -80.97) * mm, "end": v(115.42, -83.86) * mm});
            skLineSegment(sketch, "E29.117.5", {"start": v(112.42, -87.84) * mm, "end": v(112.72, -87.45) * mm});
            skArc(sketch, "E29.117.6", {"start": v(112.72, -87.45) * mm, "mid": v(112.81, -87.1) * mm, "end": v(112.6, -86.79) * mm});
            skArc(sketch, "E29.117.7", {"start": v(114.46, -84.32) * mm, "mid": v(114.81, -84.44) * mm, "end": v(115.13, -84.25) * mm});
            skLineSegment(sketch, "E29.117.8", {"start": v(115.13, -84.25) * mm, "end": v(115.42, -83.86) * mm});
            skArc(sketch, "E29.118.0", {"start": v(117.34, -80.28) * mm, "mid": v(115.08, -80.58) * mm, "end": v(115.57, -82.8) * mm});
            skLineSegment(sketch, "E29.118.1", {"start": v(118.28, -79.78) * mm, "end": v(114.2, -77.03) * mm, "construction": true});
            skLineSegment(sketch, "E29.118.2", {"start": v(115.42, -83.86) * mm, "end": v(111.37, -80.92) * mm});
            skLineSegment(sketch, "E29.118.3", {"start": v(114.2, -77.03) * mm, "end": v(111.37, -80.92) * mm});
            skLineSegment(sketch, "E29.118.4", {"start": v(114.2, -77.03) * mm, "end": v(118.28, -79.78) * mm});
            skLineSegment(sketch, "E29.118.5", {"start": v(115.42, -83.86) * mm, "end": v(115.7, -83.46) * mm});
            skArc(sketch, "E29.118.6", {"start": v(115.7, -83.46) * mm, "mid": v(115.78, -83.1) * mm, "end": v(115.57, -82.8) * mm});
            skArc(sketch, "E29.118.7", {"start": v(117.34, -80.28) * mm, "mid": v(117.7, -80.38) * mm, "end": v(118, -80.18) * mm});
            skLineSegment(sketch, "E29.118.8", {"start": v(118, -80.18) * mm, "end": v(118.28, -79.78) * mm});
            skArc(sketch, "E29.119.0", {"start": v(120.07, -76.13) * mm, "mid": v(117.82, -76.51) * mm, "end": v(118.39, -78.72) * mm});
            skLineSegment(sketch, "E29.119.1", {"start": v(120.99, -75.6) * mm, "end": v(116.82, -73) * mm, "construction": true});
            skLineSegment(sketch, "E29.119.2", {"start": v(118.28, -79.78) * mm, "end": v(114.13, -76.98) * mm});
            skLineSegment(sketch, "E29.119.3", {"start": v(116.82, -73) * mm, "end": v(114.13, -76.98) * mm});
            skLineSegment(sketch, "E29.119.4", {"start": v(116.82, -73) * mm, "end": v(120.99, -75.6) * mm});
            skLineSegment(sketch, "E29.119.5", {"start": v(118.28, -79.78) * mm, "end": v(118.55, -79.37) * mm});
            skArc(sketch, "E29.119.6", {"start": v(118.55, -79.37) * mm, "mid": v(118.61, -79.01) * mm, "end": v(118.39, -78.72) * mm});
            skArc(sketch, "E29.119.7", {"start": v(120.07, -76.13) * mm, "mid": v(120.42, -76.22) * mm, "end": v(120.73, -76.02) * mm});
            skLineSegment(sketch, "E29.119.8", {"start": v(120.73, -76.02) * mm, "end": v(120.99, -75.6) * mm});
            skArc(sketch, "E29.120.0", {"start": v(122.65, -71.9) * mm, "mid": v(120.42, -72.35) * mm, "end": v(121.06, -74.54) * mm});
            skLineSegment(sketch, "E29.120.1", {"start": v(123.55, -71.33) * mm, "end": v(119.3, -68.87) * mm, "construction": true});
            skLineSegment(sketch, "E29.120.2", {"start": v(120.99, -75.6) * mm, "end": v(116.75, -72.95) * mm});
            skLineSegment(sketch, "E29.120.3", {"start": v(119.3, -68.87) * mm, "end": v(116.75, -72.95) * mm});
            skLineSegment(sketch, "E29.120.4", {"start": v(119.3, -68.87) * mm, "end": v(123.55, -71.33) * mm});
            skLineSegment(sketch, "E29.120.5", {"start": v(120.99, -75.6) * mm, "end": v(121.25, -75.19) * mm});
            skArc(sketch, "E29.120.6", {"start": v(121.25, -75.19) * mm, "mid": v(121.3, -74.82) * mm, "end": v(121.06, -74.54) * mm});
            skArc(sketch, "E29.120.7", {"start": v(122.65, -71.9) * mm, "mid": v(123.01, -71.97) * mm, "end": v(123.3, -71.76) * mm});
            skLineSegment(sketch, "E29.120.8", {"start": v(123.3, -71.76) * mm, "end": v(123.55, -71.33) * mm});
            skArc(sketch, "E29.121.0", {"start": v(125.09, -67.57) * mm, "mid": v(122.87, -68.1) * mm, "end": v(123.59, -70.27) * mm});
            skLineSegment(sketch, "E29.121.1", {"start": v(125.97, -66.98) * mm, "end": v(121.63, -64.67) * mm, "construction": true});
            skLineSegment(sketch, "E29.121.2", {"start": v(123.55, -71.33) * mm, "end": v(119.22, -68.83) * mm});
            skLineSegment(sketch, "E29.121.3", {"start": v(121.63, -64.67) * mm, "end": v(119.22, -68.83) * mm});
            skLineSegment(sketch, "E29.121.4", {"start": v(121.63, -64.67) * mm, "end": v(125.97, -66.98) * mm});
            skLineSegment(sketch, "E29.121.5", {"start": v(123.55, -71.33) * mm, "end": v(123.8, -70.91) * mm});
            skArc(sketch, "E29.121.6", {"start": v(123.8, -70.91) * mm, "mid": v(123.84, -70.54) * mm, "end": v(123.59, -70.27) * mm});
            skArc(sketch, "E29.121.7", {"start": v(125.09, -67.57) * mm, "mid": v(125.45, -67.64) * mm, "end": v(125.74, -67.4) * mm});
            skLineSegment(sketch, "E29.121.8", {"start": v(125.74, -67.4) * mm, "end": v(125.97, -66.98) * mm});
            skArc(sketch, "E29.122.0", {"start": v(127.37, -63.17) * mm, "mid": v(125.17, -63.78) * mm, "end": v(125.97, -65.91) * mm});
            skLineSegment(sketch, "E29.122.1", {"start": v(128.23, -62.54) * mm, "end": v(123.8, -60.39) * mm, "construction": true});
            skLineSegment(sketch, "E29.122.2", {"start": v(125.97, -66.98) * mm, "end": v(121.55, -64.63) * mm});
            skLineSegment(sketch, "E29.122.3", {"start": v(123.8, -60.39) * mm, "end": v(121.55, -64.63) * mm});
            skLineSegment(sketch, "E29.122.4", {"start": v(123.8, -60.39) * mm, "end": v(128.23, -62.54) * mm});
            skLineSegment(sketch, "E29.122.5", {"start": v(125.97, -66.98) * mm, "end": v(126.2, -66.55) * mm});
            skArc(sketch, "E29.122.6", {"start": v(126.2, -66.55) * mm, "mid": v(126.22, -66.18) * mm, "end": v(125.97, -65.91) * mm});
            skArc(sketch, "E29.122.7", {"start": v(127.37, -63.17) * mm, "mid": v(127.73, -63.22) * mm, "end": v(128.01, -62.98) * mm});
            skLineSegment(sketch, "E29.122.8", {"start": v(128.01, -62.98) * mm, "end": v(128.23, -62.54) * mm});
            skArc(sketch, "E29.123.0", {"start": v(129.5, -58.68) * mm, "mid": v(127.32, -59.37) * mm, "end": v(128.2, -61.48) * mm});
            skLineSegment(sketch, "E29.123.1", {"start": v(130.33, -58.03) * mm, "end": v(125.84, -56.03) * mm, "construction": true});
            skLineSegment(sketch, "E29.123.2", {"start": v(128.23, -62.54) * mm, "end": v(123.73, -60.35) * mm});
            skLineSegment(sketch, "E29.123.3", {"start": v(125.84, -56.03) * mm, "end": v(123.73, -60.35) * mm});
            skLineSegment(sketch, "E29.123.4", {"start": v(125.84, -56.03) * mm, "end": v(130.33, -58.03) * mm});
            skLineSegment(sketch, "E29.123.5", {"start": v(128.23, -62.54) * mm, "end": v(128.44, -62.1) * mm});
            skArc(sketch, "E29.123.6", {"start": v(128.44, -62.1) * mm, "mid": v(128.45, -61.73) * mm, "end": v(128.2, -61.48) * mm});
            skArc(sketch, "E29.123.7", {"start": v(129.5, -58.68) * mm, "mid": v(129.86, -58.72) * mm, "end": v(130.13, -58.47) * mm});
            skLineSegment(sketch, "E29.123.8", {"start": v(130.13, -58.47) * mm, "end": v(130.33, -58.03) * mm});
            skArc(sketch, "E29.124.0", {"start": v(131.46, -54.13) * mm, "mid": v(129.32, -54.9) * mm, "end": v(130.26, -56.97) * mm});
            skLineSegment(sketch, "E29.124.1", {"start": v(132.28, -53.44) * mm, "end": v(127.72, -51.6) * mm, "construction": true});
            skLineSegment(sketch, "E29.124.2", {"start": v(130.33, -58.03) * mm, "end": v(125.76, -56) * mm});
            skLineSegment(sketch, "E29.124.3", {"start": v(127.72, -51.6) * mm, "end": v(125.76, -56) * mm});
            skLineSegment(sketch, "E29.124.4", {"start": v(127.72, -51.6) * mm, "end": v(132.28, -53.44) * mm});
            skLineSegment(sketch, "E29.124.5", {"start": v(130.33, -58.03) * mm, "end": v(130.53, -57.58) * mm});
            skArc(sketch, "E29.124.6", {"start": v(130.53, -57.58) * mm, "mid": v(130.53, -57.21) * mm, "end": v(130.26, -56.97) * mm});
            skArc(sketch, "E29.124.7", {"start": v(131.46, -54.13) * mm, "mid": v(131.83, -54.15) * mm, "end": v(132.1, -53.9) * mm});
            skLineSegment(sketch, "E29.124.8", {"start": v(132.1, -53.9) * mm, "end": v(132.28, -53.44) * mm});
            skArc(sketch, "E29.125.0", {"start": v(133.27, -49.5) * mm, "mid": v(131.15, -50.35) * mm, "end": v(132.17, -52.39) * mm});
            skLineSegment(sketch, "E29.125.1", {"start": v(134.06, -48.8) * mm, "end": v(129.44, -47.11) * mm, "construction": true});
            skLineSegment(sketch, "E29.125.2", {"start": v(132.28, -53.44) * mm, "end": v(127.64, -51.57) * mm});
            skLineSegment(sketch, "E29.125.3", {"start": v(129.44, -47.11) * mm, "end": v(127.64, -51.57) * mm});
            skLineSegment(sketch, "E29.125.4", {"start": v(129.44, -47.11) * mm, "end": v(134.06, -48.8) * mm});
            skLineSegment(sketch, "E29.125.5", {"start": v(132.28, -53.44) * mm, "end": v(132.46, -53) * mm});
            skArc(sketch, "E29.125.6", {"start": v(132.46, -53) * mm, "mid": v(132.45, -52.62) * mm, "end": v(132.17, -52.39) * mm});
            skArc(sketch, "E29.125.7", {"start": v(133.27, -49.5) * mm, "mid": v(133.64, -49.52) * mm, "end": v(133.9, -49.25) * mm});
            skLineSegment(sketch, "E29.125.8", {"start": v(133.9, -49.25) * mm, "end": v(134.06, -48.8) * mm});
            skArc(sketch, "E29.126.0", {"start": v(134.92, -44.82) * mm, "mid": v(132.83, -45.74) * mm, "end": v(133.91, -47.74) * mm});
            skLineSegment(sketch, "E29.126.1", {"start": v(135.69, -44.09) * mm, "end": v(131, -42.57) * mm, "construction": true});
            skLineSegment(sketch, "E29.126.2", {"start": v(134.06, -48.8) * mm, "end": v(129.36, -47.08) * mm});
            skLineSegment(sketch, "E29.126.3", {"start": v(131, -42.57) * mm, "end": v(129.36, -47.08) * mm});
            skLineSegment(sketch, "E29.126.4", {"start": v(131, -42.57) * mm, "end": v(135.69, -44.09) * mm});
            skLineSegment(sketch, "E29.126.5", {"start": v(134.06, -48.8) * mm, "end": v(134.23, -48.34) * mm});
            skArc(sketch, "E29.126.6", {"start": v(134.23, -48.34) * mm, "mid": v(134.2, -47.97) * mm, "end": v(133.91, -47.74) * mm});
            skArc(sketch, "E29.126.7", {"start": v(134.92, -44.82) * mm, "mid": v(135.29, -44.82) * mm, "end": v(135.53, -44.55) * mm});
            skLineSegment(sketch, "E29.126.8", {"start": v(135.53, -44.55) * mm, "end": v(135.69, -44.09) * mm});
            skArc(sketch, "E29.127.0", {"start": v(136.4, -40.09) * mm, "mid": v(134.35, -41.07) * mm, "end": v(135.5, -43.04) * mm});
            skLineSegment(sketch, "E29.127.1", {"start": v(137.14, -39.32) * mm, "end": v(132.41, -37.97) * mm, "construction": true});
            skLineSegment(sketch, "E29.127.2", {"start": v(135.69, -44.09) * mm, "end": v(130.93, -42.54) * mm});
            skLineSegment(sketch, "E29.127.3", {"start": v(132.41, -37.97) * mm, "end": v(130.93, -42.54) * mm});
            skLineSegment(sketch, "E29.127.4", {"start": v(132.41, -37.97) * mm, "end": v(137.14, -39.32) * mm});
            skLineSegment(sketch, "E29.127.5", {"start": v(135.69, -44.09) * mm, "end": v(135.84, -43.62) * mm});
            skArc(sketch, "E29.127.6", {"start": v(135.84, -43.62) * mm, "mid": v(135.8, -43.26) * mm, "end": v(135.5, -43.04) * mm});
            skArc(sketch, "E29.127.7", {"start": v(136.4, -40.09) * mm, "mid": v(136.77, -40.08) * mm, "end": v(137, -39.8) * mm});
            skLineSegment(sketch, "E29.127.8", {"start": v(137, -39.8) * mm, "end": v(137.14, -39.32) * mm});
            skArc(sketch, "E29.128.0", {"start": v(137.72, -35.3) * mm, "mid": v(135.7, -36.36) * mm, "end": v(136.92, -38.28) * mm});
            skLineSegment(sketch, "E29.128.1", {"start": v(138.43, -34.51) * mm, "end": v(133.66, -33.32) * mm, "construction": true});
            skLineSegment(sketch, "E29.128.2", {"start": v(137.14, -39.32) * mm, "end": v(132.33, -37.95) * mm});
            skLineSegment(sketch, "E29.128.3", {"start": v(133.66, -33.32) * mm, "end": v(132.33, -37.95) * mm});
            skLineSegment(sketch, "E29.128.4", {"start": v(133.66, -33.32) * mm, "end": v(138.43, -34.51) * mm});
            skLineSegment(sketch, "E29.128.5", {"start": v(137.14, -39.32) * mm, "end": v(137.28, -38.85) * mm});
            skArc(sketch, "E29.128.6", {"start": v(137.28, -38.85) * mm, "mid": v(137.22, -38.5) * mm, "end": v(136.92, -38.28) * mm});
            skArc(sketch, "E29.128.7", {"start": v(137.72, -35.3) * mm, "mid": v(138.08, -35.28) * mm, "end": v(138.31, -34.99) * mm});
            skLineSegment(sketch, "E29.128.8", {"start": v(138.31, -34.99) * mm, "end": v(138.43, -34.51) * mm});
            skArc(sketch, "E29.129.0", {"start": v(138.87, -30.48) * mm, "mid": v(136.88, -31.6) * mm, "end": v(138.17, -33.48) * mm});
            skLineSegment(sketch, "E29.129.1", {"start": v(139.55, -29.66) * mm, "end": v(134.74, -28.64) * mm, "construction": true});
            skLineSegment(sketch, "E29.129.2", {"start": v(138.43, -34.51) * mm, "end": v(133.58, -33.3) * mm});
            skLineSegment(sketch, "E29.129.3", {"start": v(134.74, -28.64) * mm, "end": v(133.58, -33.3) * mm});
            skLineSegment(sketch, "E29.129.4", {"start": v(134.74, -28.64) * mm, "end": v(139.55, -29.66) * mm});
            skLineSegment(sketch, "E29.129.5", {"start": v(138.43, -34.51) * mm, "end": v(138.55, -34.04) * mm});
            skArc(sketch, "E29.129.6", {"start": v(138.55, -34.04) * mm, "mid": v(138.48, -33.68) * mm, "end": v(138.17, -33.48) * mm});
            skArc(sketch, "E29.129.7", {"start": v(138.87, -30.48) * mm, "mid": v(139.23, -30.44) * mm, "end": v(139.45, -30.14) * mm});
            skLineSegment(sketch, "E29.129.8", {"start": v(139.45, -30.14) * mm, "end": v(139.55, -29.66) * mm});
            skArc(sketch, "E29.130.0", {"start": v(139.84, -25.61) * mm, "mid": v(137.9, -26.8) * mm, "end": v(139.26, -28.64) * mm});
            skLineSegment(sketch, "E29.130.1", {"start": v(140.5, -24.77) * mm, "end": v(135.66, -23.92) * mm, "construction": true});
            skLineSegment(sketch, "E29.130.2", {"start": v(139.55, -29.66) * mm, "end": v(134.66, -28.62) * mm});
            skLineSegment(sketch, "E29.130.3", {"start": v(135.66, -23.92) * mm, "end": v(134.66, -28.62) * mm});
            skLineSegment(sketch, "E29.130.4", {"start": v(135.66, -23.92) * mm, "end": v(140.5, -24.77) * mm});
            skLineSegment(sketch, "E29.130.5", {"start": v(139.55, -29.66) * mm, "end": v(139.65, -29.18) * mm});
            skArc(sketch, "E29.130.6", {"start": v(139.65, -29.18) * mm, "mid": v(139.57, -28.82) * mm, "end": v(139.26, -28.64) * mm});
            skArc(sketch, "E29.130.7", {"start": v(139.84, -25.61) * mm, "mid": v(140.2, -25.56) * mm, "end": v(140.41, -25.25) * mm});
            skLineSegment(sketch, "E29.130.8", {"start": v(140.41, -25.25) * mm, "end": v(140.5, -24.77) * mm});
            skArc(sketch, "E29.131.0", {"start": v(140.65, -20.72) * mm, "mid": v(138.75, -21.98) * mm, "end": v(140.17, -23.76) * mm});
            skLineSegment(sketch, "E29.131.1", {"start": v(141.28, -19.86) * mm, "end": v(136.4, -19.17) * mm, "construction": true});
            skLineSegment(sketch, "E29.131.2", {"start": v(140.5, -24.77) * mm, "end": v(135.57, -23.9) * mm});
            skLineSegment(sketch, "E29.131.3", {"start": v(136.4, -19.17) * mm, "end": v(135.57, -23.9) * mm});
            skLineSegment(sketch, "E29.131.4", {"start": v(136.4, -19.17) * mm, "end": v(141.28, -19.86) * mm});
            skLineSegment(sketch, "E29.131.5", {"start": v(140.5, -24.77) * mm, "end": v(140.58, -24.3) * mm});
            skArc(sketch, "E29.131.6", {"start": v(140.58, -24.3) * mm, "mid": v(140.5, -23.94) * mm, "end": v(140.17, -23.76) * mm});
            skArc(sketch, "E29.131.7", {"start": v(140.65, -20.72) * mm, "mid": v(141.02, -20.65) * mm, "end": v(141.21, -20.34) * mm});
            skLineSegment(sketch, "E29.131.8", {"start": v(141.21, -20.34) * mm, "end": v(141.28, -19.86) * mm});
            skArc(sketch, "E29.132.0", {"start": v(141.3, -15.8) * mm, "mid": v(139.44, -17.12) * mm, "end": v(140.91, -18.86) * mm});
            skLineSegment(sketch, "E29.132.1", {"start": v(141.89, -14.91) * mm, "end": v(137, -14.4) * mm, "construction": true});
            skLineSegment(sketch, "E29.132.2", {"start": v(141.28, -19.86) * mm, "end": v(136.33, -19.16) * mm});
            skLineSegment(sketch, "E29.132.3", {"start": v(137, -14.4) * mm, "end": v(136.33, -19.16) * mm});
            skLineSegment(sketch, "E29.132.4", {"start": v(137, -14.4) * mm, "end": v(141.89, -14.91) * mm});
            skLineSegment(sketch, "E29.132.5", {"start": v(141.28, -19.86) * mm, "end": v(141.35, -19.37) * mm});
            skArc(sketch, "E29.132.6", {"start": v(141.35, -19.37) * mm, "mid": v(141.24, -19.02) * mm, "end": v(140.91, -18.86) * mm});
            skArc(sketch, "E29.132.7", {"start": v(141.3, -15.8) * mm, "mid": v(141.65, -15.72) * mm, "end": v(141.83, -15.4) * mm});
            skLineSegment(sketch, "E29.132.8", {"start": v(141.83, -15.4) * mm, "end": v(141.89, -14.91) * mm});
            skArc(sketch, "E29.133.0", {"start": v(141.76, -10.85) * mm, "mid": v(139.95, -12.24) * mm, "end": v(141.49, -13.93) * mm});
            skLineSegment(sketch, "E29.133.1", {"start": v(142.32, -9.95) * mm, "end": v(137.41, -9.6) * mm, "construction": true});
            skLineSegment(sketch, "E29.133.2", {"start": v(141.89, -14.91) * mm, "end": v(136.91, -14.39) * mm});
            skLineSegment(sketch, "E29.133.3", {"start": v(137.41, -9.6) * mm, "end": v(136.91, -14.39) * mm});
            skLineSegment(sketch, "E29.133.4", {"start": v(137.41, -9.6) * mm, "end": v(142.32, -9.95) * mm});
            skLineSegment(sketch, "E29.133.5", {"start": v(141.89, -14.91) * mm, "end": v(141.94, -14.43) * mm});
            skArc(sketch, "E29.133.6", {"start": v(141.94, -14.43) * mm, "mid": v(141.82, -14.08) * mm, "end": v(141.49, -13.93) * mm});
            skArc(sketch, "E29.133.7", {"start": v(141.76, -10.85) * mm, "mid": v(142.11, -10.76) * mm, "end": v(142.29, -10.44) * mm});
            skLineSegment(sketch, "E29.133.8", {"start": v(142.29, -10.44) * mm, "end": v(142.32, -9.95) * mm});
            skArc(sketch, "E29.134.0", {"start": v(142.05, -5.9) * mm, "mid": v(140.3, -7.35) * mm, "end": v(141.89, -8.98) * mm});
            skLineSegment(sketch, "E29.134.1", {"start": v(142.58, -4.98) * mm, "end": v(137.67, -4.8) * mm, "construction": true});
            skLineSegment(sketch, "E29.134.2", {"start": v(142.32, -9.95) * mm, "end": v(137.33, -9.6) * mm});
            skLineSegment(sketch, "E29.134.3", {"start": v(137.67, -4.8) * mm, "end": v(137.33, -9.6) * mm});
            skLineSegment(sketch, "E29.134.4", {"start": v(137.67, -4.8) * mm, "end": v(142.58, -4.98) * mm});
            skLineSegment(sketch, "E29.134.5", {"start": v(142.32, -9.95) * mm, "end": v(142.35, -9.46) * mm});
            skArc(sketch, "E29.134.6", {"start": v(142.35, -9.46) * mm, "mid": v(142.23, -9.12) * mm, "end": v(141.89, -8.98) * mm});
            skArc(sketch, "E29.134.7", {"start": v(142.05, -5.9) * mm, "mid": v(142.4, -5.8) * mm, "end": v(142.56, -5.47) * mm});
            skLineSegment(sketch, "E29.134.8", {"start": v(142.56, -5.47) * mm, "end": v(142.58, -4.98) * mm});
            skArc(sketch, "E29.135.0", {"start": v(142.17, -0.94) * mm, "mid": v(140.46, -2.45) * mm, "end": v(142.11, -4.02) * mm});
            skLineSegment(sketch, "E29.135.1", {"start": v(142.67, 0) * mm, "end": v(137.75, 0) * mm, "construction": true});
            skLineSegment(sketch, "E29.135.2", {"start": v(142.58, -4.98) * mm, "end": v(137.58, -4.8) * mm});
            skLineSegment(sketch, "E29.135.3", {"start": v(137.75, 0) * mm, "end": v(137.58, -4.8) * mm});
            skLineSegment(sketch, "E29.135.4", {"start": v(137.75, 0) * mm, "end": v(142.67, 0) * mm});
            skLineSegment(sketch, "E29.135.5", {"start": v(142.58, -4.98) * mm, "end": v(142.6, -4.5) * mm});
            skArc(sketch, "E29.135.6", {"start": v(142.6, -4.5) * mm, "mid": v(142.46, -4.15) * mm, "end": v(142.11, -4.02) * mm});
            skArc(sketch, "E29.135.7", {"start": v(142.17, -0.94) * mm, "mid": v(142.52, -0.82) * mm, "end": v(142.67, -0.49) * mm});
            skLineSegment(sketch, "E29.135.8", {"start": v(142.67, -0.49) * mm, "end": v(142.67, 0) * mm});
            skArc(sketch, "E29.136.0", {"start": v(142.11, 4.02) * mm, "mid": v(140.46, 2.45) * mm, "end": v(142.17, 0.94) * mm});
            skLineSegment(sketch, "E29.136.1", {"start": v(142.58, 4.98) * mm, "end": v(137.67, 4.8) * mm, "construction": true});
            skLineSegment(sketch, "E29.136.2", {"start": v(142.67, 0) * mm, "end": v(137.67, 0) * mm});
            skLineSegment(sketch, "E29.136.3", {"start": v(137.67, 4.8) * mm, "end": v(137.67, 0) * mm});
            skLineSegment(sketch, "E29.136.4", {"start": v(137.67, 4.8) * mm, "end": v(142.58, 4.98) * mm});
            skLineSegment(sketch, "E29.136.5", {"start": v(142.67, 0) * mm, "end": v(142.67, 0.49) * mm});
            skArc(sketch, "E29.136.6", {"start": v(142.67, 0.49) * mm, "mid": v(142.52, 0.82) * mm, "end": v(142.17, 0.94) * mm});
            skArc(sketch, "E29.136.7", {"start": v(142.11, 4.02) * mm, "mid": v(142.46, 4.15) * mm, "end": v(142.6, 4.5) * mm});
            skLineSegment(sketch, "E29.136.8", {"start": v(142.6, 4.5) * mm, "end": v(142.58, 4.98) * mm});
            skArc(sketch, "E29.137.0", {"start": v(141.89, 8.98) * mm, "mid": v(140.3, 7.35) * mm, "end": v(142.05, 5.9) * mm});
            skLineSegment(sketch, "E29.137.1", {"start": v(142.32, 9.95) * mm, "end": v(137.41, 9.6) * mm, "construction": true});
            skLineSegment(sketch, "E29.137.2", {"start": v(142.58, 4.98) * mm, "end": v(137.58, 4.8) * mm});
            skLineSegment(sketch, "E29.137.3", {"start": v(137.41, 9.6) * mm, "end": v(137.58, 4.8) * mm});
            skLineSegment(sketch, "E29.137.4", {"start": v(137.41, 9.6) * mm, "end": v(142.32, 9.95) * mm});
            skLineSegment(sketch, "E29.137.5", {"start": v(142.58, 4.98) * mm, "end": v(142.56, 5.47) * mm});
            skArc(sketch, "E29.137.6", {"start": v(142.56, 5.47) * mm, "mid": v(142.4, 5.8) * mm, "end": v(142.05, 5.9) * mm});
            skArc(sketch, "E29.137.7", {"start": v(141.89, 8.98) * mm, "mid": v(142.23, 9.12) * mm, "end": v(142.35, 9.46) * mm});
            skLineSegment(sketch, "E29.137.8", {"start": v(142.35, 9.46) * mm, "end": v(142.32, 9.95) * mm});
            skArc(sketch, "E29.138.0", {"start": v(141.49, 13.93) * mm, "mid": v(139.95, 12.24) * mm, "end": v(141.76, 10.85) * mm});
            skLineSegment(sketch, "E29.138.1", {"start": v(141.89, 14.91) * mm, "end": v(137, 14.4) * mm, "construction": true});
            skLineSegment(sketch, "E29.138.2", {"start": v(142.32, 9.95) * mm, "end": v(137.33, 9.6) * mm});
            skLineSegment(sketch, "E29.138.3", {"start": v(137, 14.4) * mm, "end": v(137.33, 9.6) * mm});
            skLineSegment(sketch, "E29.138.4", {"start": v(137, 14.4) * mm, "end": v(141.89, 14.91) * mm});
            skLineSegment(sketch, "E29.138.5", {"start": v(142.32, 9.95) * mm, "end": v(142.29, 10.44) * mm});
            skArc(sketch, "E29.138.6", {"start": v(142.29, 10.44) * mm, "mid": v(142.11, 10.76) * mm, "end": v(141.76, 10.85) * mm});
            skArc(sketch, "E29.138.7", {"start": v(141.49, 13.93) * mm, "mid": v(141.82, 14.08) * mm, "end": v(141.94, 14.43) * mm});
            skLineSegment(sketch, "E29.138.8", {"start": v(141.94, 14.43) * mm, "end": v(141.89, 14.91) * mm});
            skArc(sketch, "E29.139.0", {"start": v(140.91, 18.86) * mm, "mid": v(139.44, 17.12) * mm, "end": v(141.3, 15.8) * mm});
            skLineSegment(sketch, "E29.139.1", {"start": v(141.28, 19.86) * mm, "end": v(136.4, 19.17) * mm, "construction": true});
            skLineSegment(sketch, "E29.139.2", {"start": v(141.89, 14.91) * mm, "end": v(136.91, 14.39) * mm});
            skLineSegment(sketch, "E29.139.3", {"start": v(136.4, 19.17) * mm, "end": v(136.91, 14.39) * mm});
            skLineSegment(sketch, "E29.139.4", {"start": v(136.4, 19.17) * mm, "end": v(141.28, 19.86) * mm});
            skLineSegment(sketch, "E29.139.5", {"start": v(141.89, 14.91) * mm, "end": v(141.83, 15.4) * mm});
            skArc(sketch, "E29.139.6", {"start": v(141.83, 15.4) * mm, "mid": v(141.65, 15.72) * mm, "end": v(141.3, 15.8) * mm});
            skArc(sketch, "E29.139.7", {"start": v(140.91, 18.86) * mm, "mid": v(141.24, 19.02) * mm, "end": v(141.35, 19.37) * mm});
            skLineSegment(sketch, "E29.139.8", {"start": v(141.35, 19.37) * mm, "end": v(141.28, 19.86) * mm});
            skArc(sketch, "E29.140.0", {"start": v(140.17, 23.76) * mm, "mid": v(138.75, 21.98) * mm, "end": v(140.65, 20.72) * mm});
            skLineSegment(sketch, "E29.140.1", {"start": v(140.5, 24.77) * mm, "end": v(135.66, 23.92) * mm, "construction": true});
            skLineSegment(sketch, "E29.140.2", {"start": v(141.28, 19.86) * mm, "end": v(136.33, 19.16) * mm});
            skLineSegment(sketch, "E29.140.3", {"start": v(135.66, 23.92) * mm, "end": v(136.33, 19.16) * mm});
            skLineSegment(sketch, "E29.140.4", {"start": v(135.66, 23.92) * mm, "end": v(140.5, 24.77) * mm});
            skLineSegment(sketch, "E29.140.5", {"start": v(141.28, 19.86) * mm, "end": v(141.21, 20.34) * mm});
            skArc(sketch, "E29.140.6", {"start": v(141.21, 20.34) * mm, "mid": v(141.02, 20.65) * mm, "end": v(140.65, 20.72) * mm});
            skArc(sketch, "E29.140.7", {"start": v(140.17, 23.76) * mm, "mid": v(140.5, 23.94) * mm, "end": v(140.58, 24.3) * mm});
            skLineSegment(sketch, "E29.140.8", {"start": v(140.58, 24.3) * mm, "end": v(140.5, 24.77) * mm});
            skArc(sketch, "E29.141.0", {"start": v(139.26, 28.64) * mm, "mid": v(137.9, 26.8) * mm, "end": v(139.84, 25.61) * mm});
            skLineSegment(sketch, "E29.141.1", {"start": v(139.55, 29.66) * mm, "end": v(134.74, 28.64) * mm, "construction": true});
            skLineSegment(sketch, "E29.141.2", {"start": v(140.5, 24.77) * mm, "end": v(135.57, 23.9) * mm});
            skLineSegment(sketch, "E29.141.3", {"start": v(134.74, 28.64) * mm, "end": v(135.57, 23.9) * mm});
            skLineSegment(sketch, "E29.141.4", {"start": v(134.74, 28.64) * mm, "end": v(139.55, 29.66) * mm});
            skLineSegment(sketch, "E29.141.5", {"start": v(140.5, 24.77) * mm, "end": v(140.41, 25.25) * mm});
            skArc(sketch, "E29.141.6", {"start": v(140.41, 25.25) * mm, "mid": v(140.2, 25.56) * mm, "end": v(139.84, 25.61) * mm});
            skArc(sketch, "E29.141.7", {"start": v(139.26, 28.64) * mm, "mid": v(139.57, 28.82) * mm, "end": v(139.65, 29.18) * mm});
            skLineSegment(sketch, "E29.141.8", {"start": v(139.65, 29.18) * mm, "end": v(139.55, 29.66) * mm});
            skArc(sketch, "E29.142.0", {"start": v(138.17, 33.48) * mm, "mid": v(136.88, 31.6) * mm, "end": v(138.87, 30.48) * mm});
            skLineSegment(sketch, "E29.142.1", {"start": v(138.43, 34.51) * mm, "end": v(133.66, 33.32) * mm, "construction": true});
            skLineSegment(sketch, "E29.142.2", {"start": v(139.55, 29.66) * mm, "end": v(134.66, 28.62) * mm});
            skLineSegment(sketch, "E29.142.3", {"start": v(133.66, 33.32) * mm, "end": v(134.66, 28.62) * mm});
            skLineSegment(sketch, "E29.142.4", {"start": v(133.66, 33.32) * mm, "end": v(138.43, 34.51) * mm});
            skLineSegment(sketch, "E29.142.5", {"start": v(139.55, 29.66) * mm, "end": v(139.45, 30.14) * mm});
            skArc(sketch, "E29.142.6", {"start": v(139.45, 30.14) * mm, "mid": v(139.23, 30.44) * mm, "end": v(138.87, 30.48) * mm});
            skArc(sketch, "E29.142.7", {"start": v(138.17, 33.48) * mm, "mid": v(138.48, 33.68) * mm, "end": v(138.55, 34.04) * mm});
            skLineSegment(sketch, "E29.142.8", {"start": v(138.55, 34.04) * mm, "end": v(138.43, 34.51) * mm});
            skArc(sketch, "E29.143.0", {"start": v(136.92, 38.28) * mm, "mid": v(135.7, 36.36) * mm, "end": v(137.72, 35.3) * mm});
            skLineSegment(sketch, "E29.143.1", {"start": v(137.14, 39.32) * mm, "end": v(132.41, 37.97) * mm, "construction": true});
            skLineSegment(sketch, "E29.143.2", {"start": v(138.43, 34.51) * mm, "end": v(133.58, 33.3) * mm});
            skLineSegment(sketch, "E29.143.3", {"start": v(132.41, 37.97) * mm, "end": v(133.58, 33.3) * mm});
            skLineSegment(sketch, "E29.143.4", {"start": v(132.41, 37.97) * mm, "end": v(137.14, 39.32) * mm});
            skLineSegment(sketch, "E29.143.5", {"start": v(138.43, 34.51) * mm, "end": v(138.31, 34.99) * mm});
            skArc(sketch, "E29.143.6", {"start": v(138.31, 34.99) * mm, "mid": v(138.08, 35.28) * mm, "end": v(137.72, 35.3) * mm});
            skArc(sketch, "E29.143.7", {"start": v(136.92, 38.28) * mm, "mid": v(137.22, 38.5) * mm, "end": v(137.28, 38.85) * mm});
            skLineSegment(sketch, "E29.143.8", {"start": v(137.28, 38.85) * mm, "end": v(137.14, 39.32) * mm});
            skArc(sketch, "E29.144.0", {"start": v(135.5, 43.04) * mm, "mid": v(134.35, 41.07) * mm, "end": v(136.4, 40.09) * mm});
            skLineSegment(sketch, "E29.144.1", {"start": v(135.69, 44.09) * mm, "end": v(131, 42.57) * mm, "construction": true});
            skLineSegment(sketch, "E29.144.2", {"start": v(137.14, 39.32) * mm, "end": v(132.33, 37.95) * mm});
            skLineSegment(sketch, "E29.144.3", {"start": v(131, 42.57) * mm, "end": v(132.33, 37.95) * mm});
            skLineSegment(sketch, "E29.144.4", {"start": v(131, 42.57) * mm, "end": v(135.69, 44.09) * mm});
            skLineSegment(sketch, "E29.144.5", {"start": v(137.14, 39.32) * mm, "end": v(137, 39.8) * mm});
            skArc(sketch, "E29.144.6", {"start": v(137, 39.8) * mm, "mid": v(136.77, 40.08) * mm, "end": v(136.4, 40.09) * mm});
            skArc(sketch, "E29.144.7", {"start": v(135.5, 43.04) * mm, "mid": v(135.8, 43.26) * mm, "end": v(135.84, 43.62) * mm});
            skLineSegment(sketch, "E29.144.8", {"start": v(135.84, 43.62) * mm, "end": v(135.69, 44.09) * mm});
            skArc(sketch, "E29.145.0", {"start": v(133.91, 47.74) * mm, "mid": v(132.83, 45.74) * mm, "end": v(134.92, 44.82) * mm});
            skLineSegment(sketch, "E29.145.1", {"start": v(134.06, 48.8) * mm, "end": v(129.44, 47.11) * mm, "construction": true});
            skLineSegment(sketch, "E29.145.2", {"start": v(135.69, 44.09) * mm, "end": v(130.93, 42.54) * mm});
            skLineSegment(sketch, "E29.145.3", {"start": v(129.44, 47.11) * mm, "end": v(130.93, 42.54) * mm});
            skLineSegment(sketch, "E29.145.4", {"start": v(129.44, 47.11) * mm, "end": v(134.06, 48.8) * mm});
            skLineSegment(sketch, "E29.145.5", {"start": v(135.69, 44.09) * mm, "end": v(135.53, 44.55) * mm});
            skArc(sketch, "E29.145.6", {"start": v(135.53, 44.55) * mm, "mid": v(135.29, 44.82) * mm, "end": v(134.92, 44.82) * mm});
            skArc(sketch, "E29.145.7", {"start": v(133.91, 47.74) * mm, "mid": v(134.2, 47.97) * mm, "end": v(134.23, 48.34) * mm});
            skLineSegment(sketch, "E29.145.8", {"start": v(134.23, 48.34) * mm, "end": v(134.06, 48.8) * mm});
            skArc(sketch, "E29.146.0", {"start": v(132.17, 52.39) * mm, "mid": v(131.15, 50.35) * mm, "end": v(133.27, 49.5) * mm});
            skLineSegment(sketch, "E29.146.1", {"start": v(132.28, 53.44) * mm, "end": v(127.72, 51.6) * mm, "construction": true});
            skLineSegment(sketch, "E29.146.2", {"start": v(134.06, 48.8) * mm, "end": v(129.36, 47.08) * mm});
            skLineSegment(sketch, "E29.146.3", {"start": v(127.72, 51.6) * mm, "end": v(129.36, 47.08) * mm});
            skLineSegment(sketch, "E29.146.4", {"start": v(127.72, 51.6) * mm, "end": v(132.28, 53.44) * mm});
            skLineSegment(sketch, "E29.146.5", {"start": v(134.06, 48.8) * mm, "end": v(133.9, 49.25) * mm});
            skArc(sketch, "E29.146.6", {"start": v(133.9, 49.25) * mm, "mid": v(133.64, 49.52) * mm, "end": v(133.27, 49.5) * mm});
            skArc(sketch, "E29.146.7", {"start": v(132.17, 52.39) * mm, "mid": v(132.45, 52.62) * mm, "end": v(132.46, 53) * mm});
            skLineSegment(sketch, "E29.146.8", {"start": v(132.46, 53) * mm, "end": v(132.28, 53.44) * mm});
            skArc(sketch, "E29.147.0", {"start": v(130.26, 56.97) * mm, "mid": v(129.32, 54.9) * mm, "end": v(131.46, 54.13) * mm});
            skLineSegment(sketch, "E29.147.1", {"start": v(130.33, 58.03) * mm, "end": v(125.84, 56.03) * mm, "construction": true});
            skLineSegment(sketch, "E29.147.2", {"start": v(132.28, 53.44) * mm, "end": v(127.64, 51.57) * mm});
            skLineSegment(sketch, "E29.147.3", {"start": v(125.84, 56.03) * mm, "end": v(127.64, 51.57) * mm});
            skLineSegment(sketch, "E29.147.4", {"start": v(125.84, 56.03) * mm, "end": v(130.33, 58.03) * mm});
            skLineSegment(sketch, "E29.147.5", {"start": v(132.28, 53.44) * mm, "end": v(132.1, 53.9) * mm});
            skArc(sketch, "E29.147.6", {"start": v(132.1, 53.9) * mm, "mid": v(131.83, 54.15) * mm, "end": v(131.46, 54.13) * mm});
            skArc(sketch, "E29.147.7", {"start": v(130.26, 56.97) * mm, "mid": v(130.53, 57.21) * mm, "end": v(130.53, 57.58) * mm});
            skLineSegment(sketch, "E29.147.8", {"start": v(130.53, 57.58) * mm, "end": v(130.33, 58.03) * mm});
            skArc(sketch, "E29.148.0", {"start": v(128.2, 61.48) * mm, "mid": v(127.32, 59.37) * mm, "end": v(129.5, 58.68) * mm});
            skLineSegment(sketch, "E29.148.1", {"start": v(128.23, 62.54) * mm, "end": v(123.8, 60.39) * mm, "construction": true});
            skLineSegment(sketch, "E29.148.2", {"start": v(130.33, 58.03) * mm, "end": v(125.76, 56) * mm});
            skLineSegment(sketch, "E29.148.3", {"start": v(123.8, 60.39) * mm, "end": v(125.76, 56) * mm});
            skLineSegment(sketch, "E29.148.4", {"start": v(123.8, 60.39) * mm, "end": v(128.23, 62.54) * mm});
            skLineSegment(sketch, "E29.148.5", {"start": v(130.33, 58.03) * mm, "end": v(130.13, 58.47) * mm});
            skArc(sketch, "E29.148.6", {"start": v(130.13, 58.47) * mm, "mid": v(129.86, 58.72) * mm, "end": v(129.5, 58.68) * mm});
            skArc(sketch, "E29.148.7", {"start": v(128.2, 61.48) * mm, "mid": v(128.45, 61.73) * mm, "end": v(128.44, 62.1) * mm});
            skLineSegment(sketch, "E29.148.8", {"start": v(128.44, 62.1) * mm, "end": v(128.23, 62.54) * mm});
            skArc(sketch, "E29.149.0", {"start": v(125.97, 65.91) * mm, "mid": v(125.17, 63.78) * mm, "end": v(127.37, 63.17) * mm});
            skLineSegment(sketch, "E29.149.1", {"start": v(125.97, 66.98) * mm, "end": v(121.63, 64.67) * mm, "construction": true});
            skLineSegment(sketch, "E29.149.2", {"start": v(128.23, 62.54) * mm, "end": v(123.73, 60.35) * mm});
            skLineSegment(sketch, "E29.149.3", {"start": v(121.63, 64.67) * mm, "end": v(123.73, 60.35) * mm});
            skLineSegment(sketch, "E29.149.4", {"start": v(121.63, 64.67) * mm, "end": v(125.97, 66.98) * mm});
            skLineSegment(sketch, "E29.149.5", {"start": v(128.23, 62.54) * mm, "end": v(128.01, 62.98) * mm});
            skArc(sketch, "E29.149.6", {"start": v(128.01, 62.98) * mm, "mid": v(127.73, 63.22) * mm, "end": v(127.37, 63.17) * mm});
            skArc(sketch, "E29.149.7", {"start": v(125.97, 65.91) * mm, "mid": v(126.22, 66.18) * mm, "end": v(126.2, 66.55) * mm});
            skLineSegment(sketch, "E29.149.8", {"start": v(126.2, 66.55) * mm, "end": v(125.97, 66.98) * mm});
            skArc(sketch, "E29.150.0", {"start": v(123.59, 70.27) * mm, "mid": v(122.87, 68.1) * mm, "end": v(125.09, 67.57) * mm});
            skLineSegment(sketch, "E29.150.1", {"start": v(123.55, 71.33) * mm, "end": v(119.3, 68.87) * mm, "construction": true});
            skLineSegment(sketch, "E29.150.2", {"start": v(125.97, 66.98) * mm, "end": v(121.55, 64.63) * mm});
            skLineSegment(sketch, "E29.150.3", {"start": v(119.3, 68.87) * mm, "end": v(121.55, 64.63) * mm});
            skLineSegment(sketch, "E29.150.4", {"start": v(119.3, 68.87) * mm, "end": v(123.55, 71.33) * mm});
            skLineSegment(sketch, "E29.150.5", {"start": v(125.97, 66.98) * mm, "end": v(125.74, 67.4) * mm});
            skArc(sketch, "E29.150.6", {"start": v(125.74, 67.4) * mm, "mid": v(125.45, 67.64) * mm, "end": v(125.09, 67.57) * mm});
            skArc(sketch, "E29.150.7", {"start": v(123.59, 70.27) * mm, "mid": v(123.84, 70.54) * mm, "end": v(123.8, 70.91) * mm});
            skLineSegment(sketch, "E29.150.8", {"start": v(123.8, 70.91) * mm, "end": v(123.55, 71.33) * mm});
            skArc(sketch, "E29.151.0", {"start": v(121.06, 74.54) * mm, "mid": v(120.42, 72.35) * mm, "end": v(122.65, 71.9) * mm});
            skLineSegment(sketch, "E29.151.1", {"start": v(120.99, 75.6) * mm, "end": v(116.82, 73) * mm, "construction": true});
            skLineSegment(sketch, "E29.151.2", {"start": v(123.55, 71.33) * mm, "end": v(119.22, 68.83) * mm});
            skLineSegment(sketch, "E29.151.3", {"start": v(116.82, 73) * mm, "end": v(119.22, 68.83) * mm});
            skLineSegment(sketch, "E29.151.4", {"start": v(116.82, 73) * mm, "end": v(120.99, 75.6) * mm});
            skLineSegment(sketch, "E29.151.5", {"start": v(123.55, 71.33) * mm, "end": v(123.3, 71.76) * mm});
            skArc(sketch, "E29.151.6", {"start": v(123.3, 71.76) * mm, "mid": v(123.01, 71.97) * mm, "end": v(122.65, 71.9) * mm});
            skArc(sketch, "E29.151.7", {"start": v(121.06, 74.54) * mm, "mid": v(121.3, 74.82) * mm, "end": v(121.25, 75.19) * mm});
            skLineSegment(sketch, "E29.151.8", {"start": v(121.25, 75.19) * mm, "end": v(120.99, 75.6) * mm});
            skArc(sketch, "E29.152.0", {"start": v(118.39, 78.72) * mm, "mid": v(117.82, 76.51) * mm, "end": v(120.07, 76.13) * mm});
            skLineSegment(sketch, "E29.152.1", {"start": v(118.28, 79.78) * mm, "end": v(114.2, 77.03) * mm, "construction": true});
            skLineSegment(sketch, "E29.152.2", {"start": v(120.99, 75.6) * mm, "end": v(116.75, 72.95) * mm});
            skLineSegment(sketch, "E29.152.3", {"start": v(114.2, 77.03) * mm, "end": v(116.75, 72.95) * mm});
            skLineSegment(sketch, "E29.152.4", {"start": v(114.2, 77.03) * mm, "end": v(118.28, 79.78) * mm});
            skLineSegment(sketch, "E29.152.5", {"start": v(120.99, 75.6) * mm, "end": v(120.73, 76.02) * mm});
            skArc(sketch, "E29.152.6", {"start": v(120.73, 76.02) * mm, "mid": v(120.42, 76.22) * mm, "end": v(120.07, 76.13) * mm});
            skArc(sketch, "E29.152.7", {"start": v(118.39, 78.72) * mm, "mid": v(118.61, 79.01) * mm, "end": v(118.55, 79.37) * mm});
            skLineSegment(sketch, "E29.152.8", {"start": v(118.55, 79.37) * mm, "end": v(118.28, 79.78) * mm});
            skArc(sketch, "E29.153.0", {"start": v(115.57, 82.8) * mm, "mid": v(115.08, 80.58) * mm, "end": v(117.34, 80.28) * mm});
            skLineSegment(sketch, "E29.153.1", {"start": v(115.42, 83.86) * mm, "end": v(111.44, 80.97) * mm, "construction": true});
            skLineSegment(sketch, "E29.153.2", {"start": v(118.28, 79.78) * mm, "end": v(114.13, 76.98) * mm});
            skLineSegment(sketch, "E29.153.3", {"start": v(111.44, 80.97) * mm, "end": v(114.13, 76.98) * mm});
            skLineSegment(sketch, "E29.153.4", {"start": v(111.44, 80.97) * mm, "end": v(115.42, 83.86) * mm});
            skLineSegment(sketch, "E29.153.5", {"start": v(118.28, 79.78) * mm, "end": v(118, 80.18) * mm});
            skArc(sketch, "E29.153.6", {"start": v(118, 80.18) * mm, "mid": v(117.7, 80.38) * mm, "end": v(117.34, 80.28) * mm});
            skArc(sketch, "E29.153.7", {"start": v(115.57, 82.8) * mm, "mid": v(115.78, 83.1) * mm, "end": v(115.7, 83.46) * mm});
            skLineSegment(sketch, "E29.153.8", {"start": v(115.7, 83.46) * mm, "end": v(115.42, 83.86) * mm});
            skArc(sketch, "E29.154.0", {"start": v(112.6, 86.79) * mm, "mid": v(112.2, 84.55) * mm, "end": v(114.46, 84.32) * mm});
            skLineSegment(sketch, "E29.154.1", {"start": v(112.42, 87.84) * mm, "end": v(108.55, 84.8) * mm, "construction": true});
            skLineSegment(sketch, "E29.154.2", {"start": v(115.42, 83.86) * mm, "end": v(111.37, 80.92) * mm});
            skLineSegment(sketch, "E29.154.3", {"start": v(108.55, 84.8) * mm, "end": v(111.37, 80.92) * mm});
            skLineSegment(sketch, "E29.154.4", {"start": v(108.55, 84.8) * mm, "end": v(112.42, 87.84) * mm});
            skLineSegment(sketch, "E29.154.5", {"start": v(115.42, 83.86) * mm, "end": v(115.13, 84.25) * mm});
            skArc(sketch, "E29.154.6", {"start": v(115.13, 84.25) * mm, "mid": v(114.81, 84.44) * mm, "end": v(114.46, 84.32) * mm});
            skArc(sketch, "E29.154.7", {"start": v(112.6, 86.79) * mm, "mid": v(112.81, 87.1) * mm, "end": v(112.72, 87.45) * mm});
            skLineSegment(sketch, "E29.154.8", {"start": v(112.72, 87.45) * mm, "end": v(112.42, 87.84) * mm});
            skArc(sketch, "E29.155.0", {"start": v(109.5, 90.66) * mm, "mid": v(109.18, 88.4) * mm, "end": v(111.45, 88.27) * mm});
            skLineSegment(sketch, "E29.155.1", {"start": v(109.29, 91.7) * mm, "end": v(105.52, 88.54) * mm, "construction": true});
            skLineSegment(sketch, "E29.155.2", {"start": v(112.42, 87.84) * mm, "end": v(108.48, 84.76) * mm});
            skLineSegment(sketch, "E29.155.3", {"start": v(105.52, 88.54) * mm, "end": v(108.48, 84.76) * mm});
            skLineSegment(sketch, "E29.155.4", {"start": v(105.52, 88.54) * mm, "end": v(109.29, 91.7) * mm});
            skLineSegment(sketch, "E29.155.5", {"start": v(112.42, 87.84) * mm, "end": v(112.12, 88.22) * mm});
            skArc(sketch, "E29.155.6", {"start": v(112.12, 88.22) * mm, "mid": v(111.8, 88.4) * mm, "end": v(111.45, 88.27) * mm});
            skArc(sketch, "E29.155.7", {"start": v(109.5, 90.66) * mm, "mid": v(109.7, 90.98) * mm, "end": v(109.6, 91.33) * mm});
            skLineSegment(sketch, "E29.155.8", {"start": v(109.6, 91.33) * mm, "end": v(109.29, 91.7) * mm});
            skArc(sketch, "E29.156.0", {"start": v(106.28, 94.43) * mm, "mid": v(106.02, 92.17) * mm, "end": v(108.3, 92.1) * mm});
            skLineSegment(sketch, "E29.156.1", {"start": v(106.02, 95.46) * mm, "end": v(102.37, 92.17) * mm, "construction": true});
            skLineSegment(sketch, "E29.156.2", {"start": v(109.3, 91.7) * mm, "end": v(105.46, 88.49) * mm});
            skLineSegment(sketch, "E29.156.3", {"start": v(102.37, 92.17) * mm, "end": v(105.46, 88.49) * mm});
            skLineSegment(sketch, "E29.156.4", {"start": v(102.37, 92.17) * mm, "end": v(106.02, 95.46) * mm});
            skLineSegment(sketch, "E29.156.5", {"start": v(109.3, 91.7) * mm, "end": v(108.98, 92.08) * mm});
            skArc(sketch, "E29.156.6", {"start": v(108.98, 92.08) * mm, "mid": v(108.64, 92.24) * mm, "end": v(108.3, 92.1) * mm});
            skArc(sketch, "E29.156.7", {"start": v(106.28, 94.43) * mm, "mid": v(106.46, 94.75) * mm, "end": v(106.35, 95.1) * mm});
            skLineSegment(sketch, "E29.156.8", {"start": v(106.35, 95.1) * mm, "end": v(106.02, 95.46) * mm});
            skArc(sketch, "E29.157.0", {"start": v(102.92, 98.08) * mm, "mid": v(102.74, 95.81) * mm, "end": v(105.02, 95.83) * mm});
            skLineSegment(sketch, "E29.157.1", {"start": v(102.63, 99.1) * mm, "end": v(99.09, 95.69) * mm, "construction": true});
            skLineSegment(sketch, "E29.157.2", {"start": v(106.02, 95.46) * mm, "end": v(102.3, 92.12) * mm});
            skLineSegment(sketch, "E29.157.3", {"start": v(99.09, 95.69) * mm, "end": v(102.3, 92.12) * mm});
            skLineSegment(sketch, "E29.157.4", {"start": v(99.09, 95.69) * mm, "end": v(102.63, 99.1) * mm});
            skLineSegment(sketch, "E29.157.5", {"start": v(106.02, 95.46) * mm, "end": v(105.7, 95.83) * mm});
            skArc(sketch, "E29.157.6", {"start": v(105.7, 95.83) * mm, "mid": v(105.36, 95.97) * mm, "end": v(105.02, 95.83) * mm});
            skArc(sketch, "E29.157.7", {"start": v(102.92, 98.08) * mm, "mid": v(103.1, 98.4) * mm, "end": v(102.97, 98.75) * mm});
            skLineSegment(sketch, "E29.157.8", {"start": v(102.97, 98.75) * mm, "end": v(102.63, 99.1) * mm});
            skArc(sketch, "E29.158.0", {"start": v(99.43, 101.61) * mm, "mid": v(99.34, 99.34) * mm, "end": v(101.61, 99.43) * mm});
            skLineSegment(sketch, "E29.158.1", {"start": v(99.1, 102.63) * mm, "end": v(95.69, 99.09) * mm, "construction": true});
            skLineSegment(sketch, "E29.158.2", {"start": v(102.63, 99.1) * mm, "end": v(99.03, 95.63) * mm});
            skLineSegment(sketch, "E29.158.3", {"start": v(95.69, 99.09) * mm, "end": v(99.03, 95.63) * mm});
            skLineSegment(sketch, "E29.158.4", {"start": v(95.69, 99.09) * mm, "end": v(99.1, 102.63) * mm});
            skLineSegment(sketch, "E29.158.5", {"start": v(102.63, 99.1) * mm, "end": v(102.29, 99.46) * mm});
            skArc(sketch, "E29.158.6", {"start": v(102.29, 99.46) * mm, "mid": v(101.95, 99.6) * mm, "end": v(101.61, 99.43) * mm});
            skArc(sketch, "E29.158.7", {"start": v(99.43, 101.61) * mm, "mid": v(99.6, 101.95) * mm, "end": v(99.46, 102.29) * mm});
            skLineSegment(sketch, "E29.158.8", {"start": v(99.46, 102.29) * mm, "end": v(99.1, 102.63) * mm});
            skArc(sketch, "E29.159.0", {"start": v(95.83, 105.02) * mm, "mid": v(95.81, 102.74) * mm, "end": v(98.08, 102.92) * mm});
            skLineSegment(sketch, "E29.159.1", {"start": v(95.46, 106.02) * mm, "end": v(92.17, 102.37) * mm, "construction": true});
            skLineSegment(sketch, "E29.159.2", {"start": v(99.1, 102.63) * mm, "end": v(95.63, 99.03) * mm});
            skLineSegment(sketch, "E29.159.3", {"start": v(92.17, 102.37) * mm, "end": v(95.63, 99.03) * mm});
            skLineSegment(sketch, "E29.159.4", {"start": v(92.17, 102.37) * mm, "end": v(95.46, 106.02) * mm});
            skLineSegment(sketch, "E29.159.5", {"start": v(99.1, 102.63) * mm, "end": v(98.75, 102.97) * mm});
            skArc(sketch, "E29.159.6", {"start": v(98.75, 102.97) * mm, "mid": v(98.4, 103.1) * mm, "end": v(98.08, 102.92) * mm});
            skArc(sketch, "E29.159.7", {"start": v(95.83, 105.02) * mm, "mid": v(95.97, 105.36) * mm, "end": v(95.83, 105.7) * mm});
            skLineSegment(sketch, "E29.159.8", {"start": v(95.83, 105.7) * mm, "end": v(95.46, 106.02) * mm});
            skArc(sketch, "E29.160.0", {"start": v(92.1, 108.3) * mm, "mid": v(92.17, 106.02) * mm, "end": v(94.43, 106.28) * mm});
            skLineSegment(sketch, "E29.160.1", {"start": v(91.7, 109.29) * mm, "end": v(88.54, 105.52) * mm, "construction": true});
            skLineSegment(sketch, "E29.160.2", {"start": v(95.46, 106.02) * mm, "end": v(92.12, 102.3) * mm});
            skLineSegment(sketch, "E29.160.3", {"start": v(88.54, 105.52) * mm, "end": v(92.12, 102.3) * mm});
            skLineSegment(sketch, "E29.160.4", {"start": v(88.54, 105.52) * mm, "end": v(91.7, 109.29) * mm});
            skLineSegment(sketch, "E29.160.5", {"start": v(95.46, 106.02) * mm, "end": v(95.1, 106.35) * mm});
            skArc(sketch, "E29.160.6", {"start": v(95.1, 106.35) * mm, "mid": v(94.75, 106.46) * mm, "end": v(94.43, 106.28) * mm});
            skArc(sketch, "E29.160.7", {"start": v(92.1, 108.3) * mm, "mid": v(92.24, 108.64) * mm, "end": v(92.08, 108.98) * mm});
            skLineSegment(sketch, "E29.160.8", {"start": v(92.08, 108.98) * mm, "end": v(91.7, 109.29) * mm});
            skArc(sketch, "E29.161.0", {"start": v(88.27, 111.45) * mm, "mid": v(88.4, 109.18) * mm, "end": v(90.66, 109.5) * mm});
            skLineSegment(sketch, "E29.161.1", {"start": v(87.84, 112.42) * mm, "end": v(84.8, 108.55) * mm, "construction": true});
            skLineSegment(sketch, "E29.161.2", {"start": v(91.7, 109.3) * mm, "end": v(88.49, 105.46) * mm});
            skLineSegment(sketch, "E29.161.3", {"start": v(84.8, 108.55) * mm, "end": v(88.49, 105.46) * mm});
            skLineSegment(sketch, "E29.161.4", {"start": v(84.8, 108.55) * mm, "end": v(87.84, 112.42) * mm});
            skLineSegment(sketch, "E29.161.5", {"start": v(91.7, 109.3) * mm, "end": v(91.33, 109.6) * mm});
            skArc(sketch, "E29.161.6", {"start": v(91.33, 109.6) * mm, "mid": v(90.98, 109.7) * mm, "end": v(90.66, 109.5) * mm});
            skArc(sketch, "E29.161.7", {"start": v(88.27, 111.45) * mm, "mid": v(88.4, 111.8) * mm, "end": v(88.22, 112.12) * mm});
            skLineSegment(sketch, "E29.161.8", {"start": v(88.22, 112.12) * mm, "end": v(87.84, 112.42) * mm});
            skArc(sketch, "E29.162.0", {"start": v(84.32, 114.46) * mm, "mid": v(84.55, 112.2) * mm, "end": v(86.79, 112.6) * mm});
            skLineSegment(sketch, "E29.162.1", {"start": v(83.86, 115.42) * mm, "end": v(80.97, 111.44) * mm, "construction": true});
            skLineSegment(sketch, "E29.162.2", {"start": v(87.84, 112.42) * mm, "end": v(84.76, 108.48) * mm});
            skLineSegment(sketch, "E29.162.3", {"start": v(80.97, 111.44) * mm, "end": v(84.76, 108.48) * mm});
            skLineSegment(sketch, "E29.162.4", {"start": v(80.97, 111.44) * mm, "end": v(83.86, 115.42) * mm});
            skLineSegment(sketch, "E29.162.5", {"start": v(87.84, 112.42) * mm, "end": v(87.45, 112.72) * mm});
            skArc(sketch, "E29.162.6", {"start": v(87.45, 112.72) * mm, "mid": v(87.1, 112.81) * mm, "end": v(86.79, 112.6) * mm});
            skArc(sketch, "E29.162.7", {"start": v(84.32, 114.46) * mm, "mid": v(84.44, 114.81) * mm, "end": v(84.25, 115.13) * mm});
            skLineSegment(sketch, "E29.162.8", {"start": v(84.25, 115.13) * mm, "end": v(83.86, 115.42) * mm});
            skArc(sketch, "E29.163.0", {"start": v(80.28, 117.34) * mm, "mid": v(80.58, 115.08) * mm, "end": v(82.8, 115.57) * mm});
            skLineSegment(sketch, "E29.163.1", {"start": v(79.78, 118.28) * mm, "end": v(77.03, 114.2) * mm, "construction": true});
            skLineSegment(sketch, "E29.163.2", {"start": v(83.86, 115.42) * mm, "end": v(80.92, 111.37) * mm});
            skLineSegment(sketch, "E29.163.3", {"start": v(77.03, 114.2) * mm, "end": v(80.92, 111.37) * mm});
            skLineSegment(sketch, "E29.163.4", {"start": v(77.03, 114.2) * mm, "end": v(79.78, 118.28) * mm});
            skLineSegment(sketch, "E29.163.5", {"start": v(83.86, 115.42) * mm, "end": v(83.46, 115.7) * mm});
            skArc(sketch, "E29.163.6", {"start": v(83.46, 115.7) * mm, "mid": v(83.1, 115.78) * mm, "end": v(82.8, 115.57) * mm});
            skArc(sketch, "E29.163.7", {"start": v(80.28, 117.34) * mm, "mid": v(80.38, 117.7) * mm, "end": v(80.18, 118) * mm});
            skLineSegment(sketch, "E29.163.8", {"start": v(80.18, 118) * mm, "end": v(79.78, 118.28) * mm});
            skArc(sketch, "E29.164.0", {"start": v(76.13, 120.07) * mm, "mid": v(76.51, 117.82) * mm, "end": v(78.72, 118.39) * mm});
            skLineSegment(sketch, "E29.164.1", {"start": v(75.6, 120.99) * mm, "end": v(73, 116.82) * mm, "construction": true});
            skLineSegment(sketch, "E29.164.2", {"start": v(79.78, 118.28) * mm, "end": v(76.98, 114.13) * mm});
            skLineSegment(sketch, "E29.164.3", {"start": v(73, 116.82) * mm, "end": v(76.98, 114.13) * mm});
            skLineSegment(sketch, "E29.164.4", {"start": v(73, 116.82) * mm, "end": v(75.6, 120.99) * mm});
            skLineSegment(sketch, "E29.164.5", {"start": v(79.78, 118.28) * mm, "end": v(79.37, 118.55) * mm});
            skArc(sketch, "E29.164.6", {"start": v(79.37, 118.55) * mm, "mid": v(79.01, 118.61) * mm, "end": v(78.72, 118.39) * mm});
            skArc(sketch, "E29.164.7", {"start": v(76.13, 120.07) * mm, "mid": v(76.22, 120.42) * mm, "end": v(76.02, 120.73) * mm});
            skLineSegment(sketch, "E29.164.8", {"start": v(76.02, 120.73) * mm, "end": v(75.6, 120.99) * mm});
            skArc(sketch, "E29.165.0", {"start": v(71.9, 122.65) * mm, "mid": v(72.35, 120.42) * mm, "end": v(74.54, 121.06) * mm});
            skLineSegment(sketch, "E29.165.1", {"start": v(71.33, 123.55) * mm, "end": v(68.87, 119.3) * mm, "construction": true});
            skLineSegment(sketch, "E29.165.2", {"start": v(75.6, 120.99) * mm, "end": v(72.95, 116.75) * mm});
            skLineSegment(sketch, "E29.165.3", {"start": v(68.87, 119.3) * mm, "end": v(72.95, 116.75) * mm});
            skLineSegment(sketch, "E29.165.4", {"start": v(68.87, 119.3) * mm, "end": v(71.33, 123.55) * mm});
            skLineSegment(sketch, "E29.165.5", {"start": v(75.6, 120.99) * mm, "end": v(75.19, 121.25) * mm});
            skArc(sketch, "E29.165.6", {"start": v(75.19, 121.25) * mm, "mid": v(74.82, 121.3) * mm, "end": v(74.54, 121.06) * mm});
            skArc(sketch, "E29.165.7", {"start": v(71.9, 122.65) * mm, "mid": v(71.97, 123.01) * mm, "end": v(71.76, 123.3) * mm});
            skLineSegment(sketch, "E29.165.8", {"start": v(71.76, 123.3) * mm, "end": v(71.33, 123.55) * mm});
            skArc(sketch, "E29.166.0", {"start": v(67.57, 125.09) * mm, "mid": v(68.1, 122.87) * mm, "end": v(70.27, 123.59) * mm});
            skLineSegment(sketch, "E29.166.1", {"start": v(66.98, 125.97) * mm, "end": v(64.67, 121.63) * mm, "construction": true});
            skLineSegment(sketch, "E29.166.2", {"start": v(71.33, 123.55) * mm, "end": v(68.83, 119.22) * mm});
            skLineSegment(sketch, "E29.166.3", {"start": v(64.67, 121.63) * mm, "end": v(68.83, 119.22) * mm});
            skLineSegment(sketch, "E29.166.4", {"start": v(64.67, 121.63) * mm, "end": v(66.98, 125.97) * mm});
            skLineSegment(sketch, "E29.166.5", {"start": v(71.33, 123.55) * mm, "end": v(70.91, 123.8) * mm});
            skArc(sketch, "E29.166.6", {"start": v(70.91, 123.8) * mm, "mid": v(70.54, 123.84) * mm, "end": v(70.27, 123.59) * mm});
            skArc(sketch, "E29.166.7", {"start": v(67.57, 125.09) * mm, "mid": v(67.64, 125.45) * mm, "end": v(67.4, 125.74) * mm});
            skLineSegment(sketch, "E29.166.8", {"start": v(67.4, 125.74) * mm, "end": v(66.98, 125.97) * mm});
            skArc(sketch, "E29.167.0", {"start": v(63.17, 127.37) * mm, "mid": v(63.78, 125.17) * mm, "end": v(65.91, 125.97) * mm});
            skLineSegment(sketch, "E29.167.1", {"start": v(62.54, 128.23) * mm, "end": v(60.39, 123.8) * mm, "construction": true});
            skLineSegment(sketch, "E29.167.2", {"start": v(66.98, 125.97) * mm, "end": v(64.63, 121.55) * mm});
            skLineSegment(sketch, "E29.167.3", {"start": v(60.39, 123.8) * mm, "end": v(64.63, 121.55) * mm});
            skLineSegment(sketch, "E29.167.4", {"start": v(60.39, 123.8) * mm, "end": v(62.54, 128.23) * mm});
            skLineSegment(sketch, "E29.167.5", {"start": v(66.98, 125.97) * mm, "end": v(66.55, 126.2) * mm});
            skArc(sketch, "E29.167.6", {"start": v(66.55, 126.2) * mm, "mid": v(66.18, 126.22) * mm, "end": v(65.91, 125.97) * mm});
            skArc(sketch, "E29.167.7", {"start": v(63.17, 127.37) * mm, "mid": v(63.22, 127.73) * mm, "end": v(62.98, 128.01) * mm});
            skLineSegment(sketch, "E29.167.8", {"start": v(62.98, 128.01) * mm, "end": v(62.54, 128.23) * mm});
            skArc(sketch, "E29.168.0", {"start": v(58.68, 129.5) * mm, "mid": v(59.37, 127.32) * mm, "end": v(61.48, 128.2) * mm});
            skLineSegment(sketch, "E29.168.1", {"start": v(58.03, 130.33) * mm, "end": v(56.03, 125.84) * mm, "construction": true});
            skLineSegment(sketch, "E29.168.2", {"start": v(62.54, 128.23) * mm, "end": v(60.35, 123.73) * mm});
            skLineSegment(sketch, "E29.168.3", {"start": v(56.03, 125.84) * mm, "end": v(60.35, 123.73) * mm});
            skLineSegment(sketch, "E29.168.4", {"start": v(56.03, 125.84) * mm, "end": v(58.03, 130.33) * mm});
            skLineSegment(sketch, "E29.168.5", {"start": v(62.54, 128.23) * mm, "end": v(62.1, 128.44) * mm});
            skArc(sketch, "E29.168.6", {"start": v(62.1, 128.44) * mm, "mid": v(61.73, 128.45) * mm, "end": v(61.48, 128.2) * mm});
            skArc(sketch, "E29.168.7", {"start": v(58.68, 129.5) * mm, "mid": v(58.72, 129.86) * mm, "end": v(58.47, 130.13) * mm});
            skLineSegment(sketch, "E29.168.8", {"start": v(58.47, 130.13) * mm, "end": v(58.03, 130.33) * mm});
            skArc(sketch, "E29.169.0", {"start": v(54.13, 131.46) * mm, "mid": v(54.9, 129.32) * mm, "end": v(56.97, 130.26) * mm});
            skLineSegment(sketch, "E29.169.1", {"start": v(53.44, 132.28) * mm, "end": v(51.6, 127.72) * mm, "construction": true});
            skLineSegment(sketch, "E29.169.2", {"start": v(58.03, 130.33) * mm, "end": v(56, 125.76) * mm});
            skLineSegment(sketch, "E29.169.3", {"start": v(51.6, 127.72) * mm, "end": v(56, 125.76) * mm});
            skLineSegment(sketch, "E29.169.4", {"start": v(51.6, 127.72) * mm, "end": v(53.44, 132.28) * mm});
            skLineSegment(sketch, "E29.169.5", {"start": v(58.03, 130.33) * mm, "end": v(57.58, 130.53) * mm});
            skArc(sketch, "E29.169.6", {"start": v(57.58, 130.53) * mm, "mid": v(57.21, 130.53) * mm, "end": v(56.97, 130.26) * mm});
            skArc(sketch, "E29.169.7", {"start": v(54.13, 131.46) * mm, "mid": v(54.15, 131.83) * mm, "end": v(53.9, 132.1) * mm});
            skLineSegment(sketch, "E29.169.8", {"start": v(53.9, 132.1) * mm, "end": v(53.44, 132.28) * mm});
            skArc(sketch, "E29.170.0", {"start": v(49.5, 133.27) * mm, "mid": v(50.35, 131.15) * mm, "end": v(52.39, 132.17) * mm});
            skLineSegment(sketch, "E29.170.1", {"start": v(48.8, 134.06) * mm, "end": v(47.11, 129.44) * mm, "construction": true});
            skLineSegment(sketch, "E29.170.2", {"start": v(53.44, 132.28) * mm, "end": v(51.57, 127.64) * mm});
            skLineSegment(sketch, "E29.170.3", {"start": v(47.11, 129.44) * mm, "end": v(51.57, 127.64) * mm});
            skLineSegment(sketch, "E29.170.4", {"start": v(47.11, 129.44) * mm, "end": v(48.8, 134.06) * mm});
            skLineSegment(sketch, "E29.170.5", {"start": v(53.44, 132.28) * mm, "end": v(53, 132.46) * mm});
            skArc(sketch, "E29.170.6", {"start": v(53, 132.46) * mm, "mid": v(52.62, 132.45) * mm, "end": v(52.39, 132.17) * mm});
            skArc(sketch, "E29.170.7", {"start": v(49.5, 133.27) * mm, "mid": v(49.52, 133.64) * mm, "end": v(49.25, 133.9) * mm});
            skLineSegment(sketch, "E29.170.8", {"start": v(49.25, 133.9) * mm, "end": v(48.8, 134.06) * mm});
            skArc(sketch, "E29.171.0", {"start": v(44.82, 134.92) * mm, "mid": v(45.74, 132.83) * mm, "end": v(47.74, 133.91) * mm});
            skLineSegment(sketch, "E29.171.1", {"start": v(44.09, 135.69) * mm, "end": v(42.57, 131) * mm, "construction": true});
            skLineSegment(sketch, "E29.171.2", {"start": v(48.8, 134.06) * mm, "end": v(47.08, 129.36) * mm});
            skLineSegment(sketch, "E29.171.3", {"start": v(42.57, 131) * mm, "end": v(47.08, 129.36) * mm});
            skLineSegment(sketch, "E29.171.4", {"start": v(42.57, 131) * mm, "end": v(44.09, 135.69) * mm});
            skLineSegment(sketch, "E29.171.5", {"start": v(48.8, 134.06) * mm, "end": v(48.34, 134.23) * mm});
            skArc(sketch, "E29.171.6", {"start": v(48.34, 134.23) * mm, "mid": v(47.97, 134.2) * mm, "end": v(47.74, 133.91) * mm});
            skArc(sketch, "E29.171.7", {"start": v(44.82, 134.92) * mm, "mid": v(44.82, 135.29) * mm, "end": v(44.55, 135.53) * mm});
            skLineSegment(sketch, "E29.171.8", {"start": v(44.55, 135.53) * mm, "end": v(44.09, 135.69) * mm});
            skArc(sketch, "E29.172.0", {"start": v(40.09, 136.4) * mm, "mid": v(41.07, 134.35) * mm, "end": v(43.04, 135.5) * mm});
            skLineSegment(sketch, "E29.172.1", {"start": v(39.32, 137.14) * mm, "end": v(37.97, 132.41) * mm, "construction": true});
            skLineSegment(sketch, "E29.172.2", {"start": v(44.09, 135.69) * mm, "end": v(42.54, 130.93) * mm});
            skLineSegment(sketch, "E29.172.3", {"start": v(37.97, 132.41) * mm, "end": v(42.54, 130.93) * mm});
            skLineSegment(sketch, "E29.172.4", {"start": v(37.97, 132.41) * mm, "end": v(39.32, 137.14) * mm});
            skLineSegment(sketch, "E29.172.5", {"start": v(44.09, 135.69) * mm, "end": v(43.62, 135.84) * mm});
            skArc(sketch, "E29.172.6", {"start": v(43.62, 135.84) * mm, "mid": v(43.26, 135.8) * mm, "end": v(43.04, 135.5) * mm});
            skArc(sketch, "E29.172.7", {"start": v(40.09, 136.4) * mm, "mid": v(40.08, 136.77) * mm, "end": v(39.8, 137) * mm});
            skLineSegment(sketch, "E29.172.8", {"start": v(39.8, 137) * mm, "end": v(39.32, 137.14) * mm});
            skArc(sketch, "E29.173.0", {"start": v(35.3, 137.72) * mm, "mid": v(36.36, 135.7) * mm, "end": v(38.28, 136.92) * mm});
            skLineSegment(sketch, "E29.173.1", {"start": v(34.51, 138.43) * mm, "end": v(33.32, 133.66) * mm, "construction": true});
            skLineSegment(sketch, "E29.173.2", {"start": v(39.32, 137.14) * mm, "end": v(37.95, 132.33) * mm});
            skLineSegment(sketch, "E29.173.3", {"start": v(33.32, 133.66) * mm, "end": v(37.95, 132.33) * mm});
            skLineSegment(sketch, "E29.173.4", {"start": v(33.32, 133.66) * mm, "end": v(34.51, 138.43) * mm});
            skLineSegment(sketch, "E29.173.5", {"start": v(39.32, 137.14) * mm, "end": v(38.85, 137.28) * mm});
            skArc(sketch, "E29.173.6", {"start": v(38.85, 137.28) * mm, "mid": v(38.5, 137.22) * mm, "end": v(38.28, 136.92) * mm});
            skArc(sketch, "E29.173.7", {"start": v(35.3, 137.72) * mm, "mid": v(35.28, 138.08) * mm, "end": v(34.99, 138.31) * mm});
            skLineSegment(sketch, "E29.173.8", {"start": v(34.99, 138.31) * mm, "end": v(34.51, 138.43) * mm});
            skArc(sketch, "E29.174.0", {"start": v(30.48, 138.87) * mm, "mid": v(31.6, 136.88) * mm, "end": v(33.48, 138.17) * mm});
            skLineSegment(sketch, "E29.174.1", {"start": v(29.66, 139.55) * mm, "end": v(28.64, 134.74) * mm, "construction": true});
            skLineSegment(sketch, "E29.174.2", {"start": v(34.51, 138.43) * mm, "end": v(33.3, 133.58) * mm});
            skLineSegment(sketch, "E29.174.3", {"start": v(28.64, 134.74) * mm, "end": v(33.3, 133.58) * mm});
            skLineSegment(sketch, "E29.174.4", {"start": v(28.64, 134.74) * mm, "end": v(29.66, 139.55) * mm});
            skLineSegment(sketch, "E29.174.5", {"start": v(34.51, 138.43) * mm, "end": v(34.04, 138.55) * mm});
            skArc(sketch, "E29.174.6", {"start": v(34.04, 138.55) * mm, "mid": v(33.68, 138.48) * mm, "end": v(33.48, 138.17) * mm});
            skArc(sketch, "E29.174.7", {"start": v(30.48, 138.87) * mm, "mid": v(30.44, 139.23) * mm, "end": v(30.14, 139.45) * mm});
            skLineSegment(sketch, "E29.174.8", {"start": v(30.14, 139.45) * mm, "end": v(29.66, 139.55) * mm});
            skArc(sketch, "E29.175.0", {"start": v(25.61, 139.84) * mm, "mid": v(26.8, 137.9) * mm, "end": v(28.64, 139.26) * mm});
            skLineSegment(sketch, "E29.175.1", {"start": v(24.77, 140.5) * mm, "end": v(23.92, 135.66) * mm, "construction": true});
            skLineSegment(sketch, "E29.175.2", {"start": v(29.66, 139.55) * mm, "end": v(28.62, 134.66) * mm});
            skLineSegment(sketch, "E29.175.3", {"start": v(23.92, 135.66) * mm, "end": v(28.62, 134.66) * mm});
            skLineSegment(sketch, "E29.175.4", {"start": v(23.92, 135.66) * mm, "end": v(24.77, 140.5) * mm});
            skLineSegment(sketch, "E29.175.5", {"start": v(29.66, 139.55) * mm, "end": v(29.18, 139.65) * mm});
            skArc(sketch, "E29.175.6", {"start": v(29.18, 139.65) * mm, "mid": v(28.82, 139.57) * mm, "end": v(28.64, 139.26) * mm});
            skArc(sketch, "E29.175.7", {"start": v(25.61, 139.84) * mm, "mid": v(25.56, 140.2) * mm, "end": v(25.25, 140.41) * mm});
            skLineSegment(sketch, "E29.175.8", {"start": v(25.25, 140.41) * mm, "end": v(24.77, 140.5) * mm});
            skArc(sketch, "E29.176.0", {"start": v(20.72, 140.65) * mm, "mid": v(21.98, 138.75) * mm, "end": v(23.76, 140.17) * mm});
            skLineSegment(sketch, "E29.176.1", {"start": v(19.86, 141.28) * mm, "end": v(19.17, 136.4) * mm, "construction": true});
            skLineSegment(sketch, "E29.176.2", {"start": v(24.77, 140.5) * mm, "end": v(23.9, 135.57) * mm});
            skLineSegment(sketch, "E29.176.3", {"start": v(19.17, 136.4) * mm, "end": v(23.9, 135.57) * mm});
            skLineSegment(sketch, "E29.176.4", {"start": v(19.17, 136.4) * mm, "end": v(19.86, 141.28) * mm});
            skLineSegment(sketch, "E29.176.5", {"start": v(24.77, 140.5) * mm, "end": v(24.3, 140.58) * mm});
            skArc(sketch, "E29.176.6", {"start": v(24.3, 140.58) * mm, "mid": v(23.94, 140.5) * mm, "end": v(23.76, 140.17) * mm});
            skArc(sketch, "E29.176.7", {"start": v(20.72, 140.65) * mm, "mid": v(20.65, 141.02) * mm, "end": v(20.34, 141.21) * mm});
            skLineSegment(sketch, "E29.176.8", {"start": v(20.34, 141.21) * mm, "end": v(19.86, 141.28) * mm});
            skArc(sketch, "E29.177.0", {"start": v(15.8, 141.3) * mm, "mid": v(17.12, 139.44) * mm, "end": v(18.86, 140.91) * mm});
            skLineSegment(sketch, "E29.177.1", {"start": v(14.91, 141.89) * mm, "end": v(14.4, 137) * mm, "construction": true});
            skLineSegment(sketch, "E29.177.2", {"start": v(19.86, 141.28) * mm, "end": v(19.16, 136.33) * mm});
            skLineSegment(sketch, "E29.177.3", {"start": v(14.4, 137) * mm, "end": v(19.16, 136.33) * mm});
            skLineSegment(sketch, "E29.177.4", {"start": v(14.4, 137) * mm, "end": v(14.91, 141.89) * mm});
            skLineSegment(sketch, "E29.177.5", {"start": v(19.86, 141.28) * mm, "end": v(19.37, 141.35) * mm});
            skArc(sketch, "E29.177.6", {"start": v(19.37, 141.35) * mm, "mid": v(19.02, 141.24) * mm, "end": v(18.86, 140.91) * mm});
            skArc(sketch, "E29.177.7", {"start": v(15.8, 141.3) * mm, "mid": v(15.72, 141.65) * mm, "end": v(15.4, 141.83) * mm});
            skLineSegment(sketch, "E29.177.8", {"start": v(15.4, 141.83) * mm, "end": v(14.91, 141.89) * mm});
            skArc(sketch, "E29.178.0", {"start": v(10.85, 141.76) * mm, "mid": v(12.24, 139.95) * mm, "end": v(13.93, 141.49) * mm});
            skLineSegment(sketch, "E29.178.1", {"start": v(9.95, 142.32) * mm, "end": v(9.6, 137.41) * mm, "construction": true});
            skLineSegment(sketch, "E29.178.2", {"start": v(14.91, 141.89) * mm, "end": v(14.39, 136.91) * mm});
            skLineSegment(sketch, "E29.178.3", {"start": v(9.6, 137.41) * mm, "end": v(14.39, 136.91) * mm});
            skLineSegment(sketch, "E29.178.4", {"start": v(9.6, 137.41) * mm, "end": v(9.95, 142.32) * mm});
            skLineSegment(sketch, "E29.178.5", {"start": v(14.91, 141.89) * mm, "end": v(14.43, 141.94) * mm});
            skArc(sketch, "E29.178.6", {"start": v(14.43, 141.94) * mm, "mid": v(14.08, 141.82) * mm, "end": v(13.93, 141.49) * mm});
            skArc(sketch, "E29.178.7", {"start": v(10.85, 141.76) * mm, "mid": v(10.76, 142.11) * mm, "end": v(10.44, 142.29) * mm});
            skLineSegment(sketch, "E29.178.8", {"start": v(10.44, 142.29) * mm, "end": v(9.95, 142.32) * mm});
            skArc(sketch, "E29.179.0", {"start": v(5.9, 142.05) * mm, "mid": v(7.35, 140.3) * mm, "end": v(8.98, 141.89) * mm});
            skLineSegment(sketch, "E29.179.1", {"start": v(4.98, 142.58) * mm, "end": v(4.8, 137.67) * mm, "construction": true});
            skLineSegment(sketch, "E29.179.2", {"start": v(9.95, 142.32) * mm, "end": v(9.6, 137.33) * mm});
            skLineSegment(sketch, "E29.179.3", {"start": v(4.8, 137.67) * mm, "end": v(9.6, 137.33) * mm});
            skLineSegment(sketch, "E29.179.4", {"start": v(4.8, 137.67) * mm, "end": v(4.98, 142.58) * mm});
            skLineSegment(sketch, "E29.179.5", {"start": v(9.95, 142.32) * mm, "end": v(9.46, 142.35) * mm});
            skArc(sketch, "E29.179.6", {"start": v(9.46, 142.35) * mm, "mid": v(9.12, 142.23) * mm, "end": v(8.98, 141.89) * mm});
            skArc(sketch, "E29.179.7", {"start": v(5.9, 142.05) * mm, "mid": v(5.8, 142.4) * mm, "end": v(5.47, 142.56) * mm});
            skLineSegment(sketch, "E29.179.8", {"start": v(5.47, 142.56) * mm, "end": v(4.98, 142.58) * mm});
            skSolve(sketch);
        }
        {
            var Q0;
            Q0 = qSketchRegion(id + "F4", true);
            var Q1;
            Q1=makeQuery(id+"F1.opRevolve","SWEPT_FACE",FACE,{"disambiguationData":[OSD([sQuery(id+"F0.wireOp",EDGE,"E1")])]});
            var Q2;
            Q2=makeQuery(id+"F1.opRevolve","SWEPT_FACE",FACE,{"disambiguationData":[OSD([sQuery(id+"F0.wireOp",EDGE,"E5")])]});
            extrude(context, id + "F5", {"entities" : qUnion([Q0]), "operationType" : NewBodyOperationType.ADD, "depth" : 13 * mm, "endBoundEntityFace" : qUnion([Q1]), "offsetDistance" : 25 * mm});
        }
    });
